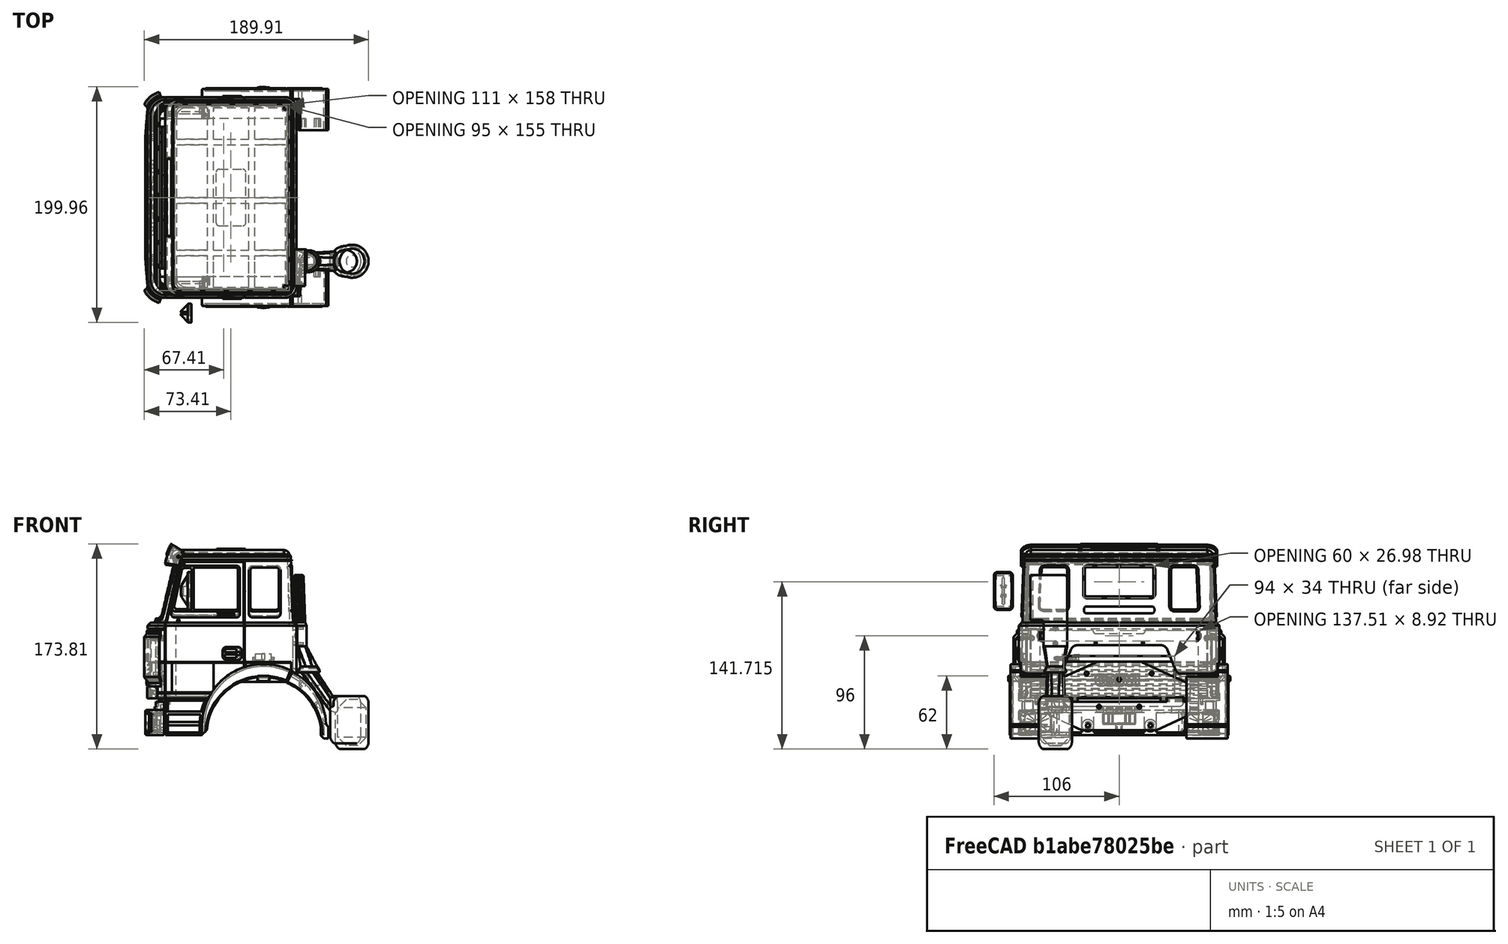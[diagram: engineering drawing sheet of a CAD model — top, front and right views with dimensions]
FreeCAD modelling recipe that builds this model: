
FCSTD DOCUMENT  (FreeCAD 0.18.4R)
Label: Cab-Iveco-Turbo-19
License: CC-BY 3.0
LicenseURL: http://creativecommons.org/licenses/by/3.0/
objects: Part::Box×507, Part::Cut×417, Part::Fillet×310, Part::Cylinder×272, Part::MultiFuse×251, Part::Mirroring×68, Part::Chamfer×61, Part::Feature×40, Part::Loft×19, Part::Part2DObjectPython×10, Part::Extrusion×10, Part::Cone×2, App::DocumentObjectGroup×1
note: 1967 computed .brp shape members not serialized (recipe doc carries the construction recipe); baked Part::Feature solids carry a one-line shape summary decoded from their .brp

FEATURE [Part::Box] Box  label="Cube250"
  AttacherType = Attacher::AttachEngine3D
  Height = 64
  Length = 126
  Width = 170
FEATURE [Part::Fillet] Fillet001
  Base = -> Box
  Edges = 2 edges r=15: [Edge1,Edge3]
FEATURE [Part::Fillet] Fillet
  Base = -> Fillet001
  Edges = 2 edges r=10: [Edge17,Edge18]
FEATURE [Part::Box] Box001  label="Cube251"
  AttacherType = Attacher::AttachEngine3D
  Height = 64
  Length = 120
  Placement = pos=(4,4,0) rot=(0,0,1;0rad)
  Width = 164
FEATURE [Part::Fillet] Fillet003
  Base = -> Box001
  Edges = 2 edges r=12: [Edge1,Edge3]
FEATURE [Part::Fillet] Fillet002
  Base = -> Fillet003
  Edges = 2 edges r=6: [Edge17,Edge18]
  Placement = pos=(-1,-1,0) rot=(0,0,1;0rad)
FEATURE [Part::Cut] Cut001
  Base = -> Fillet
  Refine = true
  Tool = -> Fillet002
FEATURE [Part::Cylinder] Cylinder004
  Angle = 360
  AttacherType = Attacher::AttachEngine3D
  Height = 174
  Placement = pos=(98,174,-23) rot=(1,0,0;1.5708rad)
  Radius = 52
FEATURE [Part::Cut] Cut
  Base = -> Cut001
  Refine = true
  Tool = -> Cylinder004
FEATURE [Part::Box] Box002  label="Cube252"
  AttacherType = Attacher::AttachEngine3D
  Height = 25
  Length = 131
  Placement = pos=(11,0,6) rot=(0,0,1;0rad)
  Width = 170
FEATURE [Part::Box] Box003  label="Cube253"
  AttacherType = Attacher::AttachEngine3D
  Height = 25
  Length = 148
  Placement = pos=(2,2,6) rot=(0,0,1;0rad)
  Width = 166
FEATURE [Part::Box] Box009  label="Cube192"
  AttacherType = Attacher::AttachEngine3D
  Height = 5.8
  Length = 13.6
  Placement = pos=(91.2,163,27) rot=(0,0,1;0rad)
  Width = 4
FEATURE [Part::Box] Box010  label="Cube254"
  AttacherType = Attacher::AttachEngine3D
  Height = 23
  Length = 37
  Placement = pos=(15,152,-23) rot=(0,0,1;0rad)
  Width = 18
FEATURE [Part::Cylinder] Cylinder012
  Angle = 360
  AttacherType = Attacher::AttachEngine3D
  Height = 22
  Placement = pos=(98,174,-23) rot=(1,0,0;1.5708rad)
  Radius = 52
FEATURE [Part::Box] Box011  label="Cube255"
  AttacherType = Attacher::AttachEngine3D
  Height = 9
  Length = 31
  Placement = pos=(17,156,-29) rot=(0,0,1;0rad)
  Width = 14
FEATURE [Part::Cylinder] Cylinder013
  Angle = 360
  AttacherType = Attacher::AttachEngine3D
  Height = 22
  Placement = pos=(98,174,-23) rot=(1,0,0;1.5708rad)
  Radius = 54
FEATURE [Part::Box] Box028  label="Cube266"
  AttacherType = Attacher::AttachEngine3D
  Height = 31
  Length = 62
  Placement = pos=(83,1,2) rot=(0,0,1;0rad)
  Width = 1
FEATURE [Part::Box] Box029  label="Cube267"
  AttacherType = Attacher::AttachEngine3D
  Height = 31
  Length = 63.5
  Placement = pos=(83,-1,2) rot=(0,0,1;0.017453rad)
  Width = 2
FEATURE [Part::Cut] Cut052
  Base = -> Box028
  Refine = true
  Tool = -> Box029
FEATURE [Part::Cylinder] Cylinder037
  Angle = 360
  AttacherType = Attacher::AttachEngine3D
  Height = 10
  Placement = pos=(98,10,-23) rot=(1,0,0;1.5708rad)
  Radius = 52
FEATURE [Part::Cut] Cut051
  Base = -> Cut052
  Refine = true
  Tool = -> Cylinder037
FEATURE [Part::Cylinder] Cylinder038
  Angle = 360
  AttacherType = Attacher::AttachEngine3D
  Height = 10
  Placement = pos=(98,10,-23) rot=(1,0,0;1.5708rad)
  Radius = 52
FEATURE [Part::Box] Box030  label="Cube268"
  AttacherType = Attacher::AttachEngine3D
  Height = 25
  Length = 63.5
  Placement = pos=(20,1,8) rot=(0,0,-1;0.027925rad)
  Width = 1
FEATURE [Part::Box] Box031  label="Cube269"
  AttacherType = Attacher::AttachEngine3D
  Height = 25
  Length = 62.5
  Placement = pos=(20.5,1,8) rot=(0,0,1;0rad)
  Width = 1
FEATURE [Part::Cut] Cut054
  Base = -> Box031
  Refine = true
  Tool = -> Box030
FEATURE [Part::Cut] Cut053
  Base = -> Cut054
  Refine = true
  Tool = -> Cylinder038
FEATURE [Part::MultiFuse] Fusion007
  Refine = true
  Shapes = -> [Cut051,Cut053]
FEATURE [Part::Box] Box032  label="Cube270"
  AttacherType = Attacher::AttachEngine3D
  Height = 25
  Length = 63.5
  Placement = pos=(20,1,8) rot=(0,0,-1;0.027925rad)
  Width = 1
FEATURE [Part::Box] Box033  label="Cube271"
  AttacherType = Attacher::AttachEngine3D
  Height = 25
  Length = 62.5
  Placement = pos=(20.5,1,8) rot=(0,0,1;0rad)
  Width = 1
FEATURE [Part::Cut] Cut057
  Base = -> Box033
  Refine = true
  Tool = -> Box032
FEATURE [Part::Box] Box034  label="Cube272"
  AttacherType = Attacher::AttachEngine3D
  Height = 31
  Length = 63.5
  Placement = pos=(83,-1,2) rot=(0,0,1;0.017453rad)
  Width = 2
FEATURE [Part::Box] Box035  label="Cube273"
  AttacherType = Attacher::AttachEngine3D
  Height = 31
  Length = 62
  Placement = pos=(83,1,2) rot=(0,0,1;0rad)
  Width = 1
FEATURE [Part::Cut] Cut055
  Base = -> Box035
  Refine = true
  Tool = -> Box034
FEATURE [Part::Cylinder] Cylinder039
  Angle = 360
  AttacherType = Attacher::AttachEngine3D
  Height = 10
  Placement = pos=(98,10,-23) rot=(1,0,0;1.5708rad)
  Radius = 52
FEATURE [Part::Cut] Cut058
  Base = -> Cut055
  Refine = true
  Tool = -> Cylinder039
FEATURE [Part::Cylinder] Cylinder040
  Angle = 360
  AttacherType = Attacher::AttachEngine3D
  Height = 10
  Placement = pos=(98,10,-23) rot=(1,0,0;1.5708rad)
  Radius = 52
FEATURE [Part::Cut] Cut056
  Base = -> Cut057
  Refine = true
  Tool = -> Cylinder040
FEATURE [Part::MultiFuse] Fusion008
  Refine = true
  Shapes = -> [Cut058,Cut056]
FEATURE [Part::Mirroring] Part__Mirroring001  label="Fusion008 (Mirror #2)"
  Base = (0,0,0)
  Normal = (0,1,0)
  Placement = pos=(0,170,0) rot=(0,0,1;0rad)
  Source = -> Fusion008
FEATURE [Part::MultiFuse] Fusion009
  Refine = true
  Shapes = -> [Part__Mirroring001,Fusion007]
FEATURE [Part::Cut] Cut059
  Base = -> Box002
  Placement = pos=(0,0,2) rot=(0,0,1;0rad)
  Refine = true
  Tool = -> Box003
FEATURE [Part::Cut] Cut060
  Base = -> Cut059
  Placement = pos=(0,0,-3) rot=(0,0,1;0rad)
  Refine = true
  Tool = -> Fusion009
FEATURE [Part::Cut] Cut061
  Base = -> Cut
  Refine = true
  Tool = -> Cut060
FEATURE [Part::Box] Box036  label="Cube274"
  AttacherType = Attacher::AttachEngine3D
  Height = 64
  Length = 21
  Width = 164
FEATURE [Part::Fillet] Fillet010
  Base = -> Box036
  Edges = 2 edges r=12: [Edge1,Edge3]
  Placement = pos=(3,3,0) rot=(0,0,1;0rad)
FEATURE [Part::Box] Box038  label="Cube276"
  AttacherType = Attacher::AttachEngine3D
  Height = 59
  Length = 16
  Placement = pos=(15,0,0) rot=(0,0,1;0rad)
  Width = 170
FEATURE [Part::Box] Box039  label="Cube277"
  AttacherType = Attacher::AttachEngine3D
  Height = 59
  Length = 21
  Placement = pos=(-13,3,0) rot=(0,0,1;0rad)
  Width = 164
FEATURE [Part::Box] Box040  label="Cube278"
  AttacherType = Attacher::AttachEngine3D
  Height = 59
  Length = 21
  Placement = pos=(-13,0,0) rot=(0,0,1;0rad)
  Width = 170
FEATURE [Part::Fillet] Fillet011
  Base = -> Box040
  Edges = 2 edges r=15: [Edge1,Edge3]
FEATURE [Part::Fillet] Fillet012
  Base = -> Box039
  Edges = 2 edges r=12: [Edge1,Edge3]
  Placement = pos=(3,0,0) rot=(0,0,1;0rad)
FEATURE [Part::Cut] Cut063
  Base = -> Fillet011
  Placement = pos=(13,0,0) rot=(0,0,1;0rad)
  Refine = true
  Tool = -> Fillet012
FEATURE [Part::Cut] Cut064
  Base = -> Cut063
  Refine = true
  Tool = -> Box038
FEATURE [Part::Box] Box041  label="Cube279"
  AttacherType = Attacher::AttachEngine3D
  Height = 28
  Length = 21
  Placement = pos=(-13,3,0) rot=(0,0,1;0rad)
  Width = 164
FEATURE [Part::Fillet] Fillet014
  Base = -> Box041
  Edges = 2 edges r=12: [Edge1,Edge3]
  Placement = pos=(2.5,0,0) rot=(0,0,1;0rad)
FEATURE [Part::Box] Box042  label="Cube280"
  AttacherType = Attacher::AttachEngine3D
  Height = 28
  Length = 21
  Placement = pos=(-13,0,0) rot=(0,0,1;0rad)
  Width = 170
FEATURE [Part::Fillet] Fillet013
  Base = -> Box042
  Edges = 2 edges r=15: [Edge1,Edge3]
FEATURE [Part::Cut] Cut067
  Base = -> Fillet013
  Placement = pos=(13,0,30) rot=(0,0,1;0rad)
  Refine = true
  Tool = -> Fillet014
FEATURE [Part::Box] Box043  label="Cube281"
  AttacherType = Attacher::AttachEngine3D
  Height = 59
  Length = 16
  Placement = pos=(14.5,0,0) rot=(0,0,1;0rad)
  Width = 170
FEATURE [Part::Cut] Cut066
  Base = -> Cut067
  Refine = true
  Tool = -> Box043
FEATURE [Part::Box] Box044  label="Cube282"
  AttacherType = Attacher::AttachEngine3D
  Height = 3
  Length = 3
  Placement = pos=(0,63,55) rot=(0,0,1;0rad)
  Width = 44
FEATURE [Part::Fillet] Fillet015
  Base = -> Box044
  Edges = 2 edges r=2: [Edge9,Edge11]
FEATURE [Part::Box] Box047  label="Cube285"
  AttacherType = Attacher::AttachEngine3D
  Height = 33
  Length = 21
  Placement = pos=(-13,3,0) rot=(0,0,1;0rad)
  Width = 164
FEATURE [Part::Fillet] Fillet016
  Base = -> Box047
  Edges = 2 edges r=12: [Edge1,Edge3]
  Placement = pos=(15.5,0,0) rot=(0,0,1;0rad)
FEATURE [Part::Box] Box070  label="Cube308"
  AttacherType = Attacher::AttachEngine3D
  Height = 4
  Length = 21
  Placement = pos=(-13,0,26) rot=(0,0,1;0rad)
  Width = 170
FEATURE [Part::Fillet] Fillet026
  Base = -> Box070
  Edges = 2 edges r=15: [Edge1,Edge3]
FEATURE [Part::Chamfer] Chamfer011
  Base = -> Fillet026
  Edges = 1 edges r=3.5: [Edge1]
  Placement = pos=(13,0,2) rot=(0,0,1;0rad)
FEATURE [Part::Box] Box071  label="Cube309"
  AttacherType = Attacher::AttachEngine3D
  Height = 4
  Length = 11
  Placement = pos=(10.5,0,28) rot=(0,0,1;0rad)
  Width = 170
FEATURE [Part::Cut] Cut077
  Base = -> Chamfer011
  Placement = pos=(0,0,-28) rot=(0,0,1;0rad)
  Refine = true
  Tool = -> Box071
FEATURE [Part::Box] Box072  label="Cube310"
  AttacherType = Attacher::AttachEngine3D
  Height = 4
  Length = 21
  Placement = pos=(-13,0,26) rot=(0,0,1;0rad)
  Width = 170
FEATURE [Part::Box] Box073  label="Cube311"
  AttacherType = Attacher::AttachEngine3D
  Height = 4
  Length = 11
  Placement = pos=(10.5,0,28) rot=(0,0,1;0rad)
  Width = 170
FEATURE [Part::Fillet] Fillet027
  Base = -> Box072
  Edges = 2 edges r=15: [Edge1,Edge3]
FEATURE [Part::Chamfer] Chamfer012
  Base = -> Fillet027
  Edges = 1 edges r=3.5: [Edge1]
  Placement = pos=(13,0,2) rot=(0,0,1;0rad)
FEATURE [Part::Cut] Cut078
  Base = -> Chamfer012
  Placement = pos=(0,0,-24) rot=(0,0,1;0rad)
  Refine = true
  Tool = -> Box073
FEATURE [Part::Box] Box074  label="Cube312"
  AttacherType = Attacher::AttachEngine3D
  Height = 4
  Length = 21
  Placement = pos=(-13,0,26) rot=(0,0,1;0rad)
  Width = 170
FEATURE [Part::Box] Box075  label="Cube313"
  AttacherType = Attacher::AttachEngine3D
  Height = 4
  Length = 11
  Placement = pos=(10.5,0,28) rot=(0,0,1;0rad)
  Width = 170
FEATURE [Part::Fillet] Fillet028
  Base = -> Box074
  Edges = 2 edges r=15: [Edge1,Edge3]
FEATURE [Part::Chamfer] Chamfer013
  Base = -> Fillet028
  Edges = 1 edges r=3.5: [Edge1]
  Placement = pos=(13,0,2) rot=(0,0,1;0rad)
FEATURE [Part::Cut] Cut079
  Base = -> Chamfer013
  Placement = pos=(0,0,-20) rot=(0,0,1;0rad)
  Refine = true
  Tool = -> Box075
FEATURE [Part::Box] Box076  label="Cube314"
  AttacherType = Attacher::AttachEngine3D
  Height = 4
  Length = 21
  Placement = pos=(-13,0,26) rot=(0,0,1;0rad)
  Width = 170
FEATURE [Part::Box] Box077  label="Cube315"
  AttacherType = Attacher::AttachEngine3D
  Height = 4
  Length = 11
  Placement = pos=(10.5,0,28) rot=(0,0,1;0rad)
  Width = 170
FEATURE [Part::Fillet] Fillet029
  Base = -> Box076
  Edges = 2 edges r=15: [Edge1,Edge3]
FEATURE [Part::Chamfer] Chamfer014
  Base = -> Fillet029
  Edges = 1 edges r=3.5: [Edge1]
  Placement = pos=(13,0,2) rot=(0,0,1;0rad)
FEATURE [Part::Cut] Cut080
  Base = -> Chamfer014
  Placement = pos=(0,0,-16) rot=(0,0,1;0rad)
  Refine = true
  Tool = -> Box077
FEATURE [Part::Box] Box078  label="Cube316"
  AttacherType = Attacher::AttachEngine3D
  Height = 4
  Length = 21
  Placement = pos=(-13,0,26) rot=(0,0,1;0rad)
  Width = 170
FEATURE [Part::Box] Box079  label="Cube317"
  AttacherType = Attacher::AttachEngine3D
  Height = 4
  Length = 11
  Placement = pos=(10.5,0,28) rot=(0,0,1;0rad)
  Width = 170
FEATURE [Part::Fillet] Fillet030
  Base = -> Box078
  Edges = 2 edges r=15: [Edge1,Edge3]
FEATURE [Part::Chamfer] Chamfer015
  Base = -> Fillet030
  Edges = 1 edges r=3.5: [Edge1]
  Placement = pos=(13,0,2) rot=(0,0,1;0rad)
FEATURE [Part::Cut] Cut081
  Base = -> Chamfer015
  Placement = pos=(0,0,-12) rot=(0,0,1;0rad)
  Refine = true
  Tool = -> Box079
FEATURE [Part::Box] Box080  label="Cube318"
  AttacherType = Attacher::AttachEngine3D
  Height = 4
  Length = 21
  Placement = pos=(-13,0,26) rot=(0,0,1;0rad)
  Width = 170
FEATURE [Part::Box] Box081  label="Cube319"
  AttacherType = Attacher::AttachEngine3D
  Height = 4
  Length = 11
  Placement = pos=(10.5,0,28) rot=(0,0,1;0rad)
  Width = 170
FEATURE [Part::Fillet] Fillet031
  Base = -> Box080
  Edges = 2 edges r=15: [Edge1,Edge3]
FEATURE [Part::Chamfer] Chamfer016
  Base = -> Fillet031
  Edges = 1 edges r=3.5: [Edge1]
  Placement = pos=(13,0,2) rot=(0,0,1;0rad)
FEATURE [Part::Cut] Cut082
  Base = -> Chamfer016
  Placement = pos=(0,0,-8) rot=(0,0,1;0rad)
  Refine = true
  Tool = -> Box081
FEATURE [Part::Box] Box082  label="Cube320"
  AttacherType = Attacher::AttachEngine3D
  Height = 4
  Length = 21
  Placement = pos=(-13,0,26) rot=(0,0,1;0rad)
  Width = 170
FEATURE [Part::Box] Box083  label="Cube321"
  AttacherType = Attacher::AttachEngine3D
  Height = 4
  Length = 11
  Placement = pos=(10.5,0,28) rot=(0,0,1;0rad)
  Width = 170
FEATURE [Part::Fillet] Fillet032
  Base = -> Box082
  Edges = 2 edges r=15: [Edge1,Edge3]
FEATURE [Part::Chamfer] Chamfer017
  Base = -> Fillet032
  Edges = 1 edges r=3.5: [Edge1]
  Placement = pos=(13,0,2) rot=(0,0,1;0rad)
FEATURE [Part::Cut] Cut083
  Base = -> Chamfer017
  Placement = pos=(0,0,-4) rot=(0,0,1;0rad)
  Refine = true
  Tool = -> Box083
FEATURE [Part::Box] Box084  label="Cube322"
  AttacherType = Attacher::AttachEngine3D
  Height = 4
  Length = 21
  Placement = pos=(-13,0,26) rot=(0,0,1;0rad)
  Width = 170
FEATURE [Part::Box] Box085  label="Cube323"
  AttacherType = Attacher::AttachEngine3D
  Height = 4
  Length = 11
  Placement = pos=(10.5,0,28) rot=(0,0,1;0rad)
  Width = 170
FEATURE [Part::Fillet] Fillet033
  Base = -> Box084
  Edges = 2 edges r=15: [Edge1,Edge3]
FEATURE [Part::Chamfer] Chamfer018
  Base = -> Fillet033
  Edges = 1 edges r=3.5: [Edge1]
  Placement = pos=(13,0,2) rot=(0,0,1;0rad)
FEATURE [Part::Cut] Cut084
  Base = -> Chamfer018
  Refine = true
  Tool = -> Box085
FEATURE [Part::MultiFuse] Fusion011
  Refine = true
  Shapes = -> [Cut084,Cut083,Cut080,Cut081,Cut078,Cut079,Cut082,Cut077]
FEATURE [Part::Box] Box086  label="Cube324"
  AttacherType = Attacher::AttachEngine3D
  Height = 30
  Length = 21
  Placement = pos=(-13,3,0) rot=(0,0,1;0rad)
  Width = 164
FEATURE [Part::Fillet] Fillet034
  Base = -> Box086
  Edges = 2 edges r=12: [Edge1,Edge3]
  Placement = pos=(15.5,0,0) rot=(0,0,1;0rad)
FEATURE [Part::Box] Box087  label="Cube325"
  AttacherType = Attacher::AttachEngine3D
  Height = 30
  Length = 21
  Placement = pos=(-13,2.5,0) rot=(0,0,1;0rad)
  Width = 165
FEATURE [Part::Fillet] Fillet035
  Base = -> Box087
  Edges = 2 edges r=12.5: [Edge1,Edge3]
  Placement = pos=(15,0,0) rot=(0,0,1;0rad)
FEATURE [Part::Cut] Cut086
  Base = -> Fillet035
  Refine = true
  Tool = -> Fillet034
FEATURE [Part::Box] Box088  label="Cube326"
  AttacherType = Attacher::AttachEngine3D
  Height = 30
  Length = 16
  Placement = pos=(10.5,0,0) rot=(0,0,1;0rad)
  Width = 170
FEATURE [Part::Cut] Cut087
  Base = -> Cut086
  Refine = true
  Tool = -> Box088
FEATURE [Part::Box] Box089  label="Cube327"
  AttacherType = Attacher::AttachEngine3D
  Height = 3
  Length = 21
  Placement = pos=(-5,0,30) rot=(0,0,1;0rad)
  Width = 170
FEATURE [Part::Feature] Face
  Placement = pos=(0,0,-10) rot=(0,0,1;0rad)
  shape: bbox 128.7 x 180.4 x 2e-07 mm, 1 faces, 0 solids (baked)
FEATURE [Part::Feature] Face002
  Placement = pos=(0,0,50) rot=(0,0,1;0rad)
  shape: bbox 110 x 176 x 2e-07 mm, 1 faces, 0 solids (baked)
FEATURE [Part::Loft] Loft
  Closed = false
  MaxDegree = 5
  Ruled = false
  Sections = -> [Face002,Face]
  Solid = true
FEATURE [Part::Feature] Face003
  Placement = pos=(0,0,50) rot=(0,0,1;0rad)
  shape: bbox 103.4 x 169.4 x 2e-07 mm, 1 faces, 0 solids (baked)
FEATURE [Part::Feature] Face004
  Placement = pos=(0,0,-10) rot=(0,0,1;0rad)
  shape: bbox 122.1 x 173.8 x 2e-07 mm, 1 faces, 0 solids (baked)
FEATURE [Part::Loft] Loft001
  Closed = false
  MaxDegree = 5
  Ruled = false
  Sections = -> [Face003,Face004]
  Solid = true
FEATURE [Part::Cut] Cut091
  Base = -> Loft
  Refine = true
  Tool = -> Loft001
FEATURE [Part::Box] Box094  label="Cube332"
  AttacherType = Attacher::AttachEngine3D
  Height = 30
  Length = 21
  Placement = pos=(-13,0,0) rot=(0,0,1;0rad)
  Width = 170
FEATURE [Part::Fillet] Fillet044
  Base = -> Box094
  Edges = 2 edges r=15: [Edge1,Edge3]
FEATURE [Part::Box] Box095  label="Cube333"
  AttacherType = Attacher::AttachEngine3D
  Height = 30
  Length = 21
  Placement = pos=(-13,3,0) rot=(0,0,1;0rad)
  Width = 164
FEATURE [Part::Fillet] Fillet045
  Base = -> Box095
  Edges = 2 edges r=12: [Edge1,Edge3]
  Placement = pos=(2.5,0,0) rot=(0,0,1;0rad)
FEATURE [Part::Cut] Cut092
  Base = -> Fillet044
  Placement = pos=(13,0,0) rot=(0,0,1;0rad)
  Refine = true
  Tool = -> Fillet045
FEATURE [Part::Box] Box096  label="Cube334"
  AttacherType = Attacher::AttachEngine3D
  Height = 30
  Length = 16
  Placement = pos=(14.5,0,0) rot=(0,0,1;0rad)
  Width = 170
FEATURE [Part::Cut] Cut093
  Base = -> Cut092
  Refine = true
  Tool = -> Box096
FEATURE [Part::Box] Box097  label="Cube335"
  AttacherType = Attacher::AttachEngine3D
  Height = 30
  Length = 16
  Placement = pos=(0,10,0) rot=(0,0,1;0rad)
  Width = 150
FEATURE [Part::Cut] Cut094
  Base = -> Cut093
  Refine = true
  Tool = -> Box097
FEATURE [Part::Box] Box098  label="Cube336"
  AttacherType = Attacher::AttachEngine3D
  Height = 30
  Length = 16
  Placement = pos=(10.5,0,0) rot=(0,0,1;0rad)
  Width = 170
FEATURE [Part::Box] Box099  label="Cube337"
  AttacherType = Attacher::AttachEngine3D
  Height = 30
  Length = 21
  Placement = pos=(-13,0,0) rot=(0,0,1;0rad)
  Width = 170
FEATURE [Part::Fillet] Fillet047
  Base = -> Box099
  Edges = 2 edges r=15: [Edge1,Edge3]
FEATURE [Part::Box] Box100  label="Cube338"
  AttacherType = Attacher::AttachEngine3D
  Height = 30
  Length = 21
  Placement = pos=(-13,3,0) rot=(0,0,1;0rad)
  Width = 164
FEATURE [Part::Fillet] Fillet046
  Base = -> Box100
  Edges = 2 edges r=12: [Edge1,Edge3]
  Placement = pos=(2.5,0,0) rot=(0,0,1;0rad)
FEATURE [Part::Cut] Cut096
  Base = -> Fillet047
  Placement = pos=(13,0,0) rot=(0,0,1;0rad)
  Refine = true
  Tool = -> Fillet046
FEATURE [Part::Cut] Cut097
  Base = -> Cut096
  Refine = true
  Tool = -> Box098
FEATURE [Part::Box] Box101  label="Cube339"
  AttacherType = Attacher::AttachEngine3D
  Height = 30
  Length = 16
  Placement = pos=(0,10.5,0) rot=(0,0,1;0rad)
  Width = 149
FEATURE [Part::Cut] Cut095
  Base = -> Cut097
  Refine = true
  Tool = -> Box101
FEATURE [Part::Box] Box102  label="Cube340"
  AttacherType = Attacher::AttachEngine3D
  Height = 55
  Length = 10
  Placement = pos=(0,7,68) rot=(0,1,0;0.226893rad)
  Width = 156
FEATURE [Part::Cut] Cut099
  Base = -> Cut066
  Refine = true
  Tool = -> Fillet015
FEATURE [Part::Cut] Cut100
  Base = -> Fusion011
  Refine = true
  Tool = -> Fillet016
FEATURE [Part::MultiFuse] Fusion016
  Refine = true
  Shapes = -> [Cut087,Cut100]
FEATURE [Part::Cut] Cut101
  Base = -> Fusion016
  Refine = true
  Tool = -> Box089
FEATURE [Part::Cut] Cut102  label="radiator-grid-00"
  Base = -> Cut101
  Refine = true
  Tool = -> Cut095
FEATURE [Part::Chamfer] Chamfer
  Base = -> Cut061
  Edges = 4 edges r=2.5: [Edge1,Edge4,Edge5,Edge8]
FEATURE [Part::Chamfer] Chamfer019
  Base = -> Chamfer
  Edges = 4 edges r=0.9: [Edge52,Edge80,Edge102,Edge110]
FEATURE [Part::Box] Box104  label="Cube342"
  AttacherType = Attacher::AttachEngine3D
  Height = 7.5
  Length = 4
  Placement = pos=(44,152,-31) rot=(0,0,1;0rad)
  Width = 22
FEATURE [Part::Box] Box105  label="Cube343"
  AttacherType = Attacher::AttachEngine3D
  Height = 18
  Length = 31
  Placement = pos=(17,158,-20) rot=(0,0,1;0rad)
  Width = 12
FEATURE [Part::Cylinder] Cylinder043
  Angle = 360
  AttacherType = Attacher::AttachEngine3D
  Height = 22
  Placement = pos=(98,174,-23) rot=(1,0,0;1.5708rad)
  Radius = 54
FEATURE [Part::Cut] Cut108
  Base = -> Box105
  Refine = true
  Tool = -> Cylinder043
FEATURE [Part::Box] Box106  label="Cube344"
  AttacherType = Attacher::AttachEngine3D
  Height = 21
  Length = 38
  Placement = pos=(15,167,-23) rot=(0,0,1;0rad)
  Width = 3
FEATURE [Part::Box] Box107  label="Cube345"
  AttacherType = Attacher::AttachEngine3D
  Height = 7
  Length = 10
  Placement = pos=(46,152,-30) rot=(0,0,1;0rad)
  Width = 25
FEATURE [Part::Cylinder] Cylinder044
  Angle = 360
  AttacherType = Attacher::AttachEngine3D
  Height = 25
  Placement = pos=(98,177,-23) rot=(0.799251,-0.424969,0.424969;1.79303rad)
  Radius = 52
FEATURE [Part::Cylinder] Cylinder045
  Angle = 360
  AttacherType = Attacher::AttachEngine3D
  Height = 28
  Placement = pos=(98,175,-23) rot=(0.799251,-0.424969,0.424969;1.79303rad)
  Radius = 50
FEATURE [Part::Cylinder] Cylinder046
  Angle = 360
  AttacherType = Attacher::AttachEngine3D
  Height = 30
  Placement = pos=(98,177,-30) rot=(0.799251,-0.424969,0.424969;1.79303rad)
  Radius = 48
FEATURE [Part::MultiFuse] Fusion018
  Refine = true
  Shapes = -> [Box107,Cylinder044]
FEATURE [Part::Box] Box108  label="Cube346"
  AttacherType = Attacher::AttachEngine3D
  Height = 7
  Length = 10
  Placement = pos=(48,147,-30) rot=(0,0,1;0rad)
  Width = 28
FEATURE [Part::Cut] Cut111
  Base = -> Fusion018
  Refine = true
  Tool = -> Cylinder045
FEATURE [Part::Cut] Cut112
  Base = -> Cut111
  Refine = true
  Tool = -> Cylinder046
FEATURE [Part::Cut] Cut113
  Base = -> Cut112
  Refine = true
  Tool = -> Box108
FEATURE [Part::Box] Box109  label="Cube347"
  AttacherType = Attacher::AttachEngine3D
  Height = 7
  Length = 45
  Placement = pos=(76,175,14) rot=(0,0,1;0rad)
  Width = 2
FEATURE [Part::MultiFuse] Fusion019
  Refine = true
  Shapes = -> [Cut113,Box109]
FEATURE [Part::Box] Box110  label="Cube348"
  AttacherType = Attacher::AttachEngine3D
  Height = 14
  Length = 10
  Placement = pos=(116,168,12) rot=(0,1,0;0.401426rad)
  Width = 9
FEATURE [Part::Fillet] Fillet050
  Base = -> Box102
  Edges = 4 edges r=5: [Edge9,Edge10,Edge11,Edge12]
  Placement = pos=(6,0,-1) rot=(0,0,1;0rad)
FEATURE [Part::Box] Box124  label="Cube024"
  AttacherType = Attacher::AttachEngine3D
  Height = 42
  Length = 26
  Placement = pos=(89,4.3,70) rot=(-1,0,0;0.038397rad)
  Width = 5
FEATURE [Part::Fillet] Fillet051
  Base = -> Box124
  Edges = 4 edges r=3: [Edge2,Edge4,Edge6,Edge8]
  Placement = pos=(-3,-2,0) rot=(0,0,1;0rad)
FEATURE [Part::Box] Box126  label="Cube048"
  AttacherType = Attacher::AttachEngine3D
  Height = 42
  Length = 58
  Placement = pos=(19.5,2,70) rot=(-1,0,0;0.038397rad)
  Width = 5
FEATURE [Part::Box] Box127  label="Cube049"
  AttacherType = Attacher::AttachEngine3D
  Height = 48
  Length = 11
  Placement = pos=(8.5,1,70) rot=(-0.179679,0.983544,0.018885;0.212918rad)
  Width = 7
FEATURE [Part::Cut] Cut129
  Base = -> Box126
  Refine = true
  Tool = -> Box127
FEATURE [Part::Fillet] Fillet052
  Base = -> Cut129
  Edges = 4 edges r=3: [Edge2,Edge4,Edge8,Edge12]
FEATURE [Part::MultiFuse] Fusion029  label="left-windows-holes"
  Refine = true
  Shapes = -> [Fillet051,Fillet052]
FEATURE [Part::Box] Box128  label="Cube362"
  AttacherType = Attacher::AttachEngine3D
  Height = 42
  Length = 26
  Placement = pos=(89,4.3,70) rot=(-1,0,0;0.038397rad)
  Width = 5
FEATURE [Part::Fillet] Fillet053
  Base = -> Box128
  Edges = 4 edges r=3: [Edge2,Edge4,Edge6,Edge8]
  Placement = pos=(-3,-2,0) rot=(0,0,1;0rad)
FEATURE [Part::Box] Box129  label="Cube363"
  AttacherType = Attacher::AttachEngine3D
  Height = 42
  Length = 58
  Placement = pos=(19.5,2,70) rot=(-1,0,0;0.038397rad)
  Width = 5
FEATURE [Part::Box] Box130  label="Cube364"
  AttacherType = Attacher::AttachEngine3D
  Height = 48
  Length = 11
  Placement = pos=(8.5,1,70) rot=(-0.179679,0.983544,0.018885;0.212918rad)
  Width = 7
FEATURE [Part::Cut] Cut130
  Base = -> Box129
  Refine = true
  Tool = -> Box130
FEATURE [Part::Fillet] Fillet054
  Base = -> Cut130
  Edges = 4 edges r=3: [Edge2,Edge4,Edge8,Edge12]
FEATURE [Part::MultiFuse] Fusion030
  Refine = true
  Shapes = -> [Fillet053,Fillet054]
FEATURE [Part::Mirroring] Part__Mirroring  label="right-windows-holes"
  Base = (0,0,0)
  Normal = (0,1,0)
  Placement = pos=(0,170,0) rot=(0,0,1;0rad)
  Source = -> Fusion030
FEATURE [Part::Box] Box131  label="Cube086"
  AttacherType = Attacher::AttachEngine3D
  Height = 25
  Length = 10
  Placement = pos=(150,40,0) rot=(0,0,1;0rad)
  Width = 100
FEATURE [Part::Box] Box132  label="Cube089"
  AttacherType = Attacher::AttachEngine3D
  Height = 40
  Length = 10
  Placement = pos=(150,19,0) rot=(-1,0,0;0.383972rad)
  Width = 20
FEATURE [Part::Box] Box133  label="Cube088"
  AttacherType = Attacher::AttachEngine3D
  Height = 40
  Length = 10
  Placement = pos=(150,19,0) rot=(-1,0,0;0.383972rad)
  Width = 20
FEATURE [Part::Mirroring] Part__Mirroring003  label="Cube088 (Mirror #13)"
  Base = (0,0,0)
  Normal = (0,1,0)
  Placement = pos=(0,180,0) rot=(0,0,1;0rad)
  Source = -> Box133
FEATURE [Part::MultiFuse] Fusion033
  Refine = true
  Shapes = -> [Box132,Part__Mirroring003]
FEATURE [Part::Cut] Cut132
  Base = -> Box131
  Placement = pos=(-30,-5,20) rot=(0,0,1;0rad)
  Refine = true
  Tool = -> Fusion033
FEATURE [Part::Fillet] Fillet055
  Base = -> Cut132
  Edges = 2 edges r=6: [Edge5,Edge6]
FEATURE [Part::Cut] Cut134
  Base = -> Fusion019
  Refine = true
  Tool = -> Box110
FEATURE [Part::Box] Box134  label="Cube365"
  AttacherType = Attacher::AttachEngine3D
  Height = 10
  Length = 10
  Placement = pos=(46,152,-31) rot=(0,1,0;0.785398rad)
  Width = 25
FEATURE [Part::Box] Box147  label="Cube074"
  AttacherType = Attacher::AttachEngine3D
  Height = 27
  Length = 7
  Placement = pos=(116,55,85) rot=(0,-1,0;0.034907rad)
  Width = 60
FEATURE [Part::Box] Box148  label="Cube079"
  AttacherType = Attacher::AttachEngine3D
  Height = 38
  Length = 5
  Placement = pos=(175,0,0) rot=(0,0,1;0rad)
  Width = 25
FEATURE [Part::Box] Box149  label="Cube080"
  AttacherType = Attacher::AttachEngine3D
  Height = 40
  Length = 5
  Placement = pos=(175,-24,-1) rot=(-1,0,0;0.038397rad)
  Width = 24
FEATURE [Part::Cut] Cut149
  Base = -> Box148
  Placement = pos=(0,1,1) rot=(0,0,1;0rad)
  Refine = true
  Tool = -> Box149
FEATURE [Part::Cylinder] Cylinder052
  Angle = 360
  AttacherType = Attacher::AttachEngine3D
  Height = 134
  Radius = 3.7
FEATURE [Part::Fillet] Fillet062
  Base = -> Cylinder052
  Edges = 2 edges r=2: [Edge1,Edge3]
  Placement = pos=(128,152,53) rot=(1,0,0;1.5708rad)
FEATURE [Part::Box] Box150  label="Cube378"
  AttacherType = Attacher::AttachEngine3D
  Height = 38
  Length = 5
  Placement = pos=(175,0,0) rot=(0,0,1;0rad)
  Width = 25
FEATURE [Part::Box] Box151  label="Cube379"
  AttacherType = Attacher::AttachEngine3D
  Height = 40
  Length = 5
  Placement = pos=(175,-24,-1) rot=(-1,0,0;0.038397rad)
  Width = 24
FEATURE [Part::Cut] Cut150
  Base = -> Box150
  Placement = pos=(-57,17,74) rot=(0,0,1;0rad)
  Refine = true
  Tool = -> Box151
FEATURE [Part::Mirroring] Part__Mirroring005  label="Cut212"
  Base = (0,0,0)
  Normal = (0,1,0)
  Placement = pos=(-57,154,73) rot=(0,0,1;0rad)
  Source = -> Cut149
FEATURE [Part::Fillet] Fillet063
  Base = -> Cut150
  Edges = 4 edges r=3: [Edge1,Edge3,Edge5,Edge10]
  Placement = pos=(3,0,-4) rot=(0,-1,0;0.034907rad)
FEATURE [Part::Fillet] Fillet064
  Base = -> Part__Mirroring005
  Edges = 4 edges r=3: [Edge1,Edge3,Edge5,Edge10]
  Placement = pos=(3,0,-4) rot=(0,-1,0;0.034907rad)
FEATURE [Part::Cylinder] Cylinder053
  Angle = 360
  AttacherType = Attacher::AttachEngine3D
  Height = 60
  Radius = 3.7
FEATURE [Part::Fillet] Fillet066
  Base = -> Cylinder053
  Edges = 2 edges r=2: [Edge1,Edge3]
  Placement = pos=(125,115,75) rot=(1,0,0;1.5708rad)
FEATURE [Part::Box] Box152  label="Cube070"
  AttacherType = Attacher::AttachEngine3D
  Height = 9
  Length = 14
  Width = 2
FEATURE [Part::Fillet] Fillet068
  Base = -> Box152
  Edges = 4 edges r=2: [Edge2,Edge4,Edge6,Edge8]
  Placement = pos=(68.5,0,46.5) rot=(0,0,1;0rad)
FEATURE [Part::Box] Box153  label="Cube071"
  AttacherType = Attacher::AttachEngine3D
  Height = 9
  Length = 14
  Width = 2
FEATURE [Part::Fillet] Fillet069
  Base = -> Box153
  Edges = 4 edges r=2: [Edge2,Edge4,Edge6,Edge8]
  Placement = pos=(68.5,168,46.5) rot=(0,0,1;0rad)
FEATURE [Part::MultiFuse] Fusion042
  Placement = pos=(-4,0,-13) rot=(0,0,1;0rad)
  Refine = true
  Shapes = -> [Fillet069,Fillet068]
FEATURE [Part::Part2DObjectPython] ShapeString  # Draft 2D object (typed FeaturePython)
  FontFile = <userpath>/Data/Temp/Futura Extra Bold.ttf
  MapMode = 5
  Placement = pos=(0,103,12) rot=(0.57735,-0.57735,-0.57735;2.0944rad)
  Size = 3.5
  String = IVECO
  Tracking = 0.5
FEATURE [Part::Extrusion] Extrude  label="iveco-logo"
  Base = -> ShapeString
  Dir = (1,0,0)
  DirMode = 0
  FaceMakerClass = Part::FaceMakerExtrusion
  LengthFwd = 0
  LengthRev = 0
  Placement = pos=(-1,0,0) rot=(0,0,1;0rad)
  Solid = false
  Symmetric = false
FEATURE [Part::Part2DObjectPython] ShapeString001  # Draft 2D object (typed FeaturePython)
  FontFile = <path>
  MapMode = 5
  Placement = pos=(0,55,34) rot=(0.57735,-0.57735,-0.57735;2.0944rad)
  Size = 1.35
  String = T
  Tracking = 0
FEATURE [Part::Part2DObjectPython] ShapeString002  # Draft 2D object (typed FeaturePython)
  FontFile = <path>
  MapMode = 5
  Placement = pos=(0,51,34) rot=(0.57735,-0.57735,-0.57735;2.0944rad)
  Size = 1.3
  String = urbo
  Tracking = 0
FEATURE [Part::Extrusion] Extrude001
  Base = -> ShapeString001
  Dir = (1,0,0)
  DirMode = 0
  FaceMakerClass = Part::FaceMakerExtrusion
  LengthFwd = 0
  LengthRev = 0
  Solid = false
  Symmetric = false
FEATURE [Part::Extrusion] Extrude002
  Base = -> ShapeString002
  Dir = (1,0,0)
  DirMode = 0
  FaceMakerClass = Part::FaceMakerExtrusion
  LengthFwd = 0
  LengthRev = 0
  Solid = false
  Symmetric = false
FEATURE [Part::MultiFuse] Fusion047  label="turbo-logo"
  Placement = pos=(-1,-3,-2) rot=(0,0,1;0rad)
  Refine = true
  Shapes = -> [Extrude001,Extrude002]
FEATURE [Part::Box] Box167  label="Cube393"
  AttacherType = Attacher::AttachEngine3D
  Height = 21
  Length = 16
  Placement = pos=(-2,0,-30) rot=(0,0,1;0rad)
  Width = 170
FEATURE [Part::Cylinder] Cylinder056
  Angle = 360
  AttacherType = Attacher::AttachEngine3D
  Height = 21
  Placement = pos=(796.4,85,-30) rot=(0,0,1;2.96706rad)
  Radius = 800
FEATURE [Part::Box] Box168  label="Cube394"
  AttacherType = Attacher::AttachEngine3D
  Height = 21
  Length = 16
  Placement = pos=(-2,0,-30) rot=(0,0,1;0rad)
  Width = 170
FEATURE [Part::Cut] Cut163  label="Cut613"
  Base = -> Box168
  Refine = true
  Tool = -> Cylinder056
FEATURE [Part::Cut] Cut164  label="Cut177"
  Base = -> Box167
  Refine = true
  Tool = -> Cut163
FEATURE [Part::Fillet] Fillet083
  Base = -> Cut164
  Edges = 2 edges r=4: [Edge6,Edge12]
FEATURE [Part::Box] Box169  label="Cube395"
  AttacherType = Attacher::AttachEngine3D
  Height = 17
  Length = 20
  Placement = pos=(-2,0,-28) rot=(0,0,1;0rad)
  Width = 30
FEATURE [Part::Fillet] Fillet084
  Base = -> Box169
  Edges = 4 edges r=2: [Edge9,Edge10,Edge11,Edge12]
  Placement = pos=(-1,2,0) rot=(0,0,1;0rad)
FEATURE [Part::Box] Box170  label="Cube396"
  AttacherType = Attacher::AttachEngine3D
  Height = 17
  Length = 20
  Placement = pos=(-2,0,-28) rot=(0,0,1;0rad)
  Width = 30
FEATURE [Part::Fillet] Fillet085
  Base = -> Box170
  Edges = 4 edges r=2: [Edge9,Edge10,Edge11,Edge12]
  Placement = pos=(-1,138,0) rot=(0,0,1;0rad)
FEATURE [Part::MultiFuse] Fusion048
  Refine = true
  Shapes = -> [Fillet085,Fillet084]
FEATURE [Part::Box] Box171  label="Cube397"
  AttacherType = Attacher::AttachEngine3D
  Height = 17
  Length = 16
  Placement = pos=(-2,4,-30) rot=(0,0,1;0rad)
  Width = 162
FEATURE [Part::Fillet] Fillet086
  Base = -> Box171
  Edges = 2 edges r=3: [Edge1,Edge3]
  Placement = pos=(5,0,2) rot=(0,0,1;0rad)
FEATURE [Part::Cut] Cut165  label="Cut178"
  Base = -> Fillet083
  Refine = true
  Tool = -> Fillet086
FEATURE [Part::Box] Box172  label="Cube398"
  AttacherType = Attacher::AttachEngine3D
  Height = 17
  Length = 15
  Placement = pos=(2,30,-28) rot=(0,0,1;0rad)
  Width = 5
FEATURE [Part::Box] Box173  label="Cube399"
  AttacherType = Attacher::AttachEngine3D
  Height = 17
  Length = 15
  Placement = pos=(2,135,-28) rot=(0,0,1;0rad)
  Width = 5
FEATURE [Part::MultiFuse] Fusion049
  Refine = true
  Shapes = -> [Box173,Box172]
FEATURE [Part::Cut] Cut166  label="Cut561"
  Base = -> Fusion048
  Refine = true
  Tool = -> Fusion049
FEATURE [Part::Cut] Cut167  label="Cut625"
  Base = -> Cut165
  Refine = true
  Tool = -> Cut166
FEATURE [Part::Fillet] Fillet087
  Base = -> Cut167
  Edges = 4 edges r=2: [Edge60,Edge62,Edge92,Edge93]
FEATURE [Part::Box] Box174  label="Cube400"
  AttacherType = Attacher::AttachEngine3D
  Height = 21
  Length = 16
  Placement = pos=(6,5,-30) rot=(0,0,1;0rad)
  Width = 160
FEATURE [Part::Cylinder] Cylinder057
  Angle = 360
  AttacherType = Attacher::AttachEngine3D
  Height = 21
  Placement = pos=(504,85,-30) rot=(0,0,1;2.96706rad)
  Radius = 500
FEATURE [Part::Box] Box175  label="Cube401"
  AttacherType = Attacher::AttachEngine3D
  Height = 21
  Length = 16
  Placement = pos=(6,5,-30) rot=(0,0,1;0rad)
  Width = 160
FEATURE [Part::Cut] Cut168  label="Cut626"
  Base = -> Box174
  Refine = true
  Tool = -> Cylinder057
FEATURE [Part::Cut] Cut169  label="Cut564"
  Base = -> Box175
  Placement = pos=(2,0,0) rot=(0,0,1;0rad)
  Refine = true
  Tool = -> Cut168
FEATURE [Part::Fillet] Fillet088
  Base = -> Cut169
  Edges = 2 edges r=3: [Edge6,Edge12]
FEATURE [Part::Box] Box176  label="Cube402"
  AttacherType = Attacher::AttachEngine3D
  Height = 21
  Length = 16
  Placement = pos=(6,5,-30) rot=(0,0,1;0rad)
  Width = 160
FEATURE [Part::Box] Box177  label="Cube403"
  AttacherType = Attacher::AttachEngine3D
  Height = 21
  Length = 16
  Placement = pos=(6,5,-30) rot=(0,0,1;0rad)
  Width = 160
FEATURE [Part::Cylinder] Cylinder058
  Angle = 360
  AttacherType = Attacher::AttachEngine3D
  Height = 21
  Placement = pos=(504,85,-30) rot=(0,0,1;2.96706rad)
  Radius = 500
FEATURE [Part::Cut] Cut171  label="Cut634"
  Base = -> Box176
  Refine = true
  Tool = -> Cylinder058
FEATURE [Part::Cut] Cut170  label="Cut633"
  Base = -> Box177
  Placement = pos=(2,0,0) rot=(0,0,1;0rad)
  Refine = true
  Tool = -> Cut171
FEATURE [Part::Fillet] Fillet089
  Base = -> Cut170
  Edges = 2 edges r=3: [Edge6,Edge12]
  Placement = pos=(0,0,13) rot=(0,0,1;0rad)
FEATURE [Part::Box] Box178  label="Cube404"
  AttacherType = Attacher::AttachEngine3D
  Height = 21
  Length = 16
  Placement = pos=(6,5,-30) rot=(0,0,1;0rad)
  Width = 160
FEATURE [Part::Box] Box179  label="Cube405"
  AttacherType = Attacher::AttachEngine3D
  Height = 8
  Length = 8
  Placement = pos=(6,5,-30) rot=(0,0,1;0rad)
  Width = 160
FEATURE [Part::Cylinder] Cylinder059
  Angle = 360
  AttacherType = Attacher::AttachEngine3D
  Height = 21
  Placement = pos=(504,85,-30) rot=(0,0,1;2.96706rad)
  Radius = 500
FEATURE [Part::Cut] Cut173  label="Cut346"
  Base = -> Box178
  Refine = true
  Tool = -> Cylinder059
FEATURE [Part::Cut] Cut172  label="Cut345"
  Base = -> Box179
  Placement = pos=(0,0,21) rot=(0,0,1;0rad)
  Refine = true
  Tool = -> Cut173
FEATURE [Part::Cut] Cut174  label="Cut347"
  Base = -> Fillet087
  Refine = true
  Tool = -> Fillet088
FEATURE [Part::Fillet] Fillet090
  Base = -> Cut172
  Edges = 2 edges r=2: [Edge6,Edge13]
  Placement = pos=(0,0,-1) rot=(0,0,1;0rad)
FEATURE [Part::Cut] Cut175  label="Cut348"
  Base = -> Fillet090
  Refine = true
  Tool = -> Fillet089
FEATURE [Part::Box] Box180  label="Cube406"
  AttacherType = Attacher::AttachEngine3D
  Height = 10
  Length = 13
  Placement = pos=(0,30,-7) rot=(0,0,1;0rad)
  Width = 109
FEATURE [Part::Fillet] Fillet091
  Base = -> Box180
  Edges = 2 edges r=3: [Edge9,Edge11]
  Placement = pos=(1,0,1) rot=(0,0,1;0rad)
FEATURE [Part::Cut] Cut176  label="Cut349"
  Base = -> Cut175
  Refine = true
  Tool = -> Fillet091
FEATURE [Part::Box] Box181  label="Cube407"
  AttacherType = Attacher::AttachEngine3D
  Height = 17
  Length = 8
  Placement = pos=(0,53.5,-28) rot=(0,0,1;0rad)
  Width = 10
FEATURE [Part::Feature] Cut179  label="cab_tilt_lower002"
  Placement = pos=(15.5,45,-23) rot=(0,0,1;0rad)
  shape: bbox 4 x 120 x 28 mm, 33 faces (baked)
FEATURE [Part::Feature] Cut180  label="cab_tilt_upper002"
  Placement = pos=(15.5,45,-23) rot=(0,0,1;0rad)
  shape: bbox 5.33 x 120 x 34.16 mm, 49 faces (baked)
FEATURE [Part::Box] Box182  label="Cube408"
  AttacherType = Attacher::AttachEngine3D
  Height = 17
  Length = 8
  Placement = pos=(0,106.5,-28) rot=(0,0,1;0rad)
  Width = 10
FEATURE [Part::Cylinder] Cylinder060
  Angle = 360
  AttacherType = Attacher::AttachEngine3D
  Height = 13
  Placement = pos=(-2,58.5,-22) rot=(0,1,0;1.5708rad)
  Radius = 5
FEATURE [Part::Cylinder] Cylinder061
  Angle = 360
  AttacherType = Attacher::AttachEngine3D
  Height = 13
  Placement = pos=(-2,58.5,-22) rot=(0,1,0;1.5708rad)
  Radius = 1.6
FEATURE [Part::Cylinder] Cylinder062
  Angle = 360
  AttacherType = Attacher::AttachEngine3D
  Height = 2.5
  Placement = pos=(-2,58.5,-22) rot=(0,1,0;1.5708rad)
  Radius = 3.1
FEATURE [Part::MultiFuse] Fusion050
  Refine = true
  Shapes = -> [Cylinder062,Cylinder061]
FEATURE [Part::Cylinder] Cylinder063
  Angle = 360
  AttacherType = Attacher::AttachEngine3D
  Height = 13
  Placement = pos=(-2,58.5,-22) rot=(0,1,0;1.5708rad)
  Radius = 1.6
FEATURE [Part::Cylinder] Cylinder064
  Angle = 360
  AttacherType = Attacher::AttachEngine3D
  Height = 2.5
  Placement = pos=(-2,58.5,-22) rot=(0,1,0;1.5708rad)
  Radius = 3.1
FEATURE [Part::MultiFuse] Fusion052
  Placement = pos=(0,53,0) rot=(0,0,1;0rad)
  Refine = true
  Shapes = -> [Cylinder064,Cylinder063]
FEATURE [Part::Cylinder] Cylinder065
  Angle = 360
  AttacherType = Attacher::AttachEngine3D
  Height = 13
  Placement = pos=(-2,111.5,-22) rot=(0,1,0;1.5708rad)
  Radius = 5
FEATURE [Part::MultiFuse] Fusion053
  Refine = true
  Shapes = -> [Fusion052,Fusion050]
FEATURE [Part::MultiFuse] Fusion054
  Refine = true
  Shapes = -> [Cut174,Cut176,Box181,Box182,Cylinder060,Cylinder065]
FEATURE [Part::Cut] Cut181  label="Cut350"
  Base = -> Fusion054
  Refine = true
  Tool = -> Fusion053
FEATURE [Part::Fillet] Fillet092
  Base = -> Cut181
  Edges = 2 edges r=1: [Edge70,Edge189]
FEATURE [Part::Fillet] Fillet093
  Base = -> Fillet092
  Edges = 2 edges r=0.99: [Edge119,Edge180]
FEATURE [Part::Fillet] Fillet094
  Base = -> Fillet093
  Edges = 2 edges r=1: [Edge27,Edge225]
FEATURE [Part::Cylinder] Cylinder066
  Angle = 360
  AttacherType = Attacher::AttachEngine3D
  Height = 10
  Radius = 1.25
FEATURE [Part::Cylinder] Cylinder067
  Angle = 360
  AttacherType = Attacher::AttachEngine3D
  Height = 10
  Placement = pos=(0,4,0) rot=(0,0,1;0rad)
  Radius = 1.25
FEATURE [Part::Box] Box183  label="Cube409"
  AttacherType = Attacher::AttachEngine3D
  Height = 10
  Length = 2.5
  Placement = pos=(-1.25,0,0) rot=(0,0,1;0rad)
  Width = 4
FEATURE [Part::MultiFuse] Fusion055
  Refine = true
  Shapes = -> [Box183,Cylinder067,Cylinder066]
FEATURE [Part::Box] Box184  label="Cube410"
  AttacherType = Attacher::AttachEngine3D
  Height = 10
  Length = 2.5
  Placement = pos=(-1.25,0,0) rot=(0,0,1;0rad)
  Width = 4
FEATURE [Part::Cylinder] Cylinder068
  Angle = 360
  AttacherType = Attacher::AttachEngine3D
  Height = 10
  Placement = pos=(0,4,0) rot=(0,0,1;0rad)
  Radius = 1.25
FEATURE [Part::Cylinder] Cylinder069
  Angle = 360
  AttacherType = Attacher::AttachEngine3D
  Height = 10
  Radius = 1.25
FEATURE [Part::MultiFuse] Fusion056
  Placement = pos=(0,8,0) rot=(0,0,1;0rad)
  Refine = true
  Shapes = -> [Box184,Cylinder068,Cylinder069]
FEATURE [Part::Box] Box185  label="Cube411"
  AttacherType = Attacher::AttachEngine3D
  Height = 10
  Length = 2.5
  Placement = pos=(-1.25,0,0) rot=(0,0,1;0rad)
  Width = 4
FEATURE [Part::Cylinder] Cylinder070
  Angle = 360
  AttacherType = Attacher::AttachEngine3D
  Height = 10
  Placement = pos=(0,4,0) rot=(0,0,1;0rad)
  Radius = 1.25
FEATURE [Part::Cylinder] Cylinder071
  Angle = 360
  AttacherType = Attacher::AttachEngine3D
  Height = 10
  Radius = 1.25
FEATURE [Part::MultiFuse] Fusion057
  Placement = pos=(0,16,0) rot=(0,0,1;0rad)
  Refine = true
  Shapes = -> [Box185,Cylinder070,Cylinder071]
FEATURE [Part::Box] Box186  label="Cube412"
  AttacherType = Attacher::AttachEngine3D
  Height = 10
  Length = 2.5
  Placement = pos=(-1.25,0,0) rot=(0,0,1;0rad)
  Width = 4
FEATURE [Part::Cylinder] Cylinder072
  Angle = 360
  AttacherType = Attacher::AttachEngine3D
  Height = 10
  Placement = pos=(0,4,0) rot=(0,0,1;0rad)
  Radius = 1.25
FEATURE [Part::Cylinder] Cylinder073
  Angle = 360
  AttacherType = Attacher::AttachEngine3D
  Height = 10
  Radius = 1.25
FEATURE [Part::MultiFuse] Fusion058
  Placement = pos=(0,24,0) rot=(0,0,1;0rad)
  Refine = true
  Shapes = -> [Box186,Cylinder072,Cylinder073]
FEATURE [Part::Box] Box187  label="Cube413"
  AttacherType = Attacher::AttachEngine3D
  Height = 10
  Length = 2.5
  Placement = pos=(-1.25,0,0) rot=(0,0,1;0rad)
  Width = 4
FEATURE [Part::Cylinder] Cylinder074
  Angle = 360
  AttacherType = Attacher::AttachEngine3D
  Height = 10
  Placement = pos=(0,4,0) rot=(0,0,1;0rad)
  Radius = 1.25
FEATURE [Part::Cylinder] Cylinder075
  Angle = 360
  AttacherType = Attacher::AttachEngine3D
  Height = 10
  Radius = 1.25
FEATURE [Part::MultiFuse] Fusion059
  Placement = pos=(0,32,0) rot=(0,0,1;0rad)
  Refine = true
  Shapes = -> [Box187,Cylinder074,Cylinder075]
FEATURE [Part::MultiFuse] Fusion060
  Placement = pos=(12.5,67,-12) rot=(0,-1,0;1.0472rad)
  Refine = true
  Shapes = -> [Fusion055,Fusion057,Fusion058,Fusion056,Fusion059]
FEATURE [Part::Cut] Cut182  label="bumper-00"
  Base = -> Fillet094
  Placement = pos=(0,0,-1) rot=(0,0,1;0rad)
  Refine = true
  Tool = -> Fusion060
FEATURE [Part::MultiFuse] Fusion061
  Refine = true
  Shapes = -> [Fillet064,Box147,Part__Mirroring,Fusion029,Fillet063]
FEATURE [Part::Box] Box188  label="Cube414"
  AttacherType = Attacher::AttachEngine3D
  Height = 116
  Length = 66.5
  Placement = pos=(14.5,0,-0.5) rot=(0,0,1;0rad)
  Width = 180
FEATURE [Part::Box] Box189  label="Cube416"
  AttacherType = Attacher::AttachEngine3D
  Height = 117
  Length = 67.5
  Placement = pos=(14,0,-1) rot=(0,0,1;0rad)
  Width = 180
FEATURE [Part::Box] Box190  label="Cube415"
  AttacherType = Attacher::AttachEngine3D
  Height = 116
  Length = 67
  Placement = pos=(-53.2,0,65) rot=(0,1,0;0.218166rad)
  Width = 180
FEATURE [Part::Cut] Cut185  label="Cut636"
  Base = -> Box188
  Placement = pos=(0,-2,0) rot=(0,0,1;0rad)
  Refine = true
  Tool = -> Box190
FEATURE [Part::Box] Box191  label="Cube417"
  AttacherType = Attacher::AttachEngine3D
  Height = 116
  Length = 67
  Placement = pos=(-53.7,0,65) rot=(0,1,0;0.218166rad)
  Width = 180
FEATURE [Part::Cut] Cut184  label="Cut635"
  Base = -> Box189
  Placement = pos=(0,-2,0) rot=(0,0,1;0rad)
  Refine = true
  Tool = -> Box191
FEATURE [Part::Cut] Cut186
  Base = -> Cut091
  Refine = true
  Tool = -> Fusion061
FEATURE [Part::Cut] Cut187  label="doors-cut-01"
  Base = -> Cut184
  Placement = pos=(0.5,-3,0.5) rot=(0,0,1;0rad)
  Refine = true
  Tool = -> Cut185
FEATURE [Part::Cut] Cut188  label="Cut637"
  Base = -> Cut186
  Refine = true
  Tool = -> Fillet050
FEATURE [Part::Box] Box192  label="Cube418"
  AttacherType = Attacher::AttachEngine3D
  Height = 116
  Length = 67
  Placement = pos=(-53.2,0,65) rot=(0,1,0;0.218166rad)
  Width = 180
FEATURE [Part::Box] Box193  label="Cube419"
  AttacherType = Attacher::AttachEngine3D
  Height = 116
  Length = 67
  Placement = pos=(-53.7,0,65) rot=(0,1,0;0.218166rad)
  Width = 180
FEATURE [Part::Box] Box194  label="Cube420"
  AttacherType = Attacher::AttachEngine3D
  Height = 117
  Length = 67.5
  Placement = pos=(14,0,-1) rot=(0,0,1;0rad)
  Width = 180
FEATURE [Part::Cut] Cut190  label="Cut638"
  Base = -> Box194
  Placement = pos=(0,-2,0) rot=(0,0,1;0rad)
  Refine = true
  Tool = -> Box193
FEATURE [Part::Box] Box195  label="Cube421"
  AttacherType = Attacher::AttachEngine3D
  Height = 116
  Length = 66.5
  Placement = pos=(14.5,0,-0.5) rot=(0,0,1;0rad)
  Width = 180
FEATURE [Part::Cut] Cut191  label="Cut639"
  Base = -> Box195
  Placement = pos=(0,-2,0) rot=(0,0,1;0rad)
  Refine = true
  Tool = -> Box192
FEATURE [Part::Cut] Cut189  label="doors-cut-00"
  Base = -> Cut190
  Placement = pos=(0.5,-3,0.5) rot=(0,0,1;0rad)
  Refine = true
  Tool = -> Cut191
FEATURE [Part::Fillet] Fillet095
  Base = -> Cut188
  Edges = 4 edges r=3: [Edge209,Edge210,Edge211,Edge212]
FEATURE [Part::Cut] Cut192  label="Cut640"
  Base = -> Fillet095
  Refine = true
  Tool = -> Fillet066
FEATURE [Part::Box] Box196  label="Cube422"
  AttacherType = Attacher::AttachEngine3D
  Height = 64
  Length = 21
  Width = 164
FEATURE [Part::Fillet] Fillet096
  Base = -> Box196
  Edges = 2 edges r=18: [Edge1,Edge3]
  Placement = pos=(7,3,0) rot=(0,0,1;0rad)
FEATURE [Part::Cut] Cut193  label="Cut641"
  Base = -> Fillet010
  Refine = true
  Tool = -> Fillet096
FEATURE [Part::MultiFuse] Fusion062
  Refine = true
  Shapes = -> [Chamfer019,Cut193]
FEATURE [Part::Cut] Cut194  label="Cut642"
  Base = -> Fusion062
  Refine = true
  Tool = -> Cut064
FEATURE [Part::Cut] Cut195  label="Cut643"
  Base = -> Cut194
  Refine = true
  Tool = -> Fillet062
FEATURE [Part::Cut] Cut196  label="Cut644"
  Base = -> Cut195
  Refine = true
  Tool = -> Fillet055
FEATURE [Part::Cut] Cut197  label="Cut645"
  Base = -> Cut196
  Refine = true
  Tool = -> Fusion042
FEATURE [Part::Fillet] Fillet097
  Base = -> Cut197
  Edges = 2 edges r=3: [Edge74,Edge149]
FEATURE [Part::Box] Box197  label="Cube423"
  AttacherType = Attacher::AttachEngine3D
  Height = 2
  Length = 117
  Placement = pos=(6,3,54) rot=(0,0,1;0rad)
  Width = 164
FEATURE [Part::Fillet] Fillet098
  Base = -> Box197
  Edges = 2 edges r=15: [Edge1,Edge3]
FEATURE [Part::Fillet] Fillet099
  Base = -> Fillet098
  Edges = 2 edges r=6: [Edge17,Edge18]
FEATURE [Part::Box] Box198  label="Cube424"
  AttacherType = Attacher::AttachEngine3D
  Height = 2
  Length = 111
  Placement = pos=(6,3,54) rot=(0,0,1;0rad)
  Width = 158
FEATURE [Part::Fillet] Fillet101
  Base = -> Box198
  Edges = 2 edges r=12: [Edge1,Edge3]
FEATURE [Part::Fillet] Fillet100
  Base = -> Fillet101
  Edges = 2 edges r=3: [Edge17,Edge18]
  Placement = pos=(3,3,0) rot=(0,0,1;0rad)
FEATURE [Part::Cut] Cut198  label="Cut646"
  Base = -> Fillet099
  Placement = pos=(0,0,8) rot=(0,0,1;0rad)
  Refine = true
  Tool = -> Fillet100
FEATURE [Part::MultiFuse] Fusion063
  Refine = true
  Shapes = -> [Cut198,Fillet097]
FEATURE [Part::Cut] Cut199  label="Cut647"
  Base = -> Cut192
  Refine = true
  Tool = -> Cut187
FEATURE [Part::Cut] Cut200  label="cab-lower-part-00"
  Base = -> Fusion063
  Refine = true
  Tool = -> Cut189
FEATURE [Part::Box] Box203  label="Cube429"
  AttacherType = Attacher::AttachEngine3D
  Height = 58
  Length = 2.5
  Placement = pos=(0,10,0) rot=(0,0,1;0rad)
  Width = 0.5
FEATURE [Part::Box] Box204  label="Cube430"
  AttacherType = Attacher::AttachEngine3D
  Height = 58
  Length = 2.5
  Placement = pos=(0,159.5,0) rot=(0,0,1;0rad)
  Width = 0.5
FEATURE [Part::MultiFuse] Fusion065
  Refine = true
  Shapes = -> [Box204,Box203]
FEATURE [Part::Cylinder] Cylinder076
  Angle = 53
  AttacherType = Attacher::AttachEngine3D
  Height = 10
  Placement = pos=(13,13,0) rot=(0,0,1;3.38594rad)
  Radius = 12.6
FEATURE [Part::Cylinder] Cylinder077
  Angle = 360
  AttacherType = Attacher::AttachEngine3D
  Height = 10
  Placement = pos=(13,13,0) rot=(0,0,1;3.38594rad)
  Radius = 10
FEATURE [Part::Box] Box208  label="Cube434"
  AttacherType = Attacher::AttachEngine3D
  Height = 4
  Length = 10
  Placement = pos=(100,-19,13) rot=(0,0,1;0.139626rad)
  Width = 4
FEATURE [Part::Box] Box209  label="Cube435"
  AttacherType = Attacher::AttachEngine3D
  Height = 4
  Length = 10
  Placement = pos=(100,-19,13) rot=(0,0,1;0.139626rad)
  Width = 4
FEATURE [Part::Mirroring] Part__Mirroring010  label="Cube432 (Mirror #9)001"
  Base = (0,0,0)
  Normal = (1,0,0)
  Placement = pos=(200,0,0) rot=(0,0,1;0rad)
  Source = -> Box209
FEATURE [Part::Box] Box210  label="Cube436"
  AttacherType = Attacher::AttachEngine3D
  Height = 4
  Length = 10
  Placement = pos=(95,-15,13) rot=(0,0,1;0rad)
  Width = 4
FEATURE [Part::MultiFuse] Fusion068
  Refine = true
  Shapes = -> [Part__Mirroring010,Box208]
FEATURE [Part::Cut] Cut208  label="Cut648"
  Base = -> Box210
  Refine = true
  Tool = -> Fusion068
FEATURE [Part::Fillet] Fillet114
  Base = -> Cut208
  Edges = 3 edges r=0.5: [Edge4,Edge14,Edge15]
FEATURE [Part::Fillet] Fillet113
  Base = -> Fillet114
  Edges = 4 edges r=0.5: [Edge7,Edge11,Edge16,Edge20]
  Placement = pos=(-2,6,2) rot=(0,0,1;0rad)
FEATURE [Part::Mirroring] Part__Mirroring011  label="Fillet113 (Mirror #11)"
  Base = (0,0,0)
  Normal = (0,1,0)
  Placement = pos=(0,170,0) rot=(0,0,1;0rad)
  Source = -> Fillet113
FEATURE [Part::Box] Box211  label="Cube437"
  AttacherType = Attacher::AttachEngine3D
  Height = 1
  Length = 96
  Placement = pos=(26,4,116.5) rot=(0,0,1;0rad)
  Width = 162
FEATURE [Part::Box] Box212  label="Cube438"
  AttacherType = Attacher::AttachEngine3D
  Height = 1
  Length = 94
  Placement = pos=(26,6,116.5) rot=(0,0,1;0rad)
  Width = 158
FEATURE [Part::Fillet] Fillet115
  Base = -> Box212
  Edges = 2 edges r=4: [Edge5,Edge7]
FEATURE [Part::Fillet] Fillet116
  Base = -> Box211
  Edges = 2 edges r=6: [Edge5,Edge7]
FEATURE [Part::Fillet] Fillet117
  Base = -> Fillet116
  Edges = 2 edges r=2: [Edge17,Edge18]
FEATURE [Part::Cut] Cut209  label="Cut649"
  Base = -> Fillet117
  Refine = true
  Tool = -> Fillet115
FEATURE [Part::MultiFuse] Fusion071
  Refine = true
  Shapes = -> [Cut199,Cut209]
FEATURE [Part::Box] Box213  label="Cube439"
  AttacherType = Attacher::AttachEngine3D
  Height = 6.5
  Length = 110
  Placement = pos=(19,4,121.5) rot=(0,0,1;0rad)
  Width = 162
FEATURE [Part::Box] Box215  label="Cube441"
  AttacherType = Attacher::AttachEngine3D
  Height = 5.1
  Length = 100
  Placement = pos=(19.5,5.5,122.5) rot=(0,0,1;0rad)
  Width = 159
FEATURE [Part::Fillet] Fillet120
  Base = -> Box215
  Edges = 2 edges r=10: [Edge1,Edge3]
FEATURE [Part::Fillet] Fillet121
  Base = -> Fillet120
  Edges = 2 edges r=4.5: [Edge17,Edge18]
FEATURE [Part::Fillet] Fillet122
  Base = -> Fillet121
  Edges = 4 edges r=5: [Edge1,Edge4,Edge5,Edge8]
  Placement = pos=(0.7,0,-2) rot=(0,0,1;0rad)
FEATURE [Part::Cylinder] Cylinder080
  Angle = 360
  AttacherType = Attacher::AttachEngine3D
  Height = 10
  Placement = pos=(15,15,48) rot=(0,0,1;0rad)
  Radius = 15
FEATURE [Part::Cylinder] Cylinder081
  Angle = 360
  AttacherType = Attacher::AttachEngine3D
  Height = 10
  Placement = pos=(15,15,10) rot=(0,0,1;0rad)
  Radius = 13
FEATURE [Part::Cylinder] Cylinder082
  Angle = 360
  AttacherType = Attacher::AttachEngine3D
  Height = 42
  Placement = pos=(15,15,13) rot=(0,0,1;3.49066rad)
  Radius = 20
FEATURE [Part::Cylinder] Cylinder083
  Angle = 360
  AttacherType = Attacher::AttachEngine3D
  Height = 31
  Placement = pos=(15,15,19) rot=(0,0,1;3.49066rad)
  Radius = 18.5
FEATURE [Part::Cylinder] Cylinder084
  Angle = 360
  AttacherType = Attacher::AttachEngine3D
  Height = 3
  Placement = pos=(15,15,10) rot=(0,0,1;3.49066rad)
  Radius = 15
FEATURE [Part::Cylinder] Cylinder085
  Angle = 360
  AttacherType = Attacher::AttachEngine3D
  Height = 3
  Placement = pos=(15,15,55) rot=(0,0,1;3.49066rad)
  Radius = 17
FEATURE [Part::MultiFuse] Fusion074
  Refine = true
  Shapes = -> [Cylinder080,Cylinder081]
FEATURE [Part::Box] Box216  label="Cube442"
  AttacherType = Attacher::AttachEngine3D
  Height = 48
  Length = 10
  Placement = pos=(-4,5,10) rot=(0,0,1;0.785398rad)
  Width = 30
FEATURE [Part::Box] Box217  label="Cube443"
  AttacherType = Attacher::AttachEngine3D
  Height = 6
  Length = 10
  Placement = pos=(-4,10,10) rot=(0,0,1;0rad)
  Width = 2
FEATURE [Part::Cut] Cut245  label="Cut650"
  Base = -> Fusion071
  Refine = true
  Tool = -> Box213
FEATURE [Part::Fillet] Fillet123
  Base = -> Cut245
  Edges = 3 edges r=1.49: [Edge7,Edge21,Edge25]
FEATURE [Part::Box] Box220  label="Cube446"
  AttacherType = Attacher::AttachEngine3D
  Height = 5.1
  Length = 95
  Placement = pos=(23,7.5,122.5) rot=(0,0,1;0rad)
  Width = 155
FEATURE [Part::Fillet] Fillet124
  Base = -> Box220
  Edges = 2 edges r=3: [Edge5,Edge7]
FEATURE [Part::Fillet] Fillet125
  Base = -> Fillet124
  Edges = 2 edges r=8: [Edge17,Edge18]
FEATURE [Part::Fillet] Fillet126
  Base = -> Fillet125
  Edges = 1 edges r=4: [Edge4]
  Placement = pos=(0,0,-4) rot=(0,0,1;0rad)
FEATURE [Part::Cut] Cut246  label="Cut651"
  Base = -> Fillet122
  Refine = true
  Tool = -> Fillet126
FEATURE [Part::Box] Box221  label="Cube447"
  AttacherType = Attacher::AttachEngine3D
  Height = 1.5
  Length = 2
  Placement = pos=(0,65,14.5) rot=(0,0,1;0rad)
  Width = 36
FEATURE [Part::Box] Box222  label="Cube448"
  AttacherType = Attacher::AttachEngine3D
  Height = 1.5
  Length = 2
  Placement = pos=(0,68,18.5) rot=(0,0,1;0rad)
  Width = 33
FEATURE [Part::MultiFuse] Fusion094  label="iveco-logo_00"
  Refine = true
  Shapes = -> [Extrude,Box221,Box222]
FEATURE [Part::Cylinder] Cylinder133
  Angle = 360
  AttacherType = Attacher::AttachEngine3D
  Height = 4
  Placement = pos=(2,34,15) rot=(0,1,0;1.5708rad)
  Radius = 2.5
FEATURE [Part::Cylinder] Cylinder134
  Angle = 360
  AttacherType = Attacher::AttachEngine3D
  Height = 4
  Placement = pos=(2,34,15) rot=(0,1,0;1.5708rad)
  Radius = 0.9
FEATURE [Part::Cylinder] Cylinder135
  Angle = 360
  AttacherType = Attacher::AttachEngine3D
  Height = 7
  Placement = pos=(2,34,15) rot=(0,1,0;1.5708rad)
  Radius = 1.2
FEATURE [Part::Cylinder] Cylinder136
  Angle = 360
  AttacherType = Attacher::AttachEngine3D
  Height = 4
  Placement = pos=(2,34,15) rot=(0,1,0;1.5708rad)
  Radius = 2.7
FEATURE [Part::Cut] Cut247  label="Cut652"
  Base = -> Cylinder133
  Refine = true
  Tool = -> Cylinder134
FEATURE [Part::MultiFuse] Fusion095
  Refine = true
  Shapes = -> [Cylinder135,Cylinder136]
FEATURE [Part::Cylinder] Cylinder137
  Angle = 360
  AttacherType = Attacher::AttachEngine3D
  Height = 4
  Placement = pos=(2,34,15) rot=(0,1,0;1.5708rad)
  Radius = 2.5
FEATURE [Part::Cylinder] Cylinder138
  Angle = 360
  AttacherType = Attacher::AttachEngine3D
  Height = 4
  Placement = pos=(2,34,15) rot=(0,1,0;1.5708rad)
  Radius = 0.9
FEATURE [Part::Cut] Cut248  label="Cut653"
  Base = -> Cylinder137
  Placement = pos=(0,102,0) rot=(0,0,1;0rad)
  Refine = true
  Tool = -> Cylinder138
FEATURE [Part::Cylinder] Cylinder139
  Angle = 360
  AttacherType = Attacher::AttachEngine3D
  Height = 4
  Placement = pos=(2,34,15) rot=(0,1,0;1.5708rad)
  Radius = 2.7
FEATURE [Part::Cylinder] Cylinder140
  Angle = 360
  AttacherType = Attacher::AttachEngine3D
  Height = 7
  Placement = pos=(2,34,15) rot=(0,1,0;1.5708rad)
  Radius = 1.2
FEATURE [Part::MultiFuse] Fusion096
  Placement = pos=(0,102,0) rot=(0,0,1;0rad)
  Refine = true
  Shapes = -> [Cylinder140,Cylinder139]
FEATURE [Part::MultiFuse] Fusion097
  Refine = true
  Shapes = -> [Cut247,Cut248]
FEATURE [Part::MultiFuse] Fusion098
  Refine = true
  Shapes = -> [Fusion095,Fusion096]
FEATURE [Part::MultiFuse] Fusion099  label="radiator-grid-01"
  Refine = true
  Shapes = -> [Cut102,Fusion097]
FEATURE [Part::Cut] Cut252  label="Cut654"
  Base = -> Cylinder082
  Refine = true
  Tool = -> Cylinder083
FEATURE [Part::MultiFuse] Fusion106
  Refine = true
  Shapes = -> [Cylinder085,Cylinder084,Cut252]
FEATURE [Part::Cut] Cut253  label="Cut655"
  Base = -> Fusion106
  Refine = true
  Tool = -> Fusion074
FEATURE [Part::MultiFuse] Fusion107
  Refine = true
  Shapes = -> [Box217,Box216]
FEATURE [Part::Chamfer] Chamfer032
  Base = -> Cut253
  Edges = 1 edges r=4.99: [Edge32]
FEATURE [Part::Chamfer] Chamfer033
  Base = -> Chamfer032
  Edges = 1 edges r=5.49: [Edge33]
FEATURE [Part::Chamfer] Chamfer034
  Base = -> Chamfer033
  Edges = 1 edges r=2.99: [Edge36]
FEATURE [Part::Chamfer] Chamfer035
  Base = -> Chamfer034
  Edges = 1 edges r=3.49: [Edge36]
FEATURE [Part::Cut] Cut254
  Base = -> Chamfer035
  Refine = true
  Tool = -> Fusion107
FEATURE [Part::Chamfer] Chamfer036  label="left-deflector"
  Base = -> Cut254
  Edges = 1 edges r=0.9: [Edge25]
FEATURE [Part::Fillet] Fillet127
  Base = -> Cut200
  Edges = 2 edges r=4: [Edge286,Edge354]
FEATURE [Part::Cylinder] Cylinder149
  Angle = 360
  AttacherType = Attacher::AttachEngine3D
  Height = 13.5
  Placement = pos=(11.9886,10.7385,16) rot=(0.884029,-0.330525,-0.330525;1.69375rad)
  Radius = 2
FEATURE [Part::Cylinder] Cylinder150
  Angle = 360
  AttacherType = Attacher::AttachEngine3D
  Height = 10
  Placement = pos=(15,15,13) rot=(0,0,1;0rad)
  Radius = 13
FEATURE [Part::Cylinder] Cylinder151
  Angle = 360
  AttacherType = Attacher::AttachEngine3D
  Height = 10
  Placement = pos=(15,15,48) rot=(0,0,1;0rad)
  Radius = 15
FEATURE [Part::Cylinder] Cylinder152
  Angle = 360
  AttacherType = Attacher::AttachEngine3D
  Height = 10
  Placement = pos=(15,15,13) rot=(0,0,1;0rad)
  Radius = 19.9
FEATURE [Part::Cylinder] Cylinder153
  Angle = 360
  AttacherType = Attacher::AttachEngine3D
  Height = 13.5
  Placement = pos=(11.9886,10.7385,16) rot=(0.884029,-0.330525,-0.330525;1.69375rad)
  Radius = 2
FEATURE [Part::Chamfer] Chamfer037
  Base = -> Cylinder152
  Edges = 1 edges r=4.99: [Edge3]
FEATURE [Part::Cut] Cut256
  Base = -> Cylinder153
  Refine = true
  Tool = -> Chamfer037
FEATURE [Part::Cut] Cut257
  Base = -> Cylinder149
  Refine = true
  Tool = -> Cut256
FEATURE [Part::Cut] Cut258  label="Cut656"
  Base = -> Cut257
  Refine = true
  Tool = -> Cylinder150
FEATURE [Part::Cylinder] Cylinder154
  Angle = 360
  AttacherType = Attacher::AttachEngine3D
  Height = 11.5
  Placement = pos=(11.9886,10.7385,16) rot=(0.884029,-0.330525,-0.330525;1.69375rad)
  Radius = 0.9
FEATURE [Part::Cylinder] Cylinder155
  Angle = 360
  AttacherType = Attacher::AttachEngine3D
  Height = 11.5
  Placement = pos=(11.9886,10.7385,51) rot=(0.884029,-0.330525,-0.330525;1.69375rad)
  Radius = 0.9
FEATURE [Part::Cylinder] Cylinder156
  Angle = 360
  AttacherType = Attacher::AttachEngine3D
  Height = 13.5
  Placement = pos=(11.9886,10.7385,51) rot=(0.884029,-0.330525,-0.330525;1.69375rad)
  Radius = 2
FEATURE [Part::Cut] Cut259  label="Cut657"
  Base = -> Cylinder156
  Refine = true
  Tool = -> Cylinder151
FEATURE [Part::MultiFuse] Fusion108
  Refine = true
  Shapes = -> [Cylinder154,Cylinder155]
FEATURE [Part::MultiFuse] Fusion109
  Refine = true
  Shapes = -> [Cut259,Cut258]
FEATURE [Part::MultiFuse] Fusion110
  Refine = true
  Shapes = -> [Chamfer036,Fusion109]
FEATURE [Part::Cylinder] Cylinder157
  Angle = 360
  AttacherType = Attacher::AttachEngine3D
  Height = 11.5
  Placement = pos=(11.9886,10.7385,16) rot=(0.884029,-0.330525,-0.330525;1.69375rad)
  Radius = 1.2
FEATURE [Part::Cylinder] Cylinder158
  Angle = 360
  AttacherType = Attacher::AttachEngine3D
  Height = 11.5
  Placement = pos=(11.9886,10.7385,51) rot=(0.884029,-0.330525,-0.330525;1.69375rad)
  Radius = 1.2
FEATURE [Part::MultiFuse] Fusion111
  Refine = true
  Shapes = -> [Cylinder157,Cylinder158]
FEATURE [Part::Cut] Cut260  label="left-deflector_01"
  Base = -> Fusion110
  Refine = true
  Tool = -> Fusion108
FEATURE [Part::Cylinder] Cylinder159
  Angle = 360
  AttacherType = Attacher::AttachEngine3D
  Height = 11.5
  Placement = pos=(11.9886,10.7385,51) rot=(0.884029,-0.330525,-0.330525;1.69375rad)
  Radius = 1.2
FEATURE [Part::Cylinder] Cylinder160
  Angle = 360
  AttacherType = Attacher::AttachEngine3D
  Height = 11.5
  Placement = pos=(11.9886,10.7385,16) rot=(0.884029,-0.330525,-0.330525;1.69375rad)
  Radius = 1.2
FEATURE [Part::MultiFuse] Fusion112
  Refine = true
  Shapes = -> [Cylinder160,Cylinder159]
FEATURE [Part::Mirroring] Part__Mirroring012  label="Fusion111 (Mirror #12)"
  Base = (0,0,0)
  Normal = (0,1,0)
  Placement = pos=(0,170,0) rot=(0,0,1;0rad)
  Source = -> Fusion111
FEATURE [Part::MultiFuse] Fusion115
  Refine = true
  Shapes = -> [Fusion112,Part__Mirroring012]
FEATURE [Part::Cut] Cut261  label="Cut658"
  Base = -> Fillet127
  Refine = true
  Tool = -> Fusion098
FEATURE [Part::Cut] Cut262  label="cab-lower-part-01"
  Base = -> Cut261
  Refine = true
  Tool = -> Fusion115
FEATURE [Part::Cylinder] Cylinder165
  Angle = 360
  AttacherType = Attacher::AttachEngine3D
  Height = 3
  Placement = pos=(15,15,55) rot=(0,0,1;3.49066rad)
  Radius = 17
FEATURE [Part::Cylinder] Cylinder166
  Angle = 360
  AttacherType = Attacher::AttachEngine3D
  Height = 3
  Placement = pos=(15,15,10) rot=(0,0,1;3.49066rad)
  Radius = 15
FEATURE [Part::Cylinder] Cylinder167
  Angle = 360
  AttacherType = Attacher::AttachEngine3D
  Height = 42
  Placement = pos=(15,15,13) rot=(0,0,1;3.49066rad)
  Radius = 20
FEATURE [Part::Cylinder] Cylinder168
  Angle = 360
  AttacherType = Attacher::AttachEngine3D
  Height = 31
  Placement = pos=(15,15,19) rot=(0,0,1;3.49066rad)
  Radius = 18.5
FEATURE [Part::Cut] Cut267  label="Cut661"
  Base = -> Cylinder167
  Refine = true
  Tool = -> Cylinder168
FEATURE [Part::MultiFuse] Fusion118
  Refine = true
  Shapes = -> [Cylinder165,Cylinder166,Cut267]
FEATURE [Part::Cylinder] Cylinder169
  Angle = 360
  AttacherType = Attacher::AttachEngine3D
  Height = 10
  Placement = pos=(15,15,48) rot=(0,0,1;0rad)
  Radius = 15
FEATURE [Part::Cylinder] Cylinder170
  Angle = 360
  AttacherType = Attacher::AttachEngine3D
  Height = 10
  Placement = pos=(15,15,10) rot=(0,0,1;0rad)
  Radius = 13
FEATURE [Part::MultiFuse] Fusion119
  Refine = true
  Shapes = -> [Cylinder169,Cylinder170]
FEATURE [Part::Cut] Cut266  label="Cut660"
  Base = -> Fusion118
  Refine = true
  Tool = -> Fusion119
FEATURE [Part::Chamfer] Chamfer042
  Base = -> Cut266
  Edges = 1 edges r=4.99: [Edge32]
FEATURE [Part::Chamfer] Chamfer041
  Base = -> Chamfer042
  Edges = 1 edges r=5.49: [Edge33]
FEATURE [Part::Chamfer] Chamfer040
  Base = -> Chamfer041
  Edges = 1 edges r=2.99: [Edge36]
FEATURE [Part::Chamfer] Chamfer039
  Base = -> Chamfer040
  Edges = 1 edges r=3.49: [Edge36]
FEATURE [Part::Box] Box223  label="Cube449"
  AttacherType = Attacher::AttachEngine3D
  Height = 6
  Length = 10
  Placement = pos=(-4,10,10) rot=(0,0,1;0rad)
  Width = 2
FEATURE [Part::Box] Box224  label="Cube450"
  AttacherType = Attacher::AttachEngine3D
  Height = 48
  Length = 10
  Placement = pos=(-4,5,10) rot=(0,0,1;0.785398rad)
  Width = 30
FEATURE [Part::MultiFuse] Fusion120
  Refine = true
  Shapes = -> [Box223,Box224]
FEATURE [Part::Cut] Cut265  label="Cut659"
  Base = -> Chamfer039
  Refine = true
  Tool = -> Fusion120
FEATURE [Part::Chamfer] Chamfer038  label="left-deflector001"
  Base = -> Cut265
  Edges = 1 edges r=0.9: [Edge25]
FEATURE [Part::Cylinder] Cylinder171
  Angle = 360
  AttacherType = Attacher::AttachEngine3D
  Height = 13.5
  Placement = pos=(11.9886,10.7385,51) rot=(0.884029,-0.330525,-0.330525;1.69375rad)
  Radius = 2
FEATURE [Part::Cylinder] Cylinder172
  Angle = 360
  AttacherType = Attacher::AttachEngine3D
  Height = 10
  Placement = pos=(15,15,48) rot=(0,0,1;0rad)
  Radius = 15
FEATURE [Part::Cut] Cut268  label="Cut662"
  Base = -> Cylinder171
  Refine = true
  Tool = -> Cylinder172
FEATURE [Part::Cylinder] Cylinder173
  Angle = 360
  AttacherType = Attacher::AttachEngine3D
  Height = 13.5
  Placement = pos=(11.9886,10.7385,16) rot=(0.884029,-0.330525,-0.330525;1.69375rad)
  Radius = 2
FEATURE [Part::Cylinder] Cylinder174
  Angle = 360
  AttacherType = Attacher::AttachEngine3D
  Height = 13.5
  Placement = pos=(11.9886,10.7385,16) rot=(0.884029,-0.330525,-0.330525;1.69375rad)
  Radius = 2
FEATURE [Part::Cylinder] Cylinder175
  Angle = 360
  AttacherType = Attacher::AttachEngine3D
  Height = 10
  Placement = pos=(15,15,13) rot=(0,0,1;0rad)
  Radius = 19.9
FEATURE [Part::Chamfer] Chamfer043
  Base = -> Cylinder175
  Edges = 1 edges r=4.99: [Edge3]
FEATURE [Part::Cut] Cut271  label="Cut665"
  Base = -> Cylinder174
  Refine = true
  Tool = -> Chamfer043
FEATURE [Part::Cut] Cut270  label="Cut664"
  Base = -> Cylinder173
  Refine = true
  Tool = -> Cut271
FEATURE [Part::Cylinder] Cylinder176
  Angle = 360
  AttacherType = Attacher::AttachEngine3D
  Height = 10
  Placement = pos=(15,15,13) rot=(0,0,1;0rad)
  Radius = 13
FEATURE [Part::Cut] Cut269  label="Cut663"
  Base = -> Cut270
  Refine = true
  Tool = -> Cylinder176
FEATURE [Part::MultiFuse] Fusion121
  Refine = true
  Shapes = -> [Cut268,Cut269]
FEATURE [Part::MultiFuse] Fusion117
  Refine = true
  Shapes = -> [Chamfer038,Fusion121]
FEATURE [Part::Cylinder] Cylinder177
  Angle = 360
  AttacherType = Attacher::AttachEngine3D
  Height = 11.5
  Placement = pos=(11.9886,10.7385,16) rot=(0.884029,-0.330525,-0.330525;1.69375rad)
  Radius = 0.9
FEATURE [Part::Cylinder] Cylinder178
  Angle = 360
  AttacherType = Attacher::AttachEngine3D
  Height = 11.5
  Placement = pos=(11.9886,10.7385,51) rot=(0.884029,-0.330525,-0.330525;1.69375rad)
  Radius = 0.9
FEATURE [Part::MultiFuse] Fusion122
  Refine = true
  Shapes = -> [Cylinder177,Cylinder178]
FEATURE [Part::Cut] Cut264  label="left-deflector_002"
  Base = -> Fusion117
  Refine = true
  Tool = -> Fusion122
FEATURE [Part::MultiFuse] Fusion123
  Refine = true
  Shapes = -> [Part__Mirroring011,Box009,Cut134]
FEATURE [Part::Cut] Cut272  label="Cut666"
  Base = -> Fusion123
  Refine = true
  Tool = -> Box134
FEATURE [Part::Fillet] Fillet128
  Base = -> Cut272
  Edges = 1 edges r=1: [Edge14]
FEATURE [Part::Cut] Cut273  label="Cut667"
  Base = -> Box010
  Refine = true
  Tool = -> Cylinder012
FEATURE [Part::Cut] Cut274  label="Cut668"
  Base = -> Cut273
  Refine = true
  Tool = -> Cut108
FEATURE [Part::Cut] Cut275  label="Cut669"
  Base = -> Cut274
  Refine = true
  Tool = -> Box106
FEATURE [Part::Box] Box225  label="Cube451"
  AttacherType = Attacher::AttachEngine3D
  Height = 20
  Length = 33
  Placement = pos=(15,156,-31) rot=(0,0,1;0rad)
  Width = 14
FEATURE [Part::Cylinder] Cylinder179
  Angle = 360
  AttacherType = Attacher::AttachEngine3D
  Height = 22
  Placement = pos=(98,174,-23) rot=(1,0,0;1.5708rad)
  Radius = 52
FEATURE [Part::Box] Box226  label="Cube452"
  AttacherType = Attacher::AttachEngine3D
  Height = 9
  Length = 5
  Placement = pos=(46,152,-32) rot=(0,0,1;0rad)
  Width = 22
FEATURE [Part::MultiFuse] Fusion
  Refine = true
  Shapes = -> [Cylinder179,Box226]
FEATURE [Part::Cut] Cut276  label="Cut670"
  Base = -> Box225
  Refine = true
  Tool = -> Fusion
FEATURE [Part::MultiFuse] Fusion124
  Refine = true
  Shapes = -> [Cylinder013,Box104]
FEATURE [Part::Cut] Cut277  label="Cut671"
  Base = -> Box011
  Refine = true
  Tool = -> Fusion124
FEATURE [Part::Cut] Cut278  label="Cut672"
  Base = -> Cut276
  Refine = true
  Tool = -> Cut277
FEATURE [Part::Box] Box227  label="Cube453"
  AttacherType = Attacher::AttachEngine3D
  Height = 2
  Length = 33
  Placement = pos=(15,156,-31) rot=(0,0,1;0rad)
  Width = 14
FEATURE [Part::Box] Box228  label="Cube454"
  AttacherType = Attacher::AttachEngine3D
  Height = 20
  Length = 33
  Placement = pos=(15,169,-29) rot=(0,0,1;0rad)
  Width = 3
FEATURE [Part::Cut] Cut279  label="Cut673"
  Base = -> Box228
  Refine = true
  Tool = -> Box227
FEATURE [Part::Cut] Cut280  label="Cut674"
  Base = -> Cut278
  Refine = true
  Tool = -> Cut279
FEATURE [Part::Box] Box229  label="Cube455"
  AttacherType = Attacher::AttachEngine3D
  Height = 12
  Length = 28
  Placement = pos=(17,165,-24) rot=(-1,0,0;0.279253rad)
  Width = 3
FEATURE [Part::Cylinder] Cylinder180
  Angle = 360
  AttacherType = Attacher::AttachEngine3D
  Height = 22
  Placement = pos=(98,174,-23) rot=(1,0,0;1.5708rad)
  Radius = 54
FEATURE [Part::Box] Box230  label="Cube456"
  AttacherType = Attacher::AttachEngine3D
  Height = 9
  Length = 5
  Placement = pos=(44,152,-32) rot=(0,0,1;0rad)
  Width = 22
FEATURE [Part::MultiFuse] Fusion125
  Refine = true
  Shapes = -> [Cylinder180,Box230]
FEATURE [Part::Cut] Cut281  label="Cut675"
  Base = -> Box229
  Placement = pos=(0,1,0) rot=(0,0,1;0rad)
  Refine = true
  Tool = -> Fusion125
FEATURE [Part::Cut] Cut282  label="Cut676"
  Base = -> Cut280
  Refine = true
  Tool = -> Cut281
FEATURE [Part::Box] Box231  label="Cube457"
  AttacherType = Attacher::AttachEngine3D
  Height = 23
  Length = 37
  Placement = pos=(15,152,-23) rot=(0,0,1;0rad)
  Width = 18
FEATURE [Part::Cylinder] Cylinder
  Angle = 360
  AttacherType = Attacher::AttachEngine3D
  Height = 22
  Placement = pos=(98,174,-23) rot=(1,0,0;1.5708rad)
  Radius = 52
FEATURE [Part::Cut] Cut285  label="Cut679"
  Base = -> Box231
  Refine = true
  Tool = -> Cylinder
FEATURE [Part::Box] Box232  label="Cube458"
  AttacherType = Attacher::AttachEngine3D
  Height = 18
  Length = 31
  Placement = pos=(17,158,-20) rot=(0,0,1;0rad)
  Width = 12
FEATURE [Part::Cylinder] Cylinder181
  Angle = 360
  AttacherType = Attacher::AttachEngine3D
  Height = 22
  Placement = pos=(98,174,-23) rot=(1,0,0;1.5708rad)
  Radius = 54
FEATURE [Part::Cut] Cut286  label="Cut680"
  Base = -> Box232
  Refine = true
  Tool = -> Cylinder181
FEATURE [Part::Cut] Cut284  label="Cut678"
  Base = -> Cut285
  Refine = true
  Tool = -> Cut286
FEATURE [Part::Box] Box233  label="Cube459"
  AttacherType = Attacher::AttachEngine3D
  Height = 21
  Length = 38
  Placement = pos=(15,167,-23) rot=(0,0,1;0rad)
  Width = 3
FEATURE [Part::Cut] Cut283  label="Cut677"
  Base = -> Cut284
  Refine = true
  Tool = -> Box233
FEATURE [Part::Box] Box234  label="Cube460"
  AttacherType = Attacher::AttachEngine3D
  Height = 20
  Length = 33
  Placement = pos=(15,156,-31) rot=(0,0,1;0rad)
  Width = 14
FEATURE [Part::Cylinder] Cylinder182
  Angle = 360
  AttacherType = Attacher::AttachEngine3D
  Height = 22
  Placement = pos=(98,174,-23) rot=(1,0,0;1.5708rad)
  Radius = 52
FEATURE [Part::Box] Box235  label="Cube461"
  AttacherType = Attacher::AttachEngine3D
  Height = 9
  Length = 5
  Placement = pos=(46,152,-32) rot=(0,0,1;0rad)
  Width = 22
FEATURE [Part::MultiFuse] Fusion128
  Refine = true
  Shapes = -> [Cylinder182,Box235]
FEATURE [Part::Cut] Cut290  label="Cut684"
  Base = -> Box234
  Refine = true
  Tool = -> Fusion128
FEATURE [Part::Box] Box236  label="Cube462"
  AttacherType = Attacher::AttachEngine3D
  Height = 9
  Length = 31
  Placement = pos=(17,156,-29) rot=(0,0,1;0rad)
  Width = 14
FEATURE [Part::Cylinder] Cylinder183
  Angle = 360
  AttacherType = Attacher::AttachEngine3D
  Height = 22
  Placement = pos=(98,174,-23) rot=(1,0,0;1.5708rad)
  Radius = 54
FEATURE [Part::Box] Box237  label="Cube463"
  AttacherType = Attacher::AttachEngine3D
  Height = 7.5
  Length = 4
  Placement = pos=(44,152,-31) rot=(0,0,1;0rad)
  Width = 22
FEATURE [Part::MultiFuse] Fusion129
  Refine = true
  Shapes = -> [Cylinder183,Box237]
FEATURE [Part::Cut] Cut291  label="Cut685"
  Base = -> Box236
  Refine = true
  Tool = -> Fusion129
FEATURE [Part::Cut] Cut289  label="Cut683"
  Base = -> Cut290
  Refine = true
  Tool = -> Cut291
FEATURE [Part::Box] Box238  label="Cube464"
  AttacherType = Attacher::AttachEngine3D
  Height = 20
  Length = 33
  Placement = pos=(15,169,-29) rot=(0,0,1;0rad)
  Width = 3
FEATURE [Part::Box] Box239  label="Cube465"
  AttacherType = Attacher::AttachEngine3D
  Height = 2
  Length = 33
  Placement = pos=(15,156,-31) rot=(0,0,1;0rad)
  Width = 14
FEATURE [Part::Cut] Cut292  label="Cut686"
  Base = -> Box238
  Refine = true
  Tool = -> Box239
FEATURE [Part::Cut] Cut288  label="Cut682"
  Base = -> Cut289
  Refine = true
  Tool = -> Cut292
FEATURE [Part::Box] Box240  label="Cube466"
  AttacherType = Attacher::AttachEngine3D
  Height = 12
  Length = 28
  Placement = pos=(17,165,-24) rot=(-1,0,0;0.279253rad)
  Width = 3
FEATURE [Part::Cylinder] Cylinder184
  Angle = 360
  AttacherType = Attacher::AttachEngine3D
  Height = 22
  Placement = pos=(98,174,-23) rot=(1,0,0;1.5708rad)
  Radius = 54
FEATURE [Part::Box] Box241  label="Cube467"
  AttacherType = Attacher::AttachEngine3D
  Height = 9
  Length = 5
  Placement = pos=(44,152,-32) rot=(0,0,1;0rad)
  Width = 22
FEATURE [Part::MultiFuse] Fusion130
  Refine = true
  Shapes = -> [Cylinder184,Box241]
FEATURE [Part::Cut] Cut293  label="Cut687"
  Base = -> Box240
  Placement = pos=(0,1,0) rot=(0,0,1;0rad)
  Refine = true
  Tool = -> Fusion130
FEATURE [Part::Cut] Cut287  label="Cut681"
  Base = -> Cut288
  Refine = true
  Tool = -> Cut293
FEATURE [Part::Box] Box242  label="Cube468"
  AttacherType = Attacher::AttachEngine3D
  Height = 4
  Length = 10
  Placement = pos=(95,-15,13) rot=(0,0,1;0rad)
  Width = 4
FEATURE [Part::Box] Box243  label="Cube469"
  AttacherType = Attacher::AttachEngine3D
  Height = 4
  Length = 10
  Placement = pos=(100,-19,13) rot=(0,0,1;0.139626rad)
  Width = 4
FEATURE [Part::Mirroring] Part__Mirroring016  label="Cube432 (Mirror #9)002"
  Base = (0,0,0)
  Normal = (1,0,0)
  Placement = pos=(200,0,0) rot=(0,0,1;0rad)
  Source = -> Box243
FEATURE [Part::Box] Box244  label="Cube470"
  AttacherType = Attacher::AttachEngine3D
  Height = 4
  Length = 10
  Placement = pos=(100,-19,13) rot=(0,0,1;0.139626rad)
  Width = 4
FEATURE [Part::MultiFuse] Fusion132
  Refine = true
  Shapes = -> [Part__Mirroring016,Box244]
FEATURE [Part::Cut] Cut295  label="Cut689"
  Base = -> Box242
  Refine = true
  Tool = -> Fusion132
FEATURE [Part::Fillet] Fillet131
  Base = -> Cut295
  Edges = 3 edges r=0.5: [Edge4,Edge14,Edge15]
FEATURE [Part::Fillet] Fillet130
  Base = -> Fillet131
  Edges = 4 edges r=0.5: [Edge7,Edge11,Edge16,Edge20]
  Placement = pos=(-2,6,2) rot=(0,0,1;0rad)
FEATURE [Part::Mirroring] Part__Mirroring015  label="Fillet113 (Mirror #11)001"
  Base = (0,0,0)
  Normal = (0,1,0)
  Placement = pos=(0,170,0) rot=(0,0,1;0rad)
  Source = -> Fillet130
FEATURE [Part::Box] Box245  label="Cube471"
  AttacherType = Attacher::AttachEngine3D
  Height = 5.8
  Length = 13.6
  Placement = pos=(91.2,163,27) rot=(0,0,1;0rad)
  Width = 4
FEATURE [Part::Box] Box246  label="Cube472"
  AttacherType = Attacher::AttachEngine3D
  Height = 7
  Length = 10
  Placement = pos=(46,152,-30) rot=(0,0,1;0rad)
  Width = 25
FEATURE [Part::Cylinder] Cylinder185
  Angle = 360
  AttacherType = Attacher::AttachEngine3D
  Height = 25
  Placement = pos=(98,177,-23) rot=(0.799251,-0.424969,0.424969;1.79303rad)
  Radius = 52
FEATURE [Part::MultiFuse] Fusion134
  Refine = true
  Shapes = -> [Box246,Cylinder185]
FEATURE [Part::Cylinder] Cylinder186
  Angle = 360
  AttacherType = Attacher::AttachEngine3D
  Height = 28
  Placement = pos=(98,175,-23) rot=(0.799251,-0.424969,0.424969;1.79303rad)
  Radius = 50
FEATURE [Part::Cut] Cut299
  Base = -> Fusion134
  Refine = true
  Tool = -> Cylinder186
FEATURE [Part::Cylinder] Cylinder187
  Angle = 360
  AttacherType = Attacher::AttachEngine3D
  Height = 30
  Placement = pos=(98,177,-30) rot=(0.799251,-0.424969,0.424969;1.79303rad)
  Radius = 48
FEATURE [Part::Cut] Cut298  label="Cut691"
  Base = -> Cut299
  Refine = true
  Tool = -> Cylinder187
FEATURE [Part::Box] Box247  label="Cube473"
  AttacherType = Attacher::AttachEngine3D
  Height = 7
  Length = 10
  Placement = pos=(48,147,-30) rot=(0,0,1;0rad)
  Width = 28
FEATURE [Part::Cut] Cut297  label="Cut690"
  Base = -> Cut298
  Refine = true
  Tool = -> Box247
FEATURE [Part::Box] Box248  label="Cube474"
  AttacherType = Attacher::AttachEngine3D
  Height = 7
  Length = 45
  Placement = pos=(76,175,14) rot=(0,0,1;0rad)
  Width = 2
FEATURE [Part::MultiFuse] Fusion133
  Refine = true
  Shapes = -> [Cut297,Box248]
FEATURE [Part::Box] Box249  label="Cube475"
  AttacherType = Attacher::AttachEngine3D
  Height = 14
  Length = 10
  Placement = pos=(116,168,12) rot=(0,1,0;0.401426rad)
  Width = 9
FEATURE [Part::Cut] Cut296
  Base = -> Fusion133
  Refine = true
  Tool = -> Box249
FEATURE [Part::MultiFuse] Fusion131
  Refine = true
  Shapes = -> [Part__Mirroring015,Box245,Cut296]
FEATURE [Part::Box] Box250  label="Cube476"
  AttacherType = Attacher::AttachEngine3D
  Height = 10
  Length = 10
  Placement = pos=(46,152,-31) rot=(0,1,0;0.785398rad)
  Width = 25
FEATURE [Part::Cut] Cut294  label="Cut688"
  Base = -> Fusion131
  Refine = true
  Tool = -> Box250
FEATURE [Part::Fillet] Fillet129
  Base = -> Cut294
  Edges = 1 edges r=1: [Edge14]
FEATURE [Part::Cylinder] Cylinder188
  Angle = 360
  AttacherType = Attacher::AttachEngine3D
  Height = 33
  Placement = pos=(98,175,-23) rot=(1,0,0;1.5708rad)
  Radius = 50
FEATURE [Part::Cylinder] Cylinder189
  Angle = 360
  AttacherType = Attacher::AttachEngine3D
  Height = 35
  Placement = pos=(98,177,-23) rot=(1,0,0;1.5708rad)
  Radius = 52
FEATURE [Part::Cylinder] Cylinder190
  Angle = 360
  AttacherType = Attacher::AttachEngine3D
  Height = 33
  Placement = pos=(98,177,-30) rot=(1,0,0;1.5708rad)
  Radius = 48
FEATURE [Part::MultiFuse] Fusion135
  Refine = true
  Shapes = -> [Cylinder188,Cylinder190]
FEATURE [Part::Cut] Cut300
  Base = -> Cylinder189
  Refine = true
  Tool = -> Fusion135
FEATURE [Part::Box] Box251  label="Cube477"
  AttacherType = Attacher::AttachEngine3D
  Height = 10
  Length = 6.5
  Placement = pos=(145.5,142,-33) rot=(0,0,1;0rad)
  Width = 35
FEATURE [Part::Box] Box252  label="Cube478"
  AttacherType = Attacher::AttachEngine3D
  Height = 10
  Length = 4.5
  Placement = pos=(143.5,140,-33) rot=(0,0,1;0rad)
  Width = 35
FEATURE [Part::Cut] Cut301
  Base = -> Box251
  Refine = true
  Tool = -> Box252
FEATURE [Part::MultiFuse] Fusion136
  Refine = true
  Shapes = -> [Cut300,Cut301]
FEATURE [Part::Chamfer] Chamfer044
  Base = -> Fusion136
  Edges = 1 edges r=1.99: [Edge8]
FEATURE [Part::Chamfer] Chamfer045
  Base = -> Chamfer044
  Edges = 1 edges r=2.49: [Edge30]
FEATURE [Part::Box] Box253  label="Cube479"
  AttacherType = Attacher::AttachEngine3D
  Height = 11
  Length = 7.5
  Placement = pos=(117.3,133.5,15) rot=(0,1,0;0.471239rad)
  Width = 35
FEATURE [Part::Cylinder] Cylinder192
  Angle = 360
  AttacherType = Attacher::AttachEngine3D
  Height = 23
  Placement = pos=(98,175,-23) rot=(0.829023,-0.395424,0.395424;1.75721rad)
  Radius = 50
FEATURE [Part::Cut] Cut302
  Base = -> Chamfer045
  Refine = true
  Tool = -> Box253
FEATURE [Part::Cylinder] Cylinder193
  Angle = 360
  AttacherType = Attacher::AttachEngine3D
  Height = 33
  Placement = pos=(98,175,-23) rot=(1,0,0;1.5708rad)
  Radius = 48
FEATURE [Part::Cut] Cut303
  Base = -> Cylinder192
  Refine = true
  Tool = -> Cylinder193
FEATURE [Part::MultiFuse] Fusion137
  Refine = true
  Shapes = -> [Cut302,Cut303]
FEATURE [Part::Chamfer] Chamfer046
  Base = -> Fusion137
  Edges = 1 edges r=1.99: [Edge50]
  Placement = pos=(1,0,-1) rot=(0,0,1;0rad)
FEATURE [Part::Fillet] Fillet132
  Base = -> Chamfer046
  Edges = 1 edges r=1: [Edge53]
FEATURE [Part::Cylinder] Cylinder194
  Angle = 360
  AttacherType = Attacher::AttachEngine3D
  Height = 10
  Placement = pos=(144,152,0) rot=(1,0,0;1.5708rad)
  Radius = 3
FEATURE [Part::Cylinder] Cylinder195
  Angle = 360
  AttacherType = Attacher::AttachEngine3D
  Height = 10
  Placement = pos=(144,152,0) rot=(1,0,0;1.5708rad)
  Radius = 1.5
FEATURE [Part::Cut] Cut304
  Base = -> Cylinder194
  Placement = pos=(-13,0,12) rot=(0,0,1;0rad)
  Refine = true
  Tool = -> Cylinder195
FEATURE [Part::Cylinder] Cylinder196
  Angle = 360
  AttacherType = Attacher::AttachEngine3D
  Height = 10
  Placement = pos=(144,152,0) rot=(1,0,0;1.5708rad)
  Radius = 3
FEATURE [Part::Cylinder] Cylinder197
  Angle = 360
  AttacherType = Attacher::AttachEngine3D
  Height = 10
  Placement = pos=(144,152,0) rot=(1,0,0;1.5708rad)
  Radius = 1.5
FEATURE [Part::Cut] Cut305
  Base = -> Cylinder196
  Placement = pos=(0,0,-6) rot=(0,0,1;0rad)
  Refine = true
  Tool = -> Cylinder197
FEATURE [Part::MultiFuse] Fusion138  label="wing-right-rear_"
  Refine = true
  Shapes = -> [Fillet132,Cut305,Cut304]
FEATURE [Part::Cylinder] Cylinder198
  Angle = 360
  AttacherType = Attacher::AttachEngine3D
  Height = 35
  Placement = pos=(98,177,-23) rot=(1,0,0;1.5708rad)
  Radius = 52
FEATURE [Part::Cylinder] Cylinder199
  Angle = 360
  AttacherType = Attacher::AttachEngine3D
  Height = 33
  Placement = pos=(98,175,-23) rot=(1,0,0;1.5708rad)
  Radius = 50
FEATURE [Part::Cylinder] Cylinder200
  Angle = 360
  AttacherType = Attacher::AttachEngine3D
  Height = 33
  Placement = pos=(98,177,-30) rot=(1,0,0;1.5708rad)
  Radius = 48
FEATURE [Part::MultiFuse] Fusion142
  Refine = true
  Shapes = -> [Cylinder199,Cylinder200]
FEATURE [Part::Cut] Cut307
  Base = -> Cylinder198
  Refine = true
  Tool = -> Fusion142
FEATURE [Part::Box] Box254  label="Cube480"
  AttacherType = Attacher::AttachEngine3D
  Height = 10
  Length = 6.5
  Placement = pos=(145.5,142,-33) rot=(0,0,1;0rad)
  Width = 35
FEATURE [Part::Box] Box255  label="Cube481"
  AttacherType = Attacher::AttachEngine3D
  Height = 10
  Length = 4.5
  Placement = pos=(143.5,140,-33) rot=(0,0,1;0rad)
  Width = 35
FEATURE [Part::Cut] Cut308
  Base = -> Box254
  Refine = true
  Tool = -> Box255
FEATURE [Part::MultiFuse] Fusion141
  Refine = true
  Shapes = -> [Cut307,Cut308]
FEATURE [Part::Chamfer] Chamfer049
  Base = -> Fusion141
  Edges = 1 edges r=1.99: [Edge8]
FEATURE [Part::Chamfer] Chamfer048
  Base = -> Chamfer049
  Edges = 1 edges r=2.49: [Edge30]
FEATURE [Part::Box] Box256  label="Cube482"
  AttacherType = Attacher::AttachEngine3D
  Height = 11
  Length = 7.5
  Placement = pos=(117.3,133.5,15) rot=(0,1,0;0.471239rad)
  Width = 35
FEATURE [Part::Cut] Cut306
  Base = -> Chamfer048
  Refine = true
  Tool = -> Box256
FEATURE [Part::Cylinder] Cylinder201
  Angle = 360
  AttacherType = Attacher::AttachEngine3D
  Height = 23
  Placement = pos=(98,175,-23) rot=(0.829023,-0.395424,0.395424;1.75721rad)
  Radius = 50
FEATURE [Part::Cylinder] Cylinder202
  Angle = 360
  AttacherType = Attacher::AttachEngine3D
  Height = 33
  Placement = pos=(98,175,-23) rot=(1,0,0;1.5708rad)
  Radius = 48
FEATURE [Part::Cut] Cut309
  Base = -> Cylinder201
  Refine = true
  Tool = -> Cylinder202
FEATURE [Part::MultiFuse] Fusion140
  Refine = true
  Shapes = -> [Cut306,Cut309]
FEATURE [Part::Chamfer] Chamfer047
  Base = -> Fusion140
  Edges = 1 edges r=1.99: [Edge50]
  Placement = pos=(1,0,-1) rot=(0,0,1;0rad)
FEATURE [Part::Fillet] Fillet133
  Base = -> Chamfer047
  Edges = 1 edges r=1: [Edge53]
FEATURE [Part::Cylinder] Cylinder203
  Angle = 360
  AttacherType = Attacher::AttachEngine3D
  Height = 10
  Placement = pos=(144,152,0) rot=(1,0,0;1.5708rad)
  Radius = 3
FEATURE [Part::Cylinder] Cylinder204
  Angle = 360
  AttacherType = Attacher::AttachEngine3D
  Height = 10
  Placement = pos=(144,152,0) rot=(1,0,0;1.5708rad)
  Radius = 1.5
FEATURE [Part::Cut] Cut310
  Base = -> Cylinder203
  Placement = pos=(0,0,-6) rot=(0,0,1;0rad)
  Refine = true
  Tool = -> Cylinder204
FEATURE [Part::Cylinder] Cylinder205
  Angle = 360
  AttacherType = Attacher::AttachEngine3D
  Height = 10
  Placement = pos=(144,152,0) rot=(1,0,0;1.5708rad)
  Radius = 3
FEATURE [Part::Cylinder] Cylinder206
  Angle = 360
  AttacherType = Attacher::AttachEngine3D
  Height = 10
  Placement = pos=(144,152,0) rot=(1,0,0;1.5708rad)
  Radius = 1.5
FEATURE [Part::Cut] Cut311
  Base = -> Cylinder205
  Placement = pos=(-13,0,12) rot=(0,0,1;0rad)
  Refine = true
  Tool = -> Cylinder206
FEATURE [Part::MultiFuse] Fusion139  label="right-rear-wing001"
  Refine = true
  Shapes = -> [Fillet133,Cut310,Cut311]
FEATURE [Part::Mirroring] Part__Mirroring018  label="wing-left-rear_"
  Base = (0,0,0)
  Normal = (0,1,0)
  Placement = pos=(0,170,0) rot=(0,0,1;0rad)
  Source = -> Fusion139
FEATURE [Part::Box] Box257  label="Cube483"
  AttacherType = Attacher::AttachEngine3D
  Height = 34
  Length = 5
  Placement = pos=(7,38,2) rot=(0,0,1;0rad)
  Width = 94
FEATURE [Part::Chamfer] Chamfer050
  Base = -> Box257
  Edges = 1 edges r=4.99: [Edge6]
FEATURE [Part::Cylinder] Cylinder207
  Angle = 360
  AttacherType = Attacher::AttachEngine3D
  Height = 10
  Placement = pos=(12,57.5,21) rot=(0,1,0;1.5708rad)
  Radius = 1.25
FEATURE [Part::Cylinder] Cylinder208
  Angle = 360
  AttacherType = Attacher::AttachEngine3D
  Height = 10
  Placement = pos=(12,112.5,21) rot=(0,1,0;1.5708rad)
  Radius = 1.25
FEATURE [Part::Cylinder] Cylinder209
  Angle = 360
  AttacherType = Attacher::AttachEngine3D
  Height = 10
  Placement = pos=(12,85,16) rot=(0,1,0;1.5708rad)
  Radius = 1.25
FEATURE [Part::MultiFuse] Fusion144
  Placement = pos=(-7,0,0) rot=(0,0,1;0rad)
  Refine = true
  Shapes = -> [Cylinder207,Cylinder209,Cylinder208]
FEATURE [Part::MultiFuse] Fusion145
  Refine = true
  Shapes = -> [Cut262,Chamfer050]
FEATURE [Part::Cut] Cut312  label="cab-lower-part-02"
  Base = -> Fusion145
  Refine = true
  Tool = -> Fusion144
FEATURE [Part::Fillet] Fillet134
  Base = -> Cut287
  Edges = 2 edges r=1: [Edge4,Edge32]
FEATURE [Part::MultiFuse] Fusion146
  Refine = true
  Shapes = -> [Cut283,Fillet129,Fillet134]
FEATURE [Part::Mirroring] Part__Mirroring019  label="left-wing"
  Base = (0,0,0)
  Normal = (0,1,0)
  Placement = pos=(0,170,0) rot=(0,0,1;0rad)
  Source = -> Fusion146
FEATURE [Part::Fillet] Fillet135
  Base = -> Cut282
  Edges = 2 edges r=1: [Edge4,Edge32]
FEATURE [Part::MultiFuse] Fusion147  label="right-wing"
  Refine = true
  Shapes = -> [Cut275,Fillet128,Fillet135]
FEATURE [Part::Part2DObjectPython] ShapeString003  # Draft 2D object (typed FeaturePython)
  FontFile = <path>
  MapMode = 5
  Placement = pos=(57,0,71) rot=(1,0,0;1.5708rad)
  Size = 3.5
  String = 250-30
  Tracking = 0
FEATURE [Part::Extrusion] Extrude003  label="front-left-window-frame-logo"
  Base = -> ShapeString003
  Dir = (0,0.5,0)
  DirMode = 0
  FaceMakerClass = Part::FaceMakerExtrusion
  LengthFwd = 0
  LengthRev = 0
  Placement = pos=(2,-0.3,-1.5) rot=(-1,0,0;0.036652rad)
  Solid = false
  Symmetric = false
FEATURE [Part::Box] Box278  label="Cube504"
  AttacherType = Attacher::AttachEngine3D
  Height = 39
  Length = 27
  Placement = pos=(89.5,0,74.5) rot=(0,0,1;0rad)
  Width = 0.5
FEATURE [Part::Fillet] Fillet161
  Base = -> Box278
  Edges = 4 edges r=3.5: [Edge2,Edge4,Edge6,Edge8]
  Placement = pos=(-3,-2,0) rot=(0,0,1;0rad)
FEATURE [Part::Box] Box279  label="Cube505"
  AttacherType = Attacher::AttachEngine3D
  Height = 36
  Length = 24
  Placement = pos=(89,0,74) rot=(0,0,1;0rad)
  Width = 6
FEATURE [Part::Fillet] Fillet162
  Base = -> Box279
  Edges = 4 edges r=2.5: [Edge2,Edge4,Edge6,Edge8]
  Placement = pos=(-1,-2,2) rot=(0,0,1;0rad)
FEATURE [Part::Box] Box280  label="Cube506"
  AttacherType = Attacher::AttachEngine3D
  Height = 42
  Length = 26
  Placement = pos=(90,0,71) rot=(0,0,1;0rad)
  Width = 1
FEATURE [Part::Fillet] Fillet163
  Base = -> Box280
  Edges = 4 edges r=3: [Edge2,Edge4,Edge6,Edge8]
  Placement = pos=(-3,-1.5,0) rot=(0,0,1;0rad)
FEATURE [Part::Box] Box281  label="Cube507"
  AttacherType = Attacher::AttachEngine3D
  Height = 44
  Length = 27
  Placement = pos=(89.5,0.25,69.5) rot=(0,0,1;0rad)
  Width = 0.25
FEATURE [Part::Fillet] Fillet164
  Base = -> Box281
  Edges = 4 edges r=3.5: [Edge2,Edge4,Edge6,Edge8]
  Placement = pos=(-3,-2,0) rot=(0,0,1;0rad)
FEATURE [Part::Fillet] Fillet165
  Base = -> Fillet161
  Edges = 2 edges r=0.49: [Edge1,Edge8]
FEATURE [Part::Fillet] Fillet166
  Base = -> Fillet164
  Edges = 2 edges r=0.24: [Edge1,Edge8]
FEATURE [Part::MultiFuse] Fusion156
  Refine = true
  Shapes = -> [Fillet166,Fillet165,Fillet163]
FEATURE [Part::Cut] Cut323  label="Cut692"
  Base = -> Fusion156
  Refine = true
  Tool = -> Fillet162
FEATURE [Part::Fillet] Fillet167  label="window-frame-rear-left"
  Base = -> Cut323
  Edges = 2 edges r=1: [Edge81,Edge85]
  Placement = pos=(-1,2,-1) rot=(-1,0,0;0.036652rad)
FEATURE [Part::Box] Box282  label="Cube508"
  AttacherType = Attacher::AttachEngine3D
  Height = 39
  Length = 27
  Placement = pos=(89.5,0,74.5) rot=(0,0,1;0rad)
  Width = 0.5
FEATURE [Part::Box] Box283  label="Cube509"
  AttacherType = Attacher::AttachEngine3D
  Height = 44
  Length = 27
  Placement = pos=(89.5,0.25,69.5) rot=(0,0,1;0rad)
  Width = 0.25
FEATURE [Part::Box] Box284  label="Cube510"
  AttacherType = Attacher::AttachEngine3D
  Height = 42
  Length = 26
  Placement = pos=(90,0,71) rot=(0,0,1;0rad)
  Width = 1
FEATURE [Part::Fillet] Fillet169
  Base = -> Box284
  Edges = 4 edges r=3: [Edge2,Edge4,Edge6,Edge8]
  Placement = pos=(-3,-1.5,0) rot=(0,0,1;0rad)
FEATURE [Part::Box] Box285  label="Cube511"
  AttacherType = Attacher::AttachEngine3D
  Height = 36
  Length = 24
  Placement = pos=(89,0,74) rot=(0,0,1;0rad)
  Width = 6
FEATURE [Part::Fillet] Fillet171
  Base = -> Box282
  Edges = 4 edges r=3.5: [Edge2,Edge4,Edge6,Edge8]
  Placement = pos=(-3,-2,0) rot=(0,0,1;0rad)
FEATURE [Part::Fillet] Fillet172
  Base = -> Box285
  Edges = 4 edges r=2.5: [Edge2,Edge4,Edge6,Edge8]
  Placement = pos=(-1,-2,2) rot=(0,0,1;0rad)
FEATURE [Part::Fillet] Fillet173
  Base = -> Box283
  Edges = 4 edges r=3.5: [Edge2,Edge4,Edge6,Edge8]
  Placement = pos=(-3,-2,0) rot=(0,0,1;0rad)
FEATURE [Part::Fillet] Fillet170
  Base = -> Fillet173
  Edges = 2 edges r=0.24: [Edge1,Edge8]
FEATURE [Part::Fillet] Fillet174
  Base = -> Fillet171
  Edges = 2 edges r=0.49: [Edge1,Edge8]
FEATURE [Part::MultiFuse] Fusion157
  Refine = true
  Shapes = -> [Fillet170,Fillet174,Fillet169]
FEATURE [Part::Cut] Cut324  label="Cut693"
  Base = -> Fusion157
  Refine = true
  Tool = -> Fillet172
FEATURE [Part::Fillet] Fillet168  label="rear-left-window-frame001"
  Base = -> Cut324
  Edges = 2 edges r=1: [Edge81,Edge85]
  Placement = pos=(-1,2,-1) rot=(-1,0,0;0.036652rad)
FEATURE [Part::Mirroring] Part__Mirroring022  label="window-frame-rear-right"
  Base = (0,0,0)
  Normal = (0,1,0)
  Placement = pos=(0,170,0) rot=(0,0,1;0rad)
  Source = -> Fillet168
FEATURE [Part::Part2DObjectPython] ShapeString005  # Draft 2D object (typed FeaturePython)
  FontFile = <path>
  MapMode = 5
  Placement = pos=(57,0,71) rot=(1,0,0;1.5708rad)
  Size = 3.5
  String = 250-30
  Tracking = 0
FEATURE [Part::Extrusion] Extrude005  label="front-right-window-frame-logo"
  Base = -> ShapeString005
  Dir = (0,0.5,0)
  DirMode = 0
  FaceMakerClass = Part::FaceMakerExtrusion
  LengthFwd = 0
  LengthRev = 0
  Placement = pos=(130,170.324,-1.6) rot=(0,-0.018325,0.999832;3.14159rad)
  Solid = false
  Symmetric = false
FEATURE [Part::Box] Box297  label="Cube523"
  AttacherType = Attacher::AttachEngine3D
  Height = 57
  Length = 8
  Placement = pos=(-0.5,6,67) rot=(0,1,0;0.244346rad)
  Width = 158
FEATURE [Part::Fillet] Fillet200
  Base = -> Box297
  Edges = 4 edges r=5: [Edge9,Edge10,Edge11,Edge12]
  Placement = pos=(6,0,-1) rot=(0,0,1;0rad)
FEATURE [Part::Feature] Face005
  Placement = pos=(0,0,-10) rot=(0,0,1;0rad)
  shape: bbox 128.7 x 180.4 x 2e-07 mm, 1 faces, 0 solids (baked)
FEATURE [Part::Feature] Face006
  Placement = pos=(0,0,50) rot=(0,0,1;0rad)
  shape: bbox 110 x 176 x 2e-07 mm, 1 faces, 0 solids (baked)
FEATURE [Part::Loft] Loft002
  Closed = false
  MaxDegree = 5
  Ruled = false
  Sections = -> [Face006,Face005]
  Solid = true
FEATURE [Part::Cut] Cut334  label="Cut694"
  Base = -> Fillet200
  Refine = true
  Tool = -> Loft002
FEATURE [Part::Box] Box298  label="Cube524"
  AttacherType = Attacher::AttachEngine3D
  Height = 57
  Length = 6.5
  Placement = pos=(-0.5,6,67) rot=(0,1,0;0.244346rad)
  Width = 158
FEATURE [Part::Fillet] Fillet201
  Base = -> Box298
  Edges = 4 edges r=5: [Edge9,Edge10,Edge11,Edge12]
  Placement = pos=(6,0,-1) rot=(0,0,1;0rad)
FEATURE [Part::Cut] Cut335  label="Cut695"
  Base = -> Fillet201
  Placement = pos=(-1,0,0) rot=(0,0,1;0rad)
  Refine = true
  Tool = -> Cut334
FEATURE [Part::Feature] Face007
  Placement = pos=(0,0,-10) rot=(0,0,1;0rad)
  shape: bbox 128.7 x 180.4 x 2e-07 mm, 1 faces, 0 solids (baked)
FEATURE [Part::Feature] Face008
  Placement = pos=(0,0,50) rot=(0,0,1;0rad)
  shape: bbox 110 x 176 x 2e-07 mm, 1 faces, 0 solids (baked)
FEATURE [Part::Loft] Loft003
  Closed = false
  MaxDegree = 5
  Ruled = false
  Sections = -> [Face008,Face007]
  Solid = true
FEATURE [Part::Cut] Cut336  label="Cut696"
  Base = -> Cut335
  Refine = true
  Tool = -> Loft003
FEATURE [Part::Box] Box299  label="Cube525"
  AttacherType = Attacher::AttachEngine3D
  Height = 55
  Length = 10
  Placement = pos=(0,7,68) rot=(0,1,0;0.244346rad)
  Width = 156
FEATURE [Part::Fillet] Fillet202
  Base = -> Box299
  Edges = 4 edges r=5: [Edge9,Edge10,Edge11,Edge12]
  Placement = pos=(5,0,-1) rot=(0,0,1;0rad)
FEATURE [Part::Cut] Cut337  label="Cut697"
  Base = -> Cut336
  Refine = true
  Tool = -> Fillet202
FEATURE [Part::Box] Box300  label="Cube526"
  AttacherType = Attacher::AttachEngine3D
  Height = 55
  Length = 6
  Placement = pos=(0,7,68) rot=(0,1,0;0.244346rad)
  Width = 156
FEATURE [Part::Fillet] Fillet203
  Base = -> Box300
  Edges = 4 edges r=5: [Edge9,Edge10,Edge11,Edge12]
  Placement = pos=(6,0,-1) rot=(0,0,1;0rad)
FEATURE [Part::Box] Box301  label="Cube527"
  AttacherType = Attacher::AttachEngine3D
  Height = 57
  Length = 8
  Placement = pos=(-0.5,6,67) rot=(0,1,0;0.244346rad)
  Width = 158
FEATURE [Part::Fillet] Fillet204
  Base = -> Box301
  Edges = 4 edges r=5: [Edge9,Edge10,Edge11,Edge12]
  Placement = pos=(6,0,-1) rot=(0,0,1;0rad)
FEATURE [Part::Feature] Face009
  Placement = pos=(0,0,50) rot=(0,0,1;0rad)
  shape: bbox 110 x 176 x 2e-07 mm, 1 faces, 0 solids (baked)
FEATURE [Part::Feature] Face010
  Placement = pos=(0,0,-10) rot=(0,0,1;0rad)
  shape: bbox 128.7 x 180.4 x 2e-07 mm, 1 faces, 0 solids (baked)
FEATURE [Part::Loft] Loft004
  Closed = false
  MaxDegree = 5
  Ruled = false
  Sections = -> [Face009,Face010]
  Solid = true
FEATURE [Part::Cut] Cut339  label="Cut699"
  Base = -> Fillet204
  Refine = true
  Tool = -> Loft004
FEATURE [Part::Cut] Cut338  label="Cut698"
  Base = -> Fillet203
  Placement = pos=(-1,0,0) rot=(0,0,1;0rad)
  Refine = true
  Tool = -> Cut339
FEATURE [Part::Feature] Face011
  Placement = pos=(0,0,50) rot=(0,0,1;0rad)
  shape: bbox 110 x 176 x 2e-07 mm, 1 faces, 0 solids (baked)
FEATURE [Part::Feature] Face012
  Placement = pos=(0,0,-10) rot=(0,0,1;0rad)
  shape: bbox 128.7 x 180.4 x 2e-07 mm, 1 faces, 0 solids (baked)
FEATURE [Part::Loft] Loft005
  Closed = false
  MaxDegree = 5
  Placement = pos=(1,0,0) rot=(0,0,1;0rad)
  Ruled = false
  Sections = -> [Face011,Face012]
  Solid = true
FEATURE [Part::Cut] Cut340  label="Cut700"
  Base = -> Cut338
  Refine = true
  Tool = -> Loft005
FEATURE [Part::MultiFuse] Fusion167
  Refine = true
  Shapes = -> [Cut337,Cut340]
FEATURE [Part::Box] Box302  label="Cube528"
  AttacherType = Attacher::AttachEngine3D
  Height = 53
  Length = 10
  Placement = pos=(-1,8,69) rot=(0,1,0;0.244346rad)
  Width = 154
FEATURE [Part::Fillet] Fillet205
  Base = -> Box302
  Edges = 4 edges r=5: [Edge9,Edge10,Edge11,Edge12]
  Placement = pos=(6,0,-1) rot=(0,0,1;0rad)
FEATURE [Part::Cut] Cut341  label="Cut701"
  Base = -> Fusion167
  Refine = true
  Tool = -> Fillet205
FEATURE [Part::Box] Box303  label="Cube529"
  AttacherType = Attacher::AttachEngine3D
  Height = 39
  Length = 0.5
  Placement = pos=(175,0.5,0.5) rot=(0,0,1;0rad)
  Width = 26
FEATURE [Part::Box] Box304  label="Cube530"
  AttacherType = Attacher::AttachEngine3D
  Height = 42
  Length = 5
  Placement = pos=(175,-23.5,-1) rot=(-1,0,0;0.038397rad)
  Width = 24
FEATURE [Part::Cut] Cut342  label="Cut702"
  Base = -> Box303
  Placement = pos=(-57,16,73) rot=(0,0,1;0rad)
  Refine = true
  Tool = -> Box304
FEATURE [Part::Box] Box305  label="Cube531"
  AttacherType = Attacher::AttachEngine3D
  Height = 38
  Length = 1.5
  Placement = pos=(175,0,0) rot=(0,0,1;0rad)
  Width = 25
FEATURE [Part::Box] Box306  label="Cube532"
  AttacherType = Attacher::AttachEngine3D
  Height = 40
  Length = 5
  Placement = pos=(175,-24,-1) rot=(-1,0,0;0.038397rad)
  Width = 24
FEATURE [Part::Cut] Cut343  label="Cut703"
  Base = -> Box305
  Placement = pos=(-57,17,74) rot=(0,0,1;0rad)
  Refine = true
  Tool = -> Box306
FEATURE [Part::Fillet] Fillet208
  Base = -> Cut343
  Edges = 4 edges r=3: [Edge5,Edge7,Edge8,Edge11]
  Placement = pos=(3,0,0) rot=(0,0,1;0rad)
FEATURE [Part::Box] Box307  label="Cube533"
  AttacherType = Attacher::AttachEngine3D
  Height = 36
  Length = 5
  Placement = pos=(175,0,0) rot=(0,0,1;0rad)
  Width = 23
FEATURE [Part::Box] Box308  label="Cube534"
  AttacherType = Attacher::AttachEngine3D
  Height = 40
  Length = 5
  Placement = pos=(175,-24,-1) rot=(-1,0,0;0.038397rad)
  Width = 24
FEATURE [Part::Cut] Cut344  label="Cut704"
  Base = -> Box307
  Placement = pos=(-57,17,74) rot=(0,0,1;0rad)
  Refine = true
  Tool = -> Box308
FEATURE [Part::Fillet] Fillet209
  Base = -> Cut344
  Edges = 4 edges r=2.5: [Edge5,Edge7,Edge8,Edge11]
  Placement = pos=(0,1,1) rot=(0,0,1;0rad)
FEATURE [Part::Box] Box315  label="Cube541"
  AttacherType = Attacher::AttachEngine3D
  Height = 25
  Length = 5
  Placement = pos=(118,56,86) rot=(0,0,1;0rad)
  Width = 58
FEATURE [Part::Fillet] Fillet217
  Base = -> Box315
  Edges = 4 edges r=2: [Edge9,Edge10,Edge11,Edge12]
FEATURE [Part::Box] Box316  label="Cube542"
  AttacherType = Attacher::AttachEngine3D
  Height = 27
  Length = 1.5
  Placement = pos=(118,55,85) rot=(0,0,1;0rad)
  Width = 60
FEATURE [Part::Fillet] Fillet218
  Base = -> Box316
  Edges = 4 edges r=3: [Edge9,Edge10,Edge11,Edge12]
  Placement = pos=(3,0,0) rot=(0,0,1;0rad)
FEATURE [Part::Box] Box317  label="Cube543"
  AttacherType = Attacher::AttachEngine3D
  Height = 28
  Length = 0.5
  Placement = pos=(118,54.5,84.5) rot=(0,0,1;0rad)
  Width = 61
FEATURE [Part::Fillet] Fillet219
  Base = -> Box317
  Edges = 4 edges r=3.5: [Edge9,Edge10,Edge11,Edge12]
  Placement = pos=(4,0,0) rot=(0,0,1;0rad)
FEATURE [Part::Fillet] Fillet222
  Base = -> Cut342
  Edges = 4 edges r=4: [Edge5,Edge7,Edge8,Edge11]
  Placement = pos=(4,0,0) rot=(0,0,1;0rad)
FEATURE [Part::MultiFuse] Fusion171
  Refine = true
  Shapes = -> [Fillet222,Fillet208]
FEATURE [Part::Cut] Cut351  label="Cut705"
  Base = -> Fusion171
  Placement = pos=(3.5,0,-4) rot=(0,-1,0;0.034907rad)
  Refine = true
  Tool = -> Fillet209
FEATURE [Part::Fillet] Fillet223
  Base = -> Cut351
  Edges = 1 edges r=1: [Edge34]
FEATURE [Part::Fillet] Fillet224  label="window-frame-back-left"
  Base = -> Fillet223
  Edges = 1 edges r=0.49: [Edge9]
FEATURE [Part::Box] Box318  label="Cube544"
  AttacherType = Attacher::AttachEngine3D
  Height = 40
  Length = 5
  Placement = pos=(175,-24,-1) rot=(-1,0,0;0.038397rad)
  Width = 24
FEATURE [Part::Box] Box319  label="Cube545"
  AttacherType = Attacher::AttachEngine3D
  Height = 40
  Length = 5
  Placement = pos=(175,-24,-1) rot=(-1,0,0;0.038397rad)
  Width = 24
FEATURE [Part::Box] Box320  label="Cube546"
  AttacherType = Attacher::AttachEngine3D
  Height = 38
  Length = 1.5
  Placement = pos=(175,0,0) rot=(0,0,1;0rad)
  Width = 25
FEATURE [Part::Box] Box321  label="Cube547"
  AttacherType = Attacher::AttachEngine3D
  Height = 42
  Length = 5
  Placement = pos=(175,-23.5,-1) rot=(-1,0,0;0.038397rad)
  Width = 24
FEATURE [Part::Cut] Cut354  label="Cut708"
  Base = -> Box320
  Placement = pos=(-57,17,74) rot=(0,0,1;0rad)
  Refine = true
  Tool = -> Box319
FEATURE [Part::Box] Box322  label="Cube548"
  AttacherType = Attacher::AttachEngine3D
  Height = 39
  Length = 0.5
  Placement = pos=(175,0.5,0.5) rot=(0,0,1;0rad)
  Width = 26
FEATURE [Part::Box] Box323  label="Cube549"
  AttacherType = Attacher::AttachEngine3D
  Height = 36
  Length = 5
  Placement = pos=(175,0,0) rot=(0,0,1;0rad)
  Width = 23
FEATURE [Part::Cut] Cut353  label="Cut707"
  Base = -> Box323
  Placement = pos=(-57,17,74) rot=(0,0,1;0rad)
  Refine = true
  Tool = -> Box318
FEATURE [Part::Fillet] Fillet228
  Base = -> Cut353
  Edges = 4 edges r=2.5: [Edge5,Edge7,Edge8,Edge11]
  Placement = pos=(0,1,1) rot=(0,0,1;0rad)
FEATURE [Part::Cut] Cut355  label="Cut709"
  Base = -> Box322
  Placement = pos=(-57,16,73) rot=(0,0,1;0rad)
  Refine = true
  Tool = -> Box321
FEATURE [Part::Fillet] Fillet227
  Base = -> Cut355
  Edges = 4 edges r=4: [Edge5,Edge7,Edge8,Edge11]
  Placement = pos=(4,0,0) rot=(0,0,1;0rad)
FEATURE [Part::Fillet] Fillet229
  Base = -> Cut354
  Edges = 4 edges r=3: [Edge5,Edge7,Edge8,Edge11]
  Placement = pos=(3,0,0) rot=(0,0,1;0rad)
FEATURE [Part::MultiFuse] Fusion172
  Refine = true
  Shapes = -> [Fillet227,Fillet229]
FEATURE [Part::Cut] Cut352  label="Cut706"
  Base = -> Fusion172
  Placement = pos=(3.5,0,-4) rot=(0,-1,0;0.034907rad)
  Refine = true
  Tool = -> Fillet228
FEATURE [Part::Fillet] Fillet226
  Base = -> Cut352
  Edges = 1 edges r=1: [Edge34]
FEATURE [Part::Fillet] Fillet225  label="back-left-window-frame001"
  Base = -> Fillet226
  Edges = 1 edges r=0.49: [Edge9]
FEATURE [Part::Mirroring] Part__Mirroring024  label="window-frame-back-right"
  Base = (0,0,0)
  Normal = (0,1,0)
  Placement = pos=(0,170,0) rot=(0,0,1;0rad)
  Source = -> Fillet225
FEATURE [Part::MultiFuse] Fusion173
  Refine = true
  Shapes = -> [Fillet218,Fillet219]
FEATURE [Part::Cut] Cut356  label="Cut710"
  Base = -> Fusion173
  Refine = true
  Tool = -> Fillet217
FEATURE [Part::Fillet] Fillet230
  Base = -> Cut356
  Edges = 1 edges r=1: [Edge48]
FEATURE [Part::Fillet] Fillet231  label="window-frame-back"
  Base = -> Fillet230
  Edges = 1 edges r=0.49: [Edge40]
  Placement = pos=(3.5,0,-4) rot=(0,-1,0;0.034907rad)
FEATURE [Part::Box] Box324  label="Cube550"
  AttacherType = Attacher::AttachEngine3D
  Height = 38
  Length = 8
  Placement = pos=(125,10,65) rot=(0,0,1;0rad)
  Width = 31
FEATURE [Part::Box] Box325  label="Cube551"
  AttacherType = Attacher::AttachEngine3D
  Height = 17.5
  Length = 8
  Placement = pos=(126,21,44) rot=(0,0,1;0rad)
  Width = 20
FEATURE [Part::Cone] Cone
  Angle = 360
  AttacherType = Attacher::AttachEngine3D
  Height = 5
  Placement = pos=(136,31,22) rot=(0,0,1;0rad)
  Radius1 = 10
  Radius2 = 7
FEATURE [Part::Feature] Face013
  Placement = pos=(-1,0,0) rot=(0,0,1;0rad)
  shape: bbox 8.8 x 22 x 2e-07 mm, 1 faces, 0 solids (baked)
FEATURE [Part::Feature] Face014
  Placement = pos=(0,0,-3) rot=(0,0,1;0rad)
  shape: bbox 21.12 x 16.6 x 2e-07 mm, 1 faces, 0 solids (baked)
FEATURE [Part::Cone] Cone001
  Angle = 360
  AttacherType = Attacher::AttachEngine3D
  Height = 8
  Placement = pos=(136,31,17) rot=(0,0,1;0rad)
  Radius1 = 10
  Radius2 = 7
FEATURE [Part::Cut] Cut357  label="Cut711"
  Base = -> Cone
  Refine = true
  Tool = -> Cone001
FEATURE [Part::Loft] Loft006
  Closed = false
  MaxDegree = 5
  Ruled = false
  Sections = -> [Face013,Face014]
  Solid = true
FEATURE [Part::Fillet] Fillet232
  Base = -> Cut357
  Edges = 1 edges r=1: [Edge3]
FEATURE [Part::MultiFuse] Fusion174
  Refine = true
  Shapes = -> [Box325,Loft006,Fillet232]
FEATURE [Part::Fillet] Fillet233
  Base = -> Fusion174
  Edges = 8 edges r=1: [Edge5,Edge7,Edge9,Edge10,Edge14,Edge15,Edge17,Edge19]
FEATURE [Part::Box] Box326  label="Cube552"
  AttacherType = Attacher::AttachEngine3D
  Height = 36
  Length = 1.25
  Placement = pos=(125.5,10,66) rot=(0,0,1;0rad)
  Width = 2
FEATURE [Part::Box] Box327  label="Cube553"
  AttacherType = Attacher::AttachEngine3D
  Height = 36
  Length = 1.25
  Placement = pos=(127.25,10,66) rot=(0,0,1;0rad)
  Width = 2
FEATURE [Part::Box] Box328  label="Cube554"
  AttacherType = Attacher::AttachEngine3D
  Height = 36
  Length = 1.25
  Placement = pos=(129,10,66) rot=(0,0,1;0rad)
  Width = 2
FEATURE [Part::Box] Box329  label="Cube555"
  AttacherType = Attacher::AttachEngine3D
  Height = 36
  Length = 1.25
  Placement = pos=(130.75,10,66) rot=(0,0,1;0rad)
  Width = 2
FEATURE [Part::MultiFuse] Fusion175
  Placement = pos=(0.25,0,0) rot=(0,0,1;0rad)
  Refine = true
  Shapes = -> [Box326,Box327,Box329,Box328]
FEATURE [Part::Cut] Cut358
  Base = -> Box324
  Refine = true
  Tool = -> Fusion175
FEATURE [Part::Box] Box330  label="Cube556"
  AttacherType = Attacher::AttachEngine3D
  Height = 0.5
  Length = 8
  Placement = pos=(125,10,78) rot=(0,0,1;0rad)
  Width = 2
FEATURE [Part::Box] Box331  label="Cube557"
  AttacherType = Attacher::AttachEngine3D
  Height = 0.5
  Length = 8
  Placement = pos=(125,10,90) rot=(0,0,1;0rad)
  Width = 2
FEATURE [Part::MultiFuse] Fusion176
  Refine = true
  Shapes = -> [Cut358,Box330,Box331]
FEATURE [Part::Box] Box332  label="Cube558"
  AttacherType = Attacher::AttachEngine3D
  Height = 2
  Length = 8
  Placement = pos=(125,21,63) rot=(0,0,1;0rad)
  Width = 20
FEATURE [Part::MultiFuse] Fusion177
  Refine = true
  Shapes = -> [Fusion176,Box332]
FEATURE [Part::Fillet] Fillet234
  Base = -> Fusion177
  Edges = 1 edges r=1.99: [Edge7]
FEATURE [Part::Fillet] Fillet235
  Base = -> Fillet234
  Edges = 1 edges r=3: [Edge30]
FEATURE [Part::Fillet] Fillet236
  Base = -> Fillet235
  Edges = 2 edges r=1: [Edge4,Edge20]
FEATURE [Part::Fillet] Fillet237
  Base = -> Fillet236
  Edges = 2 edges r=1: [Edge7,Edge29]
  Placement = pos=(2,0,-3) rot=(0,-1,0;0.034907rad)
FEATURE [Part::Feature] Face015
  shape: bbox 8.795 x 22 x 0.3071 mm, 1 faces, 0 solids (baked)
FEATURE [Part::Feature] Face016
  Placement = pos=(0,0,1.5) rot=(0,0,1;0rad)
  shape: bbox 8.801 x 22 x 2.006e-07 mm, 1 faces, 0 solids (baked)
FEATURE [Part::Loft] Loft007
  Closed = false
  MaxDegree = 5
  Ruled = false
  Sections = -> [Face015,Face016]
  Solid = true
FEATURE [Part::Cylinder] Cylinder210
  Angle = 360
  AttacherType = Attacher::AttachEngine3D
  Height = 42
  Placement = pos=(166,0,-39) rot=(0,0,1;0rad)
  Radius = 13
FEATURE [Part::MultiFuse] Fusion178  label="air-intake-upper-00"
  Placement = pos=(0.5,0,0) rot=(0,0,1;0rad)
  Refine = true
  Shapes = -> [Fillet233,Loft007,Fillet237]
FEATURE [Part::Fillet] Fillet238
  Base = -> Cylinder210
  Edges = 2 edges r=7: [Edge1,Edge3]
FEATURE [Part::Box] Box333  label="Cube559"
  AttacherType = Attacher::AttachEngine3D
  Height = 10
  Length = 32
  Placement = pos=(151,-16,2) rot=(0,0,1;0rad)
  Width = 32
FEATURE [Part::Box] Box334  label="Cube560"
  AttacherType = Attacher::AttachEngine3D
  Height = 10
  Length = 32
  Placement = pos=(151,-16,-48) rot=(0,0,1;0rad)
  Width = 32
FEATURE [Part::MultiFuse] Fusion179
  Refine = true
  Shapes = -> [Box334,Box333]
FEATURE [Part::Cut] Cut359  label="Cut712"
  Base = -> Fillet238
  Placement = pos=(1,31,0) rot=(0,0,1;0rad)
  Refine = true
  Tool = -> Fusion179
FEATURE [Part::Feature] Face017
  Placement = pos=(0,0,-2) rot=(0,0,1;0rad)
  shape: bbox 22.75 x 20.11 x 2e-07 mm, 1 faces, 0 solids (baked)
FEATURE [Part::Box] Box335  label="Cube561"
  AttacherType = Attacher::AttachEngine3D
  Height = 8
  Length = 10
  Placement = pos=(154,23,-7) rot=(0,0,1;0rad)
  Width = 16
FEATURE [Part::Fillet] Fillet239
  Base = -> Box335
  Edges = 4 edges r=1: [Edge9,Edge10,Edge11,Edge12]
FEATURE [Part::Feature] Face018
  shape: bbox 2.006e-07 x 17.6 x 8.801 mm, 1 faces, 0 solids (baked)
FEATURE [Part::Loft] Loft008
  Closed = false
  MaxDegree = 5
  Ruled = false
  Sections = -> [Face017,Face018]
  Solid = true
FEATURE [Part::MultiFuse] Fusion180  label="air-intake-lower-00"
  Placement = pos=(0.5,0,0) rot=(0,0,1;0rad)
  Refine = true
  Shapes = -> [Fillet239,Loft008,Cut359]
FEATURE [Part::Box] Box336  label="Cube562"
  AttacherType = Attacher::AttachEngine3D
  Height = 10
  Length = 10
  Placement = pos=(-2,71,-23) rot=(0,0,1;0rad)
  Width = 28
FEATURE [Part::Fillet] Fillet240
  Base = -> Box336
  Edges = 4 edges r=1: [Edge9,Edge10,Edge11,Edge12]
  Placement = pos=(0,0,1) rot=(0,0,1;0rad)
FEATURE [Part::Cut] Cut360  label="Cut713"
  Base = -> Cut182
  Refine = true
  Tool = -> Fillet240
FEATURE [Part::Box] Box337  label="Cube563"
  AttacherType = Attacher::AttachEngine3D
  Height = 10
  Length = 9.5
  Placement = pos=(-2,72,-22) rot=(0,0,1;0rad)
  Width = 26
FEATURE [Part::Box] Box338  label="Cube564"
  AttacherType = Attacher::AttachEngine3D
  Height = 8
  Length = 8
  Placement = pos=(-2,71,-21) rot=(0,0,1;0rad)
  Width = 28
FEATURE [Part::Cut] Cut361  label="Cut714"
  Base = -> Box337
  Refine = true
  Tool = -> Box338
FEATURE [Part::Fillet] Fillet241
  Base = -> Cut361
  Edges = 4 edges r=3: [Edge1,Edge3,Edge7,Edge16]
FEATURE [Part::Cylinder] Cylinder211
  Angle = 360
  AttacherType = Attacher::AttachEngine3D
  Height = 10
  Placement = pos=(2,85,-22) rot=(0,0,1;0rad)
  Radius = 1.6
FEATURE [Part::Cylinder] Cylinder212
  Angle = 360
  AttacherType = Attacher::AttachEngine3D
  Height = 10
  Placement = pos=(-2,85,-22) rot=(0,0,-1;1.5708rad)
  Radius = 10
FEATURE [Part::Box] Box339  label="Cube565"
  AttacherType = Attacher::AttachEngine3D
  Height = 8
  Length = 10
  Placement = pos=(-9,75,-21) rot=(0,0,1;0rad)
  Width = 20
FEATURE [Part::Cut] Cut362  label="Cut715"
  Base = -> Cylinder212
  Refine = true
  Tool = -> Box339
FEATURE [Part::Cylinder] Cylinder213
  Angle = 360
  AttacherType = Attacher::AttachEngine3D
  Height = 8
  Placement = pos=(-1,85,-21) rot=(0,0,-1;1.5708rad)
  Radius = 8.5
FEATURE [Part::Cut] Cut363  label="Cut716"
  Base = -> Cut362
  Refine = true
  Tool = -> Cylinder213
FEATURE [Part::MultiFuse] Fusion181
  Refine = true
  Shapes = -> [Fillet241,Cut363]
FEATURE [Part::Cylinder] Cylinder214
  Angle = 360
  AttacherType = Attacher::AttachEngine3D
  Height = 9
  Placement = pos=(2,85,-31) rot=(0,0,1;0rad)
  Radius = 3
FEATURE [Part::MultiFuse] Fusion182
  Refine = true
  Shapes = -> [Cut360,Cylinder214]
FEATURE [Part::Cylinder] Cylinder215
  Angle = 360
  AttacherType = Attacher::AttachEngine3D
  Height = 21
  Placement = pos=(2,85,-31) rot=(0,0,1;0rad)
  Radius = 1.6
FEATURE [Part::Cut] Cut364  label="bumper-01"
  Base = -> Fusion182
  Refine = true
  Tool = -> Cylinder215
FEATURE [Part::Cut] Cut365  label="Cut717"
  Base = -> Fusion181
  Placement = pos=(0.5,0,0) rot=(0,0,1;0rad)
  Refine = true
  Tool = -> Cylinder211
FEATURE [Part::Box] Box340  label="Cube566"
  AttacherType = Attacher::AttachEngine3D
  Height = 10
  Length = 10
  Placement = pos=(8,75,-22) rot=(0,0,1;0rad)
  Width = 20
FEATURE [Part::Cut] Cut366  label="bumper-insert-00"
  Base = -> Cut365
  Refine = true
  Tool = -> Box340
FEATURE [Part::Box] Box342  label="Cube568"
  AttacherType = Attacher::AttachEngine3D
  Height = 1.3
  Length = 25
  Placement = pos=(58,61,125.5) rot=(0,0,1;0rad)
  Width = 48
FEATURE [Part::Cylinder] Cylinder216
  Angle = 360
  AttacherType = Attacher::AttachEngine3D
  Height = 10
  Placement = pos=(118,31,59.5) rot=(0,1,0;1.5708rad)
  Radius = 1.3
FEATURE [Part::Cylinder] Cylinder217
  Angle = 360
  AttacherType = Attacher::AttachEngine3D
  Height = 10
  Placement = pos=(118,31,46.5) rot=(0,1,0;1.5708rad)
  Radius = 1.3
FEATURE [Part::MultiFuse] Fusion184
  Refine = true
  Shapes = -> [Cylinder216,Cylinder217]
FEATURE [Part::Cylinder] Cylinder218
  Angle = 360
  AttacherType = Attacher::AttachEngine3D
  Height = 10
  Placement = pos=(118,31,46.5) rot=(0,1,0;1.5708rad)
  Radius = 0.9
FEATURE [Part::Cylinder] Cylinder219
  Angle = 360
  AttacherType = Attacher::AttachEngine3D
  Height = 10
  Placement = pos=(118,31,59.5) rot=(0,1,0;1.5708rad)
  Radius = 0.9
FEATURE [Part::MultiFuse] Fusion185
  Placement = pos=(4,0,0) rot=(0,0,1;0rad)
  Refine = true
  Shapes = -> [Cylinder219,Cylinder218]
FEATURE [Part::Cylinder] Cylinder220
  Angle = 360
  AttacherType = Attacher::AttachEngine3D
  Height = 2
  Placement = pos=(118,31,59.5) rot=(0,1,0;1.5708rad)
  Radius = 2
FEATURE [Part::Cylinder] Cylinder221
  Angle = 360
  AttacherType = Attacher::AttachEngine3D
  Height = 2
  Placement = pos=(118,31,46.5) rot=(0,1,0;1.5708rad)
  Radius = 2
FEATURE [Part::MultiFuse] Fusion186
  Placement = pos=(8,0,0) rot=(0,0,1;0rad)
  Refine = true
  Shapes = -> [Cylinder220,Cylinder221]
FEATURE [Part::MultiFuse] Fusion187
  Refine = true
  Shapes = -> [Fusion178,Fusion186]
FEATURE [Part::Cut] Cut387  label="air-intake-upper-01"
  Base = -> Fusion187
  Refine = true
  Tool = -> Fusion185
FEATURE [Part::Box] Box370  label="Cube596"
  AttacherType = Attacher::AttachEngine3D
  Height = 6
  Length = 2
  Placement = pos=(89,3,29) rot=(0,0,1;0rad)
  Width = 2
FEATURE [Part::Box] Box371  label="Cube597"
  AttacherType = Attacher::AttachEngine3D
  Height = 6
  Length = 2
  Placement = pos=(105,3,29) rot=(0,0,1;0rad)
  Width = 2
FEATURE [Part::MultiFuse] Fusion188
  Refine = true
  Shapes = -> [Box370,Box371]
FEATURE [Part::Chamfer] Chamfer051
  Base = -> Fusion188
  Edges = 2 edges r=1.99: [Edge8,Edge20]
FEATURE [Part::Box] Box372  label="Cube598"
  AttacherType = Attacher::AttachEngine3D
  Height = 6
  Length = 2
  Placement = pos=(89,3,29) rot=(0,0,1;0rad)
  Width = 2
FEATURE [Part::Box] Box373  label="Cube599"
  AttacherType = Attacher::AttachEngine3D
  Height = 6
  Length = 2
  Placement = pos=(105,3,29) rot=(0,0,1;0rad)
  Width = 2
FEATURE [Part::MultiFuse] Fusion189
  Refine = true
  Shapes = -> [Box372,Box373]
FEATURE [Part::Chamfer] Chamfer052
  Base = -> Fusion189
  Edges = 2 edges r=1.99: [Edge8,Edge20]
FEATURE [Part::Mirroring] Part__Mirroring028  label="Chamfer052 (Mirror #23)"
  Base = (0,0,0)
  Normal = (0,1,0)
  Placement = pos=(0,170,0) rot=(0,0,1;0rad)
  Source = -> Chamfer052
FEATURE [Part::Cut] Cut388  label="Cut718"
  Base = -> Cut312
  Refine = true
  Tool = -> Fusion184
FEATURE [Part::MultiFuse] Fusion190  label="cab-lower-part-03"
  Refine = true
  Shapes = -> [Cut388,Chamfer051,Part__Mirroring028]
FEATURE [Part::Box] Box374  label="Cube600"
  AttacherType = Attacher::AttachEngine3D
  Height = 1
  Length = 2
  Placement = pos=(14,4,0) rot=(0,0,1;0rad)
  Width = 1
FEATURE [Part::Box] Box376  label="Cube602"
  AttacherType = Attacher::AttachEngine3D
  Height = 1
  Length = 2
  Placement = pos=(14,4,32) rot=(0,0,1;0rad)
  Width = 1
FEATURE [Part::Box] Box377  label="Cube603"
  AttacherType = Attacher::AttachEngine3D
  Height = 1
  Length = 2
  Placement = pos=(14,1,60) rot=(0,0,1;0rad)
  Width = 1
FEATURE [Part::Box] Box378  label="Cube604"
  AttacherType = Attacher::AttachEngine3D
  Height = 1
  Length = 2
  Placement = pos=(81,1,32) rot=(0,0,1;0rad)
  Width = 1
FEATURE [Part::Box] Box379  label="Cube605"
  AttacherType = Attacher::AttachEngine3D
  Height = 1
  Length = 2
  Placement = pos=(81,1,60) rot=(0,0,1;0rad)
  Width = 1
FEATURE [Part::Box] Box380  label="Cube606"
  AttacherType = Attacher::AttachEngine3D
  Height = 1
  Length = 2
  Placement = pos=(81,4,64) rot=(0,0,1;0rad)
  Width = 1
FEATURE [Part::Box] Box381  label="Cube607"
  AttacherType = Attacher::AttachEngine3D
  Height = 1
  Length = 2
  Placement = pos=(81,5,90) rot=(0,0,1;0rad)
  Width = 1
FEATURE [Part::MultiFuse] Fusion191
  Refine = true
  Shapes = -> [Box374,Box379,Box377,Box376,Box378]
FEATURE [Part::Box] Box382  label="Cube608"
  AttacherType = Attacher::AttachEngine3D
  Height = 1
  Length = 2
  Placement = pos=(81,1,60) rot=(0,0,1;0rad)
  Width = 1
FEATURE [Part::Box] Box383  label="Cube609"
  AttacherType = Attacher::AttachEngine3D
  Height = 1
  Length = 2
  Placement = pos=(14,1,60) rot=(0,0,1;0rad)
  Width = 1
FEATURE [Part::Box] Box384  label="Cube610"
  AttacherType = Attacher::AttachEngine3D
  Height = 1
  Length = 2
  Placement = pos=(14,4,32) rot=(0,0,1;0rad)
  Width = 1
FEATURE [Part::Box] Box385  label="Cube611"
  AttacherType = Attacher::AttachEngine3D
  Height = 1
  Length = 2
  Placement = pos=(81,1,32) rot=(0,0,1;0rad)
  Width = 1
FEATURE [Part::Box] Box386  label="Cube612"
  AttacherType = Attacher::AttachEngine3D
  Height = 1
  Length = 2
  Placement = pos=(14,4,0) rot=(0,0,1;0rad)
  Width = 1
FEATURE [Part::MultiFuse] Fusion192
  Refine = true
  Shapes = -> [Box386,Box382,Box383,Box384,Box385]
FEATURE [Part::Mirroring] Part__Mirroring029  label="Fusion192 (Mirror #24)"
  Base = (0,0,0)
  Normal = (0,1,0)
  Placement = pos=(0,170,0) rot=(0,0,1;0rad)
  Source = -> Fusion192
FEATURE [Part::Box] Box387  label="Cube613"
  AttacherType = Attacher::AttachEngine3D
  Height = 1
  Length = 2
  Placement = pos=(80,5,115.5) rot=(0,0,1;0rad)
  Width = 2
FEATURE [Part::Box] Box388  label="Cube614"
  AttacherType = Attacher::AttachEngine3D
  Height = 1
  Length = 2
  Placement = pos=(15,5,64) rot=(0,0,1;0rad)
  Width = 1
FEATURE [Part::Box] Box389  label="Cube615"
  AttacherType = Attacher::AttachEngine3D
  Height = 1
  Length = 2
  Placement = pos=(21,5,90) rot=(0,0,1;0rad)
  Width = 1
FEATURE [Part::Box] Box390  label="Cube616"
  AttacherType = Attacher::AttachEngine3D
  Height = 1
  Length = 2
  Placement = pos=(26.5,5.4,115.5) rot=(0,0,1;0rad)
  Width = 2
FEATURE [Part::Box] Box391  label="Cube617"
  AttacherType = Attacher::AttachEngine3D
  Height = 1
  Length = 2
  Placement = pos=(37,6,115.5) rot=(0,0,1;0rad)
  Width = 1
FEATURE [Part::Box] Box392  label="Cube618"
  AttacherType = Attacher::AttachEngine3D
  Height = 1
  Length = 2
  Placement = pos=(53,6,115.5) rot=(0,0,1;0rad)
  Width = 1
FEATURE [Part::Box] Box393  label="Cube619"
  AttacherType = Attacher::AttachEngine3D
  Height = 1
  Length = 2
  Placement = pos=(70,6,115.5) rot=(0,0,1;0rad)
  Width = 1
FEATURE [Part::MultiFuse] Fusion194
  Refine = true
  Shapes = -> [Box380,Box381,Box387,Box388,Box389,Box390,Box391,Box392,Box393]
FEATURE [Part::Box] Box394  label="Cube620"
  AttacherType = Attacher::AttachEngine3D
  Height = 1
  Length = 2
  Placement = pos=(80,5,115.5) rot=(0,0,1;0rad)
  Width = 2
FEATURE [Part::Box] Box395  label="Cube621"
  AttacherType = Attacher::AttachEngine3D
  Height = 1
  Length = 2
  Placement = pos=(53,6,115.5) rot=(0,0,1;0rad)
  Width = 1
FEATURE [Part::Box] Box396  label="Cube622"
  AttacherType = Attacher::AttachEngine3D
  Height = 1
  Length = 2
  Placement = pos=(70,6,115.5) rot=(0,0,1;0rad)
  Width = 1
FEATURE [Part::Box] Box397  label="Cube623"
  AttacherType = Attacher::AttachEngine3D
  Height = 1
  Length = 2
  Placement = pos=(15,5,64) rot=(0,0,1;0rad)
  Width = 1
FEATURE [Part::Box] Box398  label="Cube624"
  AttacherType = Attacher::AttachEngine3D
  Height = 1
  Length = 2
  Placement = pos=(21,5,90) rot=(0,0,1;0rad)
  Width = 1
FEATURE [Part::Box] Box399  label="Cube625"
  AttacherType = Attacher::AttachEngine3D
  Height = 1
  Length = 2
  Placement = pos=(37,6,115.5) rot=(0,0,1;0rad)
  Width = 1
FEATURE [Part::Box] Box400  label="Cube626"
  AttacherType = Attacher::AttachEngine3D
  Height = 1
  Length = 2
  Placement = pos=(26.5,5.4,115.5) rot=(0,0,1;0rad)
  Width = 2
FEATURE [Part::Box] Box401  label="Cube627"
  AttacherType = Attacher::AttachEngine3D
  Height = 1
  Length = 2
  Placement = pos=(81,5,90) rot=(0,0,1;0rad)
  Width = 1
FEATURE [Part::Box] Box402  label="Cube628"
  AttacherType = Attacher::AttachEngine3D
  Height = 1
  Length = 2
  Placement = pos=(81,4,64) rot=(0,0,1;0rad)
  Width = 1
FEATURE [Part::MultiFuse] Fusion195
  Refine = true
  Shapes = -> [Box402,Box401,Box394,Box397,Box398,Box400,Box399,Box395,Box396]
FEATURE [Part::Mirroring] Part__Mirroring030  label="Fusion195 (Mirror #25)"
  Base = (0,0,0)
  Normal = (0,1,0)
  Placement = pos=(0,170,0) rot=(0,0,1;0rad)
  Source = -> Fusion195
FEATURE [Part::MultiFuse] Fusion196  label="doors-retainers-upper-part"
  Refine = true
  Shapes = -> [Fusion194,Part__Mirroring030]
FEATURE [Part::Feature] Face023
  shape: bbox 15.41 x 11.89 x 2e-07 mm, 1 faces, 0 solids (baked)
FEATURE [Part::Feature] Face024
  shape: bbox 6.072 x 6.626 x 3.506 mm, 1 faces, 0 solids (baked)
FEATURE [Part::Loft] Loft011
  Closed = false
  MaxDegree = 5
  Ruled = false
  Sections = -> [Face023,Face024]
  Solid = true
FEATURE [Part::Cut] Cut389  label="air-intake-lower-01"
  Base = -> Fusion180
  Refine = true
  Tool = -> Loft011
FEATURE [Part::MultiFuse] Fusion197  label="doors-retainers-lower-part"
  Refine = true
  Shapes = -> [Part__Mirroring029,Fusion191]
FEATURE [Part::Chamfer] Chamfer053  label="cab-lower-part-04"
  Base = -> Fusion190
  Edges = 1 edges r=0.9: [Edge492]
FEATURE [Part::Cylinder] Cylinder222
  Angle = 360
  AttacherType = Attacher::AttachEngine3D
  Height = 10
  Placement = pos=(15,15,10) rot=(0,0,1;0rad)
  Radius = 13.5
FEATURE [Part::Cylinder] Cylinder223
  Angle = 360
  AttacherType = Attacher::AttachEngine3D
  Height = 10
  Placement = pos=(15,15,10) rot=(0,0,1;0rad)
  Radius = 13.5
FEATURE [Part::Cut] Cut390  label="deflector-left-02"
  Base = -> Cut260
  Refine = true
  Tool = -> Cylinder222
FEATURE [Part::Cut] Cut391  label="Cut719"
  Base = -> Cut264
  Refine = true
  Tool = -> Cylinder223
FEATURE [Part::Mirroring] Part__Mirroring031  label="deflector-right-02"
  Base = (0,0,0)
  Normal = (0,1,0)
  Placement = pos=(0,170,0) rot=(0,0,1;0rad)
  Source = -> Cut391
FEATURE [Part::Cylinder] Cylinder224
  Angle = 360
  AttacherType = Attacher::AttachEngine3D
  Height = 25
  Placement = pos=(15,15,5) rot=(0,0,1;0rad)
  Radius = 13.5
FEATURE [Part::Cylinder] Cylinder225
  Angle = 360
  AttacherType = Attacher::AttachEngine3D
  Height = 25
  Placement = pos=(15,15,5) rot=(0,0,1;0rad)
  Radius = 15.5
FEATURE [Part::Cut] Cut392  label="Cut720"
  Base = -> Cylinder225
  Refine = true
  Tool = -> Cylinder224
FEATURE [Part::Cylinder] Cylinder226
  Angle = 360
  AttacherType = Attacher::AttachEngine3D
  Height = 25
  Placement = pos=(15,15,5) rot=(0,0,1;0rad)
  Radius = 13.5
FEATURE [Part::Cylinder] Cylinder227
  Angle = 360
  AttacherType = Attacher::AttachEngine3D
  Height = 25
  Placement = pos=(15,15,5) rot=(0,0,1;0rad)
  Radius = 15.5
FEATURE [Part::Cut] Cut393  label="Cut721"
  Base = -> Cylinder227
  Refine = true
  Tool = -> Cylinder226
FEATURE [Part::Mirroring] Part__Mirroring032  label="Cut522 (Mirror #25)"
  Base = (0,0,0)
  Normal = (0,1,0)
  Placement = pos=(0,170,0) rot=(0,0,1;0rad)
  Source = -> Cut393
FEATURE [Part::MultiFuse] Fusion198
  Placement = pos=(-0.5,0,0) rot=(0,0,1;0rad)
  Refine = true
  Shapes = -> [Part__Mirroring032,Cut392]
FEATURE [Part::Cut] Cut394  label="Cut722"
  Base = -> Cut094
  Refine = true
  Tool = -> Fusion198
FEATURE [Part::MultiFuse] Fusion199
  Refine = true
  Shapes = -> [Cut099,Cut394]
FEATURE [Part::Cut] Cut395  label="Cut723"
  Base = -> Fusion199
  Refine = true
  Tool = -> Fusion065
FEATURE [Part::Chamfer] Chamfer054
  Base = -> Cut395
  Edges = 5 edges r=1: [Edge9,Edge64,Edge71,Edge89,Edge97]
FEATURE [Part::Cylinder] Cylinder228
  Angle = 360
  AttacherType = Attacher::AttachEngine3D
  Height = 10
  Placement = pos=(30,11,114) rot=(1,0,0;1.5708rad)
  Radius = 1
FEATURE [Part::Cylinder] Cylinder229
  Angle = 360
  AttacherType = Attacher::AttachEngine3D
  Height = 10
  Placement = pos=(26,11,66) rot=(1,0,0;1.5708rad)
  Radius = 1
FEATURE [Part::MultiFuse] Fusion202
  Refine = true
  Shapes = -> [Cylinder228,Cylinder229]
FEATURE [Part::Cylinder] Cylinder230
  Angle = 360
  AttacherType = Attacher::AttachEngine3D
  Height = 10
  Placement = pos=(26,11,66) rot=(1,0,0;1.5708rad)
  Radius = 1
FEATURE [Part::Cylinder] Cylinder231
  Angle = 360
  AttacherType = Attacher::AttachEngine3D
  Height = 10
  Placement = pos=(30,11,114) rot=(1,0,0;1.5708rad)
  Radius = 1
FEATURE [Part::MultiFuse] Fusion203
  Refine = true
  Shapes = -> [Cylinder231,Cylinder230]
FEATURE [Part::Mirroring] Part__Mirroring033  label="Fusion203 (Mirror #26)"
  Base = (0,0,0)
  Normal = (0,1,0)
  Placement = pos=(0,170,0) rot=(0,0,1;0rad)
  Source = -> Fusion203
FEATURE [Part::MultiFuse] Fusion204
  Refine = true
  Shapes = -> [Fusion202,Part__Mirroring033]
FEATURE [Part::Cylinder] Cylinder232
  Angle = 360
  AttacherType = Attacher::AttachEngine3D
  Height = 10
  Placement = pos=(119,65,45) rot=(0,1,0;1.5708rad)
  Radius = 1
FEATURE [Part::Cylinder] Cylinder233
  Angle = 360
  AttacherType = Attacher::AttachEngine3D
  Height = 10
  Placement = pos=(119,105,45) rot=(0,1,0;1.5708rad)
  Radius = 1
FEATURE [Part::MultiFuse] Fusion205
  Placement = pos=(0,0,2) rot=(0,0,1;0rad)
  Refine = true
  Shapes = -> [Cylinder232,Cylinder233]
FEATURE [Part::Cut] Cut398  label="cab-lower-part-05"
  Base = -> Chamfer053
  Refine = true
  Tool = -> Fusion205
FEATURE [Part::Cylinder] Cylinder236
  Angle = 79
  AttacherType = Attacher::AttachEngine3D
  Height = 62
  Placement = pos=(25,21,0) rot=(0,0,1;3.28122rad)
  Radius = 29
FEATURE [Part::Cylinder] Cylinder237
  Angle = 360
  AttacherType = Attacher::AttachEngine3D
  Height = 62
  Placement = pos=(25,21,0) rot=(0,0,1;0rad)
  Radius = 18
FEATURE [Part::Cut] Cut401  label="Cut724"
  Base = -> Cylinder236
  Refine = true
  Tool = -> Cylinder237
FEATURE [Part::Box] Box406  label="Cube632"
  AttacherType = Attacher::AttachEngine3D
  Height = 2
  Length = 48
  Placement = pos=(5,3,0) rot=(0,0,1;0rad)
  Width = 15
FEATURE [Part::Cylinder] Cylinder238
  Angle = 360
  AttacherType = Attacher::AttachEngine3D
  Height = 62
  Placement = pos=(25,21,0) rot=(0,0,1;0rad)
  Radius = 16.5
FEATURE [Part::Cylinder] Cylinder239
  Angle = 46
  AttacherType = Attacher::AttachEngine3D
  Height = 62
  Placement = pos=(25,21,0) rot=(0,0,1;3.3074rad)
  Radius = 18
FEATURE [Part::Cut] Cut402  label="Cut725"
  Base = -> Cylinder239
  Refine = true
  Tool = -> Cylinder238
FEATURE [Part::Cut] Cut403  label="Cut726"
  Base = -> Box406
  Refine = true
  Tool = -> Cut401
FEATURE [Part::Box] Box407  label="Cube633"
  AttacherType = Attacher::AttachEngine3D
  Height = 62
  Length = 3
  Placement = pos=(6,18,0) rot=(0,0,1;0rad)
  Width = 1
FEATURE [Part::Cut] Cut404  label="Cut727"
  Base = -> Cut402
  Refine = true
  Tool = -> Box407
FEATURE [Part::Cylinder] Cylinder240
  Angle = 360
  AttacherType = Attacher::AttachEngine3D
  Height = 22
  Placement = pos=(98,18,-23) rot=(1,0,0;1.5708rad)
  Radius = 52
FEATURE [Part::Cut] Cut405  label="Cut728"
  Base = -> Cut403
  Refine = true
  Tool = -> Cylinder240
FEATURE [Part::Cylinder] Cylinder241
  Angle = 360
  AttacherType = Attacher::AttachEngine3D
  Height = 13
  Placement = pos=(11.9886,10.7385,16) rot=(0.884029,-0.330525,-0.330525;1.69375rad)
  Radius = 1.2
FEATURE [Part::Cylinder] Cylinder242
  Angle = 360
  AttacherType = Attacher::AttachEngine3D
  Height = 13
  Placement = pos=(11.9886,10.7385,51) rot=(0.884029,-0.330525,-0.330525;1.69375rad)
  Radius = 1.2
FEATURE [Part::MultiFuse] Fusion206
  Placement = pos=(0.87,1,0) rot=(0,0,1;0rad)
  Refine = true
  Shapes = -> [Cylinder241,Cylinder242]
FEATURE [Part::Cylinder] Cylinder243
  Angle = 360
  AttacherType = Attacher::AttachEngine3D
  Height = 1.6
  Placement = pos=(11.9886,10.7385,16) rot=(0.884029,-0.330525,-0.330525;1.69375rad)
  Radius = 2
FEATURE [Part::Cylinder] Cylinder244
  Angle = 360
  AttacherType = Attacher::AttachEngine3D
  Height = 1.6
  Placement = pos=(11.9886,10.7385,51) rot=(0.884029,-0.330525,-0.330525;1.69375rad)
  Radius = 2
FEATURE [Part::MultiFuse] Fusion207
  Placement = pos=(0.87,1,0) rot=(0,0,1;0rad)
  Refine = true
  Shapes = -> [Cylinder243,Cylinder244]
FEATURE [Part::MultiFuse] Fusion208
  Refine = true
  Shapes = -> [Cut404,Cut405,Fusion207]
FEATURE [Part::Cut] Cut406  label="Cut729"
  Base = -> Fusion208
  Refine = true
  Tool = -> Fusion206
FEATURE [Part::Cylinder] Cylinder245
  Angle = 360
  AttacherType = Attacher::AttachEngine3D
  Height = 10
  Placement = pos=(18,15,-5) rot=(0,0,1;0rad)
  Radius = 0.9
FEATURE [Part::Cylinder] Cylinder246
  Angle = 360
  AttacherType = Attacher::AttachEngine3D
  Height = 10
  Placement = pos=(49,15,-5) rot=(0,0,1;0rad)
  Radius = 0.9
FEATURE [Part::MultiFuse] Fusion209
  Refine = true
  Shapes = -> [Cylinder245,Cylinder246]
FEATURE [Part::Cylinder] Cylinder247
  Angle = 360
  AttacherType = Attacher::AttachEngine3D
  Height = 10
  Placement = pos=(18,15,-5) rot=(0,0,1;0rad)
  Radius = 1.2
FEATURE [Part::Cylinder] Cylinder248
  Angle = 360
  AttacherType = Attacher::AttachEngine3D
  Height = 10
  Placement = pos=(49,15,-5) rot=(0,0,1;0rad)
  Radius = 1.2
FEATURE [Part::MultiFuse] Fusion210
  Refine = true
  Shapes = -> [Cylinder247,Cylinder248]
FEATURE [Part::Cut] Cut407  label="inner-door-swing-arm-left"
  Base = -> Cut406
  Refine = true
  Tool = -> Fusion210
FEATURE [Part::Cylinder] Cylinder249
  Angle = 360
  AttacherType = Attacher::AttachEngine3D
  Height = 10
  Placement = pos=(18,15,-5) rot=(0,0,1;0rad)
  Radius = 0.9
FEATURE [Part::Cylinder] Cylinder250
  Angle = 360
  AttacherType = Attacher::AttachEngine3D
  Height = 10
  Placement = pos=(49,15,-5) rot=(0,0,1;0rad)
  Radius = 0.9
FEATURE [Part::MultiFuse] Fusion211
  Refine = true
  Shapes = -> [Cylinder249,Cylinder250]
FEATURE [Part::Mirroring] Part__Mirroring034  label="Fusion211 (Mirror #27)"
  Base = (0,0,0)
  Normal = (0,1,0)
  Placement = pos=(0,170,0) rot=(0,0,1;0rad)
  Source = -> Fusion211
FEATURE [Part::Cut] Cut408  label="wing-left-01"
  Base = -> Part__Mirroring019
  Refine = true
  Tool = -> Fusion209
FEATURE [Part::Cut] Cut409  label="wing-right-01"
  Base = -> Fusion147
  Refine = true
  Tool = -> Part__Mirroring034
FEATURE [Part::Cut] Cut421  label="Cut730"
  Base = -> Fillet123
  Refine = true
  Tool = -> Fusion204
FEATURE [Part::Box] Box414  label="Cube639"
  AttacherType = Attacher::AttachEngine3D
  Height = 5
  Length = 105
  Placement = pos=(19.5,5.5,117) rot=(0,0,1;0rad)
  Width = 159
FEATURE [Part::Box] Box415  label="Cube640"
  AttacherType = Attacher::AttachEngine3D
  Height = 5.1
  Length = 100
  Placement = pos=(19.5,5.5,122.5) rot=(0,0,1;0rad)
  Width = 159
FEATURE [Part::Fillet] Fillet261
  Base = -> Box415
  Edges = 2 edges r=10: [Edge1,Edge3]
FEATURE [Part::Fillet] Fillet262
  Base = -> Fillet261
  Edges = 2 edges r=4.5: [Edge17,Edge18]
FEATURE [Part::Fillet] Fillet260
  Base = -> Fillet262
  Edges = 4 edges r=5: [Edge1,Edge4,Edge5,Edge8]
  Placement = pos=(0.7,0,-2) rot=(0,0,1;0rad)
FEATURE [Part::Box] Box416  label="Cube641"
  AttacherType = Attacher::AttachEngine3D
  Height = 5.1
  Length = 95
  Placement = pos=(23,7.5,122.5) rot=(0,0,1;0rad)
  Width = 155
FEATURE [Part::Fillet] Fillet263
  Base = -> Box416
  Edges = 2 edges r=3: [Edge5,Edge7]
FEATURE [Part::Fillet] Fillet264
  Base = -> Fillet263
  Edges = 2 edges r=8: [Edge17,Edge18]
FEATURE [Part::Fillet] Fillet265
  Base = -> Fillet264
  Edges = 1 edges r=4: [Edge4]
  Placement = pos=(0,0,-4) rot=(0,0,1;0rad)
FEATURE [Part::Cut] Cut422  label="Cut731"
  Base = -> Fillet260
  Refine = true
  Tool = -> Fillet265
FEATURE [Part::MultiFuse] Fusion228
  Refine = true
  Shapes = -> [Cut246,Cut421]
FEATURE [Part::Box] Box417  label="Cube642"
  AttacherType = Attacher::AttachEngine3D
  Height = 5.1
  Length = 105
  Placement = pos=(19.5,5.5,122) rot=(0,0,1;0rad)
  Width = 159
FEATURE [Part::Cut] Cut423  label="cab-uper-part-00"
  Base = -> Fusion228
  Refine = true
  Tool = -> Box417
FEATURE [Part::Cut] Cut424  label="cab-top-part-00"
  Base = -> Cut422
  Refine = true
  Tool = -> Box414
FEATURE [Part::Box] Box419  label="Cube644"
  AttacherType = Attacher::AttachEngine3D
  Height = 5.1
  Length = 95
  Placement = pos=(23,7.5,122.5) rot=(0,0,1;0rad)
  Width = 155
FEATURE [Part::Fillet] Fillet267
  Base = -> Box419
  Edges = 2 edges r=3: [Edge5,Edge7]
FEATURE [Part::Fillet] Fillet266
  Base = -> Fillet267
  Edges = 2 edges r=8: [Edge17,Edge18]
  Placement = pos=(0,0,-5) rot=(0,0,1;0rad)
FEATURE [Part::Cut] Cut425  label="cab-upper-part-01"
  Base = -> Cut423
  Refine = true
  Tool = -> Fillet266
FEATURE [Part::Fillet] Fillet268  label="windshield-frame"
  Base = -> Cut341
  Edges = 1 edges r=0.4: [Edge49]
  Placement = pos=(1,0,0) rot=(0,0,1;0rad)
FEATURE [Part::Box] Box421  label="Cube646"
  AttacherType = Attacher::AttachEngine3D
  Height = 3.5
  Length = 94.8
  Placement = pos=(23.1,7.6,122) rot=(0,0,1;0rad)
  Width = 154.9
FEATURE [Part::Fillet] Fillet272
  Base = -> Box421
  Edges = 2 edges r=3.5: [Edge5,Edge7]
FEATURE [Part::Fillet] Fillet273
  Base = -> Fillet272
  Edges = 2 edges r=9: [Edge17,Edge18]
  Placement = pos=(0,0,-2) rot=(0,0,1;0rad)
FEATURE [Part::Box] Box422  label="Cube647"
  AttacherType = Attacher::AttachEngine3D
  Height = 3.5
  Length = 92
  Placement = pos=(24.6,9.1,122) rot=(0,0,1;0rad)
  Width = 152
FEATURE [Part::Fillet] Fillet275
  Base = -> Box422
  Edges = 2 edges r=3: [Edge5,Edge7]
FEATURE [Part::Fillet] Fillet274
  Base = -> Fillet275
  Edges = 2 edges r=8: [Edge17,Edge18]
  Placement = pos=(0,0,-2) rot=(0,0,1;0rad)
FEATURE [Part::Cut] Cut426  label="Cut732"
  Base = -> Fillet273
  Refine = true
  Tool = -> Fillet274
FEATURE [Part::MultiFuse] Fusion229  label="cab-top-part-01"
  Refine = true
  Shapes = -> [Cut424,Cut426]
FEATURE [Part::Fillet] Fillet277
  Base = -> Box342
  Edges = 4 edges r=2.5: [Edge1,Edge3,Edge5,Edge7]
FEATURE [Part::Fillet] Fillet278  label="top-closer"
  Base = -> Fillet277
  Edges = 4 edges r=1.29: [Edge1,Edge7,Edge8,Edge11]
FEATURE [Part::Box] Box423  label="Cube648"
  AttacherType = Attacher::AttachEngine3D
  Height = 41
  Length = 57.5
  Placement = pos=(19.5,1,70.5) rot=(0,0,1;0rad)
  Width = 1
FEATURE [Part::Box] Box424  label="Cube649"
  AttacherType = Attacher::AttachEngine3D
  Height = 48
  Length = 11
  Placement = pos=(9,0,70) rot=(0,1,0;0.20944rad)
  Width = 5
FEATURE [Part::Cut] Cut427  label="Cut733"
  Base = -> Box423
  Placement = pos=(0,-0.5,0) rot=(0,0,1;0rad)
  Refine = true
  Tool = -> Box424
FEATURE [Part::Box] Box425  label="Cube650"
  AttacherType = Attacher::AttachEngine3D
  Height = 39
  Length = 59
  Placement = pos=(19,0,73.5) rot=(0,0,1;0rad)
  Width = 0.5
FEATURE [Part::Box] Box426  label="Cube651"
  AttacherType = Attacher::AttachEngine3D
  Height = 48
  Length = 11
  Placement = pos=(8,0,70) rot=(0,1,0;0.20944rad)
  Width = 5
FEATURE [Part::Cut] Cut428  label="Cut734"
  Base = -> Box425
  Refine = true
  Tool = -> Box426
FEATURE [Part::Box] Box427  label="Cube652"
  AttacherType = Attacher::AttachEngine3D
  Height = 35
  Length = 17
  Placement = pos=(20.5,0,75.5) rot=(0,0,1;0rad)
  Width = 5
FEATURE [Part::Box] Box428  label="Cube653"
  AttacherType = Attacher::AttachEngine3D
  Height = 48
  Length = 11
  Placement = pos=(9.5,0,70) rot=(0,1,0;0.20944rad)
  Width = 5
FEATURE [Part::Cut] Cut429  label="Cut735"
  Base = -> Box427
  Refine = true
  Tool = -> Box428
FEATURE [Part::Box] Box429  label="Cube654"
  AttacherType = Attacher::AttachEngine3D
  Height = 36
  Length = 37.5
  Placement = pos=(39,0,75) rot=(0,0,1;0rad)
  Width = 5
FEATURE [Part::Fillet] Fillet280
  Base = -> Box429
  Edges = 2 edges r=2.5: [Edge6,Edge8]
FEATURE [Part::Fillet] Fillet281
  Base = -> Fillet280
  Edges = 2 edges r=1: [Edge17,Edge18]
FEATURE [Part::Fillet] Fillet282
  Base = -> Cut428
  Edges = 4 edges r=3: [Edge6,Edge7,Edge8,Edge11]
FEATURE [Part::Fillet] Fillet283
  Base = -> Cut427
  Edges = 4 edges r=3: [Edge6,Edge7,Edge8,Edge11]
  Placement = pos=(0,0.2,0) rot=(0,0,1;0rad)
FEATURE [Part::Fillet] Fillet284
  Base = -> Fillet282
  Edges = 2 edges r=0.49: [Edge4,Edge5]
FEATURE [Part::Fillet] Fillet285
  Base = -> Cut429
  Edges = 4 edges r=2.5: [Edge6,Edge7,Edge8,Edge11]
FEATURE [Part::MultiFuse] Fusion230
  Refine = true
  Shapes = -> [Fillet281,Fillet285]
FEATURE [Part::Box] Box430  label="Cube655"
  AttacherType = Attacher::AttachEngine3D
  Height = 44
  Length = 59
  Placement = pos=(19,0.25,68.5) rot=(0,0,1;0rad)
  Width = 0.5
FEATURE [Part::Box] Box431  label="Cube656"
  AttacherType = Attacher::AttachEngine3D
  Height = 48
  Length = 11
  Placement = pos=(8,0,69) rot=(0,1,0;0.20944rad)
  Width = 5
FEATURE [Part::Cut] Cut431  label="Cut737"
  Base = -> Box430
  Refine = true
  Tool = -> Box431
FEATURE [Part::Fillet] Fillet288
  Base = -> Cut431
  Edges = 4 edges r=3: [Edge6,Edge7,Edge8,Edge11]
FEATURE [Part::Fillet] Fillet286
  Base = -> Fillet288
  Edges = 2 edges r=0.24: [Edge4,Edge5]
FEATURE [Part::MultiFuse] Fusion231
  Refine = true
  Shapes = -> [Fillet283,Fillet284,Fillet286]
FEATURE [Part::Cut] Cut430  label="Cut736"
  Base = -> Fusion231
  Refine = true
  Tool = -> Fusion230
FEATURE [Part::Fillet] Fillet302
  Base = -> Cut430
  Edges = 4 edges r=0.7: [Edge9,Edge13,Edge18,Edge22]
  Placement = pos=(0,0,0) rot=(-1,0,0;0.034907rad)
FEATURE [Part::MultiFuse] Fusion234  label="window-frame-front-left-01"
  Refine = true
  Shapes = -> [Fillet302,Extrude003]
FEATURE [Part::Box] Box432  label="Cube657"
  AttacherType = Attacher::AttachEngine3D
  Height = 41
  Length = 57.5
  Placement = pos=(19.5,1,70.5) rot=(0,0,1;0rad)
  Width = 1
FEATURE [Part::Box] Box433  label="Cube658"
  AttacherType = Attacher::AttachEngine3D
  Height = 48
  Length = 11
  Placement = pos=(9,0,70) rot=(0,1,0;0.20944rad)
  Width = 5
FEATURE [Part::Cut] Cut432  label="Cut738"
  Base = -> Box432
  Placement = pos=(0,-0.5,0) rot=(0,0,1;0rad)
  Refine = true
  Tool = -> Box433
FEATURE [Part::Box] Box434  label="Cube659"
  AttacherType = Attacher::AttachEngine3D
  Height = 39
  Length = 59
  Placement = pos=(19,0,73.5) rot=(0,0,1;0rad)
  Width = 0.5
FEATURE [Part::Box] Box435  label="Cube660"
  AttacherType = Attacher::AttachEngine3D
  Height = 48
  Length = 11
  Placement = pos=(8,0,70) rot=(0,1,0;0.20944rad)
  Width = 5
FEATURE [Part::Cut] Cut433  label="Cut739"
  Base = -> Box434
  Refine = true
  Tool = -> Box435
FEATURE [Part::Box] Box436  label="Cube661"
  AttacherType = Attacher::AttachEngine3D
  Height = 35
  Length = 17
  Placement = pos=(20.5,0,75.5) rot=(0,0,1;0rad)
  Width = 5
FEATURE [Part::Box] Box437  label="Cube662"
  AttacherType = Attacher::AttachEngine3D
  Height = 48
  Length = 11
  Placement = pos=(9.5,0,70) rot=(0,1,0;0.20944rad)
  Width = 5
FEATURE [Part::Cut] Cut434  label="Cut740"
  Base = -> Box436
  Refine = true
  Tool = -> Box437
FEATURE [Part::Box] Box438  label="Cube663"
  AttacherType = Attacher::AttachEngine3D
  Height = 36
  Length = 37.5
  Placement = pos=(39,0,75) rot=(0,0,1;0rad)
  Width = 5
FEATURE [Part::Fillet] Fillet304
  Base = -> Box438
  Edges = 2 edges r=2.5: [Edge6,Edge8]
FEATURE [Part::Fillet] Fillet305
  Base = -> Fillet304
  Edges = 2 edges r=1: [Edge17,Edge18]
FEATURE [Part::Fillet] Fillet306
  Base = -> Cut433
  Edges = 4 edges r=3: [Edge6,Edge7,Edge8,Edge11]
FEATURE [Part::Fillet] Fillet307
  Base = -> Cut432
  Edges = 4 edges r=3: [Edge6,Edge7,Edge8,Edge11]
  Placement = pos=(0,0.2,0) rot=(0,0,1;0rad)
FEATURE [Part::Fillet] Fillet308
  Base = -> Fillet306
  Edges = 2 edges r=0.49: [Edge4,Edge5]
FEATURE [Part::Fillet] Fillet309
  Base = -> Cut434
  Edges = 4 edges r=2.5: [Edge6,Edge7,Edge8,Edge11]
FEATURE [Part::MultiFuse] Fusion235
  Refine = true
  Shapes = -> [Fillet305,Fillet309]
FEATURE [Part::Box] Box439  label="Cube664"
  AttacherType = Attacher::AttachEngine3D
  Height = 44
  Length = 59
  Placement = pos=(19,0.25,68.5) rot=(0,0,1;0rad)
  Width = 0.5
FEATURE [Part::Box] Box440  label="Cube665"
  AttacherType = Attacher::AttachEngine3D
  Height = 48
  Length = 11
  Placement = pos=(8,0,69) rot=(0,1,0;0.20944rad)
  Width = 5
FEATURE [Part::Cut] Cut436  label="Cut742"
  Base = -> Box439
  Refine = true
  Tool = -> Box440
FEATURE [Part::Fillet] Fillet311
  Base = -> Cut436
  Edges = 4 edges r=3: [Edge6,Edge7,Edge8,Edge11]
FEATURE [Part::Fillet] Fillet310
  Base = -> Fillet311
  Edges = 2 edges r=0.24: [Edge4,Edge5]
FEATURE [Part::MultiFuse] Fusion236
  Refine = true
  Shapes = -> [Fillet307,Fillet308,Fillet310]
FEATURE [Part::Cut] Cut435  label="Cut741"
  Base = -> Fusion236
  Refine = true
  Tool = -> Fusion235
FEATURE [Part::Fillet] Fillet303
  Base = -> Cut435
  Edges = 4 edges r=0.7: [Edge9,Edge13,Edge18,Edge22]
  Placement = pos=(0,0,0) rot=(-1,0,0;0.034907rad)
FEATURE [Part::Mirroring] Part__Mirroring036  label="Fillet303 (Mirror #29)"
  Base = (0,0,0)
  Normal = (0,1,0)
  Placement = pos=(0,170,0) rot=(0,0,1;0rad)
  Source = -> Fillet303
FEATURE [Part::MultiFuse] Fusion237  label="window-frame-front-right-01"
  Refine = true
  Shapes = -> [Extrude005,Part__Mirroring036]
FEATURE [Part::Box] Box441  label="Cube666"
  AttacherType = Attacher::AttachEngine3D
  Height = 8.5
  Length = 13.5
  Width = 2
FEATURE [Part::Fillet] Fillet313
  Base = -> Box441
  Edges = 4 edges r=2: [Edge2,Edge4,Edge6,Edge8]
  Placement = pos=(64.75,-1,36.75) rot=(0,0,1;0rad)
FEATURE [Part::Box] Box442  label="Cube667"
  AttacherType = Attacher::AttachEngine3D
  Height = 11
  Length = 16
  Width = 1
FEATURE [Part::Fillet] Fillet314
  Base = -> Box442
  Edges = 4 edges r=3: [Edge2,Edge4,Edge6,Edge8]
  Placement = pos=(63.5,-1,35.5) rot=(0,0,1;0rad)
FEATURE [Part::Box] Box443  label="Cube668"
  AttacherType = Attacher::AttachEngine3D
  Height = 8.5
  Length = 13.5
  Width = 2
FEATURE [Part::Fillet] Fillet315
  Base = -> Box443
  Edges = 4 edges r=2: [Edge2,Edge4,Edge6,Edge8]
  Placement = pos=(64.5,-1,36.5) rot=(0,0,1;0rad)
FEATURE [Part::Cut] Cut437  label="Cut743"
  Base = -> Fillet314
  Refine = true
  Tool = -> Fillet313
FEATURE [Part::Box] Box444  label="Cube669"
  AttacherType = Attacher::AttachEngine3D
  Height = 7.5
  Length = 12.5
  Placement = pos=(0.5,0,0.5) rot=(0,0,1;0rad)
  Width = 2
FEATURE [Part::Fillet] Fillet316
  Base = -> Box444
  Edges = 4 edges r=1.5: [Edge2,Edge4,Edge6,Edge8]
  Placement = pos=(64.5,-1,36.5) rot=(0,0,1;0rad)
FEATURE [Part::Cut] Cut438  label="Cut744"
  Base = -> Fillet315
  Placement = pos=(0.25,0,0.25) rot=(0,0,1;0rad)
  Refine = true
  Tool = -> Fillet316
FEATURE [Part::Box] Box445  label="Cube670"
  AttacherType = Attacher::AttachEngine3D
  Height = 2
  Length = 13
  Placement = pos=(65,-1,40) rot=(0,0,1;0rad)
  Width = 1
FEATURE [Part::Box] Box446  label="Cube671"
  AttacherType = Attacher::AttachEngine3D
  Height = 8
  Length = 3
  Placement = pos=(75,-1,37) rot=(0,0,1;0rad)
  Width = 2
FEATURE [Part::Fillet] Fillet317
  Base = -> Box446
  Edges = 2 edges r=1.5: [Edge6,Edge8]
FEATURE [Part::Cylinder] Cylinder276
  Angle = 360
  AttacherType = Attacher::AttachEngine3D
  Height = 1
  Placement = pos=(76.75,0,41) rot=(1,0,0;1.5708rad)
  Radius = 1.5
FEATURE [Part::MultiFuse] Fusion238
  Refine = true
  Shapes = -> [Cut438,Cut437,Fillet317,Box445]
FEATURE [Part::Cut] Cut439  label="Cut745"
  Base = -> Fusion238
  Refine = true
  Tool = -> Cylinder276
FEATURE [Part::Fillet] Fillet318  label="door-knob-left-01"
  Base = -> Cut439
  Edges = 4 edges r=0.75: [Edge4,Edge25,Edge26,Edge29]
  Placement = pos=(0,0,-3) rot=(0,0,1;0rad)
FEATURE [Part::Cylinder] Cylinder277
  Angle = 360
  AttacherType = Attacher::AttachEngine3D
  Height = 1
  Placement = pos=(76.75,0,41) rot=(1,0,0;1.5708rad)
  Radius = 1.5
FEATURE [Part::Box] Box447  label="Cube672"
  AttacherType = Attacher::AttachEngine3D
  Height = 7.5
  Length = 12.5
  Placement = pos=(0.5,0,0.5) rot=(0,0,1;0rad)
  Width = 2
FEATURE [Part::Fillet] Fillet320
  Base = -> Box447
  Edges = 4 edges r=1.5: [Edge2,Edge4,Edge6,Edge8]
  Placement = pos=(64.5,-1,36.5) rot=(0,0,1;0rad)
FEATURE [Part::Box] Box448  label="Cube673"
  AttacherType = Attacher::AttachEngine3D
  Height = 8
  Length = 3
  Placement = pos=(75,-1,37) rot=(0,0,1;0rad)
  Width = 2
FEATURE [Part::Fillet] Fillet321
  Base = -> Box448
  Edges = 2 edges r=1.5: [Edge6,Edge8]
FEATURE [Part::Box] Box449  label="Cube674"
  AttacherType = Attacher::AttachEngine3D
  Height = 2
  Length = 13
  Placement = pos=(65,-1,40) rot=(0,0,1;0rad)
  Width = 1
FEATURE [Part::Box] Box450  label="Cube675"
  AttacherType = Attacher::AttachEngine3D
  Height = 8.5
  Length = 13.5
  Width = 2
FEATURE [Part::Box] Box451  label="Cube676"
  AttacherType = Attacher::AttachEngine3D
  Height = 11
  Length = 16
  Width = 1
FEATURE [Part::Box] Box452  label="Cube677"
  AttacherType = Attacher::AttachEngine3D
  Height = 8.5
  Length = 13.5
  Width = 2
FEATURE [Part::Fillet] Fillet322
  Base = -> Box452
  Edges = 4 edges r=2: [Edge2,Edge4,Edge6,Edge8]
  Placement = pos=(64.75,-1,36.75) rot=(0,0,1;0rad)
FEATURE [Part::Fillet] Fillet323
  Base = -> Box450
  Edges = 4 edges r=2: [Edge2,Edge4,Edge6,Edge8]
  Placement = pos=(64.5,-1,36.5) rot=(0,0,1;0rad)
FEATURE [Part::Cut] Cut441  label="Cut747"
  Base = -> Fillet323
  Placement = pos=(0.25,0,0.25) rot=(0,0,1;0rad)
  Refine = true
  Tool = -> Fillet320
FEATURE [Part::Fillet] Fillet324
  Base = -> Box451
  Edges = 4 edges r=3: [Edge2,Edge4,Edge6,Edge8]
  Placement = pos=(63.5,-1,35.5) rot=(0,0,1;0rad)
FEATURE [Part::Cut] Cut442  label="Cut748"
  Base = -> Fillet324
  Refine = true
  Tool = -> Fillet322
FEATURE [Part::MultiFuse] Fusion239
  Refine = true
  Shapes = -> [Cut441,Cut442,Fillet321,Box449]
FEATURE [Part::Cut] Cut440  label="Cut746"
  Base = -> Fusion239
  Refine = true
  Tool = -> Cylinder277
FEATURE [Part::Fillet] Fillet319  label="left-door-knob-002"
  Base = -> Cut440
  Edges = 4 edges r=0.75: [Edge4,Edge25,Edge26,Edge29]
  Placement = pos=(0,0,-3) rot=(0,0,1;0rad)
FEATURE [Part::Mirroring] Part__Mirroring037  label="door-knob-right-01"
  Base = (0,0,0)
  Normal = (0,1,0)
  Placement = pos=(0,170,0) rot=(0,0,1;0rad)
  Source = -> Fillet319
FEATURE [Part::Cylinder] Cylinder278
  Angle = 22
  AttacherType = Attacher::AttachEngine3D
  Height = 166
  Placement = pos=(0,168,113) rot=(1,0,0;1.5708rad)
  Radius = 40
FEATURE [Part::Mirroring] Part__Mirroring038  label="Cylinder278 (Mirror #26)"
  Base = (0,0,0)
  Normal = (1,0,0)
  Placement = pos=(100,0,0) rot=(0,0,1;0rad)
  Source = -> Cylinder278
FEATURE [Part::Cylinder] Cylinder279
  Angle = 22
  AttacherType = Attacher::AttachEngine3D
  Height = 166
  Placement = pos=(0,168,113) rot=(1,0,0;1.5708rad)
  Radius = 28
FEATURE [Part::Mirroring] Part__Mirroring039  label="Cylinder278 (Mirror #26)001"
  Base = (0,0,0)
  Normal = (1,0,0)
  Placement = pos=(90,0,0) rot=(0,0,1;0rad)
  Source = -> Cylinder279
FEATURE [Part::Fillet] Fillet325
  Base = -> Part__Mirroring038
  Edges = 2 edges r=10: [Edge1,Edge3]
  Placement = pos=(-10,0,0) rot=(0,0,1;0rad)
FEATURE [Part::Cylinder] Cylinder280
  Angle = 22
  AttacherType = Attacher::AttachEngine3D
  Height = 164
  Placement = pos=(0,167,113) rot=(1,0,0;1.5708rad)
  Radius = 40
FEATURE [Part::Mirroring] Part__Mirroring040  label="Cylinder278 (Mirror #26)002"
  Base = (0,0,0)
  Normal = (1,0,0)
  Placement = pos=(100,0,0) rot=(0,0,1;0rad)
  Source = -> Cylinder280
FEATURE [Part::Fillet] Fillet326
  Base = -> Part__Mirroring040
  Edges = 2 edges r=9: [Edge1,Edge3]
  Placement = pos=(-8.5,0,0) rot=(0,0,1;0rad)
FEATURE [Part::Cut] Cut443
  Base = -> Fillet325
  Refine = true
  Tool = -> Fillet326
FEATURE [Part::Cut] Cut444
  Base = -> Cut443
  Placement = pos=(-54,0,12) rot=(0,1,0;0.174533rad)
  Refine = true
  Tool = -> Part__Mirroring039
FEATURE [Part::Cylinder] Cylinder281
  Angle = 13
  AttacherType = Attacher::AttachEngine3D
  Height = 66
  Placement = pos=(0,118,113) rot=(1,0,0;1.5708rad)
  Radius = 40
FEATURE [Part::Mirroring] Part__Mirroring041  label="Cylinder278 (Mirror #26)003"
  Base = (0,0,0)
  Normal = (1,0,0)
  Placement = pos=(17,0,1) rot=(0,1,0;0.331613rad)
  Source = -> Cylinder281
FEATURE [Part::Cylinder] Cylinder282
  Angle = 13
  AttacherType = Attacher::AttachEngine3D
  Height = 66
  Placement = pos=(0,118,113) rot=(1,0,0;1.5708rad)
  Radius = 38.2
FEATURE [Part::Mirroring] Part__Mirroring042  label="Cylinder278 (Mirror #26)004"
  Base = (0,0,0)
  Normal = (1,0,0)
  Placement = pos=(17,0,1) rot=(0,1,0;0.331613rad)
  Source = -> Cylinder282
FEATURE [Part::Cylinder] Cylinder283
  Angle = 360
  AttacherType = Attacher::AttachEngine3D
  Height = 4.5
  Placement = pos=(26,167,120) rot=(1,0,0;1.5708rad)
  Radius = 2.5
FEATURE [Part::Cut] Cut446  label="cab-upper-part-002"
  Refine = true
FEATURE [Part::MultiFuse] Fusion241  label="cab-top-part-002"
  Refine = true
FEATURE [Part::MultiFuse] Fusion242
  Refine = true
  Shapes = -> [Cut446,Fusion241]
FEATURE [Part::Cut] Cut447  label="Cut749"
  Base = -> Cylinder283
  Refine = true
  Tool = -> Fusion242
FEATURE [Part::Cut] Cut449  label="cab-upper-part-003"
  Refine = true
FEATURE [Part::Cylinder] Cylinder284
  Angle = 360
  AttacherType = Attacher::AttachEngine3D
  Height = 4.5
  Placement = pos=(26,167,120) rot=(1,0,0;1.5708rad)
  Radius = 2.5
FEATURE [Part::MultiFuse] Fusion243  label="cab-top-part-003"
  Refine = true
FEATURE [Part::MultiFuse] Fusion244
  Refine = true
  Shapes = -> [Cut449,Fusion243]
FEATURE [Part::Cut] Cut448  label="Cut750"
  Base = -> Cylinder284
  Refine = true
  Tool = -> Fusion244
FEATURE [Part::Mirroring] Part__Mirroring043  label="Cut612 (Mirror #31)"
  Base = (0,0,0)
  Normal = (0,1,0)
  Placement = pos=(0,170,0) rot=(0,0,1;0rad)
  Source = -> Cut448
FEATURE [Part::Cut] Cut450
  Base = -> Part__Mirroring041
  Placement = pos=(0,0,0.1) rot=(0,0,1;0rad)
  Refine = true
  Tool = -> Part__Mirroring042
FEATURE [Part::Fillet] Fillet327
  Base = -> Cut450
  Edges = 2 edges r=2: [Edge5,Edge10]
FEATURE [Part::Fillet] Fillet328
  Base = -> Fillet327
  Edges = 5 edges r=1.25: [Edge1,Edge2,Edge4,Edge5,Edge6]
FEATURE [Part::MultiFuse] Fusion245
  Refine = true
  Shapes = -> [Cut444,Fillet328]
FEATURE [Part::Cylinder] Cylinder287
  Angle = 360
  AttacherType = Attacher::AttachEngine3D
  Height = 170
  Placement = pos=(26,170,120) rot=(1,0,0;1.5708rad)
  Radius = 1
FEATURE [Part::MultiFuse] Fusion246
  Refine = true
  Shapes = -> [Cut447,Part__Mirroring043,Fusion245]
FEATURE [Part::Cut] Cut451  label="Cut751"
  Base = -> Fusion246
  Refine = true
  Tool = -> Cylinder287
FEATURE [Part::Cylinder] Cylinder288
  Angle = 22
  AttacherType = Attacher::AttachEngine3D
  Height = 2
  Placement = pos=(0,168,113) rot=(1,0,0;1.5708rad)
  Radius = 40
FEATURE [Part::Mirroring] Part__Mirroring044  label="Cylinder278 (Mirror #26)005"
  Base = (0,0,0)
  Normal = (1,0,0)
  Placement = pos=(90,0,0) rot=(0,0,1;0rad)
  Source = -> Cylinder288
FEATURE [Part::Cylinder] Cylinder289
  Angle = 22
  AttacherType = Attacher::AttachEngine3D
  Height = 2
  Placement = pos=(0,168,113) rot=(1,0,0;1.5708rad)
  Radius = 37
FEATURE [Part::Mirroring] Part__Mirroring045  label="Cylinder278 (Mirror #26)006"
  Base = (0,0,0)
  Normal = (1,0,0)
  Placement = pos=(90,0,0) rot=(0,0,1;0rad)
  Source = -> Cylinder289
FEATURE [Part::Cut] Cut452  label="Cut752"
  Base = -> Part__Mirroring044
  Placement = pos=(-54,-49,12) rot=(0,1,0;0.174533rad)
  Refine = true
  Tool = -> Part__Mirroring045
FEATURE [Part::Fillet] Fillet329
  Base = -> Cut452
  Edges = 1 edges r=3: [Edge9]
FEATURE [Part::Fillet] Fillet330
  Base = -> Fillet329
  Edges = 1 edges r=3: [Edge7]
FEATURE [Part::Cylinder] Cylinder290
  Angle = 22
  AttacherType = Attacher::AttachEngine3D
  Height = 2
  Placement = pos=(0,168,113) rot=(1,0,0;1.5708rad)
  Radius = 37
FEATURE [Part::Cylinder] Cylinder291
  Angle = 22
  AttacherType = Attacher::AttachEngine3D
  Height = 2
  Placement = pos=(0,168,113) rot=(1,0,0;1.5708rad)
  Radius = 40
FEATURE [Part::Mirroring] Part__Mirroring046  label="Cylinder278 (Mirror #26)007"
  Base = (0,0,0)
  Normal = (1,0,0)
  Placement = pos=(90,0,0) rot=(0,0,1;0rad)
  Source = -> Cylinder291
FEATURE [Part::Mirroring] Part__Mirroring047  label="Cylinder278 (Mirror #26)008"
  Base = (0,0,0)
  Normal = (1,0,0)
  Placement = pos=(90,0,0) rot=(0,0,1;0rad)
  Source = -> Cylinder290
FEATURE [Part::Cut] Cut453  label="Cut753"
  Base = -> Part__Mirroring046
  Placement = pos=(-54,-49,12) rot=(0,1,0;0.174533rad)
  Refine = true
  Tool = -> Part__Mirroring047
FEATURE [Part::Fillet] Fillet332
  Base = -> Cut453
  Edges = 1 edges r=3: [Edge9]
FEATURE [Part::Fillet] Fillet331
  Base = -> Fillet332
  Edges = 1 edges r=3: [Edge7]
  Placement = pos=(0,-66,0) rot=(0,0,1;0rad)
FEATURE [Part::MultiFuse] Fusion247  label="cab-sunvisor"
  Refine = true
  Shapes = -> [Cut451,Fillet330,Fillet331]
FEATURE [Part::Cylinder] Cylinder292
  Angle = 360
  AttacherType = Attacher::AttachEngine3D
  Height = 47
  Placement = pos=(166,0,-44) rot=(0,0,1;0rad)
  Radius = 14
FEATURE [Part::Fillet] Fillet333
  Base = -> Cylinder292
  Edges = 2 edges r=7: [Edge1,Edge3]
FEATURE [Part::Box] Box453  label="Cube678"
  AttacherType = Attacher::AttachEngine3D
  Height = 10
  Length = 32
  Placement = pos=(151,-16,2) rot=(0,0,1;0rad)
  Width = 32
FEATURE [Part::Box] Box454  label="Cube679"
  AttacherType = Attacher::AttachEngine3D
  Height = 10
  Length = 32
  Placement = pos=(151,-16,-53) rot=(0,0,1;0rad)
  Width = 32
FEATURE [Part::MultiFuse] Fusion248
  Refine = true
  Shapes = -> [Box454,Box453]
FEATURE [Part::Cut] Cut454  label="Cut754"
  Base = -> Fillet333
  Placement = pos=(7,31,0) rot=(0,0,1;0rad)
  Refine = true
  Tool = -> Fusion248
FEATURE [Part::Feature] Face025
  Placement = pos=(0,0,-2) rot=(0,0,1;0rad)
  shape: bbox 22.75 x 20.11 x 2e-07 mm, 1 faces, 0 solids (baked)
FEATURE [Part::Box] Box455  label="Cube680"
  AttacherType = Attacher::AttachEngine3D
  Height = 11
  Length = 10
  Placement = pos=(154,24,-10) rot=(0,0,1;0rad)
  Width = 14
FEATURE [Part::Fillet] Fillet334
  Base = -> Box455
  Edges = 4 edges r=4: [Edge9,Edge10,Edge11,Edge12]
  Placement = pos=(12.7075,3.6e-15,52.068) rot=(0,1,0;0.349066rad)
FEATURE [Part::Feature] Face027
  shape: bbox 15.41 x 11.89 x 2e-07 mm, 1 faces, 0 solids (baked)
FEATURE [Part::Feature] Face028
  shape: bbox 6.072 x 6.626 x 3.506 mm, 1 faces, 0 solids (baked)
FEATURE [Part::Loft] Loft013
  Closed = false
  MaxDegree = 5
  Placement = pos=(-0.5,0,0) rot=(0,0,1;0rad)
  Ruled = false
  Sections = -> [Face027,Face028]
  Solid = true
FEATURE [Part::Feature] Face029
  shape: bbox 4.139 x 15.4 x 11.37 mm, 1 faces, 0 solids (baked)
FEATURE [Part::Loft] Loft014
  Closed = false
  MaxDegree = 5
  Ruled = false
  Sections = -> [Face025,Face029]
  Solid = true
FEATURE [Part::MultiFuse] Fusion249
  Refine = true
  Shapes = -> [Fillet334,Cut454,Loft014]
FEATURE [Part::Cut] Cut455  label="Cut755"
  Base = -> Fusion249
  Refine = true
  Tool = -> Loft013
FEATURE [Part::Cylinder] Cylinder293
  Angle = 360
  AttacherType = Attacher::AttachEngine3D
  Height = 39
  Placement = pos=(166,0,-40) rot=(0,0,1;0rad)
  Radius = 12
FEATURE [Part::Chamfer] Chamfer055
  Base = -> Cylinder293
  Edges = 2 edges r=7: [Edge1,Edge3]
  Placement = pos=(7,31,0) rot=(0,0,1;0rad)
FEATURE [Part::Cut] Cut456  label="air-intake-lower-02"
  Base = -> Cut455
  Refine = true
  Tool = -> Chamfer055
FEATURE [Part::Cylinder] Cylinder294
  Angle = 26
  AttacherType = Attacher::AttachEngine3D
  Height = 166
  Placement = pos=(0,168,113) rot=(1,0,0;1.5708rad)
  Radius = 40
FEATURE [Part::Mirroring] Part__Mirroring048  label="Cylinder278 (Mirror #26)009"
  Base = (0,0,0)
  Normal = (1,0,0)
  Placement = pos=(100,0,0) rot=(0,0,1;0rad)
  Source = -> Cylinder294
FEATURE [Part::Cylinder] Cylinder295
  Angle = 26
  AttacherType = Attacher::AttachEngine3D
  Height = 166
  Placement = pos=(0,168,113) rot=(1,0,0;1.5708rad)
  Radius = 28
FEATURE [Part::Mirroring] Part__Mirroring049  label="Cylinder278 (Mirror #26)010"
  Base = (0,0,0)
  Normal = (1,0,0)
  Placement = pos=(90,0,0) rot=(0,0,1;0rad)
  Source = -> Cylinder295
FEATURE [Part::Fillet] Fillet335
  Base = -> Part__Mirroring048
  Edges = 2 edges r=10: [Edge1,Edge3]
  Placement = pos=(-10,0,0) rot=(0,0,1;0rad)
FEATURE [Part::Cylinder] Cylinder296
  Angle = 26
  AttacherType = Attacher::AttachEngine3D
  Height = 164
  Placement = pos=(0,167,113) rot=(1,0,0;1.5708rad)
  Radius = 40
FEATURE [Part::Mirroring] Part__Mirroring050  label="Cylinder278 (Mirror #26)011"
  Base = (0,0,0)
  Normal = (1,0,0)
  Placement = pos=(100,0,0) rot=(0,0,1;0rad)
  Source = -> Cylinder296
FEATURE [Part::Fillet] Fillet336
  Base = -> Part__Mirroring050
  Edges = 2 edges r=9: [Edge1,Edge3]
  Placement = pos=(-9,0,0) rot=(0,0,1;0rad)
FEATURE [Part::Cylinder] Cylinder297
  Angle = 15
  AttacherType = Attacher::AttachEngine3D
  Height = 66
  Placement = pos=(0,118,113) rot=(1,0,0;1.5708rad)
  Radius = 40
FEATURE [Part::Mirroring] Part__Mirroring051  label="Cylinder278 (Mirror #26)012"
  Base = (0,0,0)
  Normal = (1,0,0)
  Placement = pos=(17,0,1) rot=(0,1,0;0.331613rad)
  Source = -> Cylinder297
FEATURE [Part::Cylinder] Cylinder298
  Angle = 15
  AttacherType = Attacher::AttachEngine3D
  Height = 66
  Placement = pos=(0,118,113) rot=(1,0,0;1.5708rad)
  Radius = 38.2
FEATURE [Part::Mirroring] Part__Mirroring052  label="Cylinder278 (Mirror #26)013"
  Base = (0,0,0)
  Normal = (1,0,0)
  Placement = pos=(17,0,1) rot=(0,1,0;0.331613rad)
  Source = -> Cylinder298
FEATURE [Part::Cylinder] Cylinder299
  Angle = 360
  AttacherType = Attacher::AttachEngine3D
  Height = 4.5
  Placement = pos=(26,167,120) rot=(1,0,0;1.5708rad)
  Radius = 2.5
FEATURE [Part::Cut] Cut457  label="cab-upper-part-004"
  Refine = true
FEATURE [Part::MultiFuse] Fusion250  label="cab-top-part-004"
  Refine = true
FEATURE [Part::MultiFuse] Fusion251
  Refine = true
  Shapes = -> [Cut457,Fusion250]
FEATURE [Part::Cut] Cut458  label="Cut756"
  Base = -> Cylinder299
  Refine = true
  Tool = -> Fusion251
FEATURE [Part::Cut] Cut460  label="cab-upper-part-005"
  Refine = true
FEATURE [Part::Cylinder] Cylinder300
  Angle = 360
  AttacherType = Attacher::AttachEngine3D
  Height = 4.5
  Placement = pos=(26,167,120) rot=(1,0,0;1.5708rad)
  Radius = 2.5
FEATURE [Part::MultiFuse] Fusion252  label="cab-top-part-005"
  Refine = true
FEATURE [Part::MultiFuse] Fusion253
  Refine = true
  Shapes = -> [Cut460,Fusion252]
FEATURE [Part::Cut] Cut459  label="Cut757"
  Base = -> Cylinder300
  Refine = true
  Tool = -> Fusion253
FEATURE [Part::Mirroring] Part__Mirroring053  label="Cut612 (Mirror #31)001"
  Base = (0,0,0)
  Normal = (0,1,0)
  Placement = pos=(0,170,0) rot=(0,0,1;0rad)
  Source = -> Cut459
FEATURE [Part::Cut] Cut461  label="Cut758"
  Base = -> Part__Mirroring051
  Placement = pos=(0,0,0.1) rot=(0,0,1;0rad)
  Refine = true
  Tool = -> Part__Mirroring052
FEATURE [Part::Fillet] Fillet337
  Base = -> Cut461
  Edges = 2 edges r=2: [Edge5,Edge10]
FEATURE [Part::Fillet] Fillet338
  Base = -> Fillet337
  Edges = 5 edges r=1.25: [Edge1,Edge2,Edge4,Edge5,Edge6]
  Placement = pos=(6,0,-0.4) rot=(0,-1,0;0.05236rad)
FEATURE [Part::Cylinder] Cylinder301
  Angle = 360
  AttacherType = Attacher::AttachEngine3D
  Height = 170
  Placement = pos=(26,170,120) rot=(1,0,0;1.5708rad)
  Radius = 1
FEATURE [Part::Cut] Cut462  label="Cut759"
  Base = -> Fillet335
  Refine = true
  Tool = -> Fillet336
FEATURE [Part::Cut] Cut463  label="Cut760"
  Base = -> Cut462
  Placement = pos=(-46.5,0,6) rot=(0,1,0;0.10472rad)
  Refine = true
  Tool = -> Part__Mirroring049
FEATURE [Part::MultiFuse] Fusion254
  Refine = true
  Shapes = -> [Fillet338,Cut463]
FEATURE [Part::MultiFuse] Fusion255
  Refine = true
  Shapes = -> [Cut458,Part__Mirroring053,Fusion254]
FEATURE [Part::Cut] Cut464  label="cab-sunvisor-01"
  Base = -> Fusion255
  Refine = true
  Tool = -> Cylinder301
FEATURE [Part::Box] Box458  label="Cube683"
  AttacherType = Attacher::AttachEngine3D
  Height = 9
  Length = 1
  Placement = pos=(-1,99,12) rot=(0,0,1;0rad)
  Width = 3
FEATURE [Part::Fillet] Fillet339
  Base = -> Box458
  Edges = 4 edges r=0.5: [Edge9,Edge10,Edge11,Edge12]
FEATURE [Part::Box] Box459  label="Cube684"
  AttacherType = Attacher::AttachEngine3D
  Height = 10
  Length = 0.8
  Placement = pos=(-0.9,98.5,11.5) rot=(0,0,1;0rad)
  Width = 4
FEATURE [Part::Fillet] Fillet340
  Base = -> Box459
  Edges = 4 edges r=1: [Edge9,Edge10,Edge11,Edge12]
  Placement = pos=(0.1,0,0) rot=(0,0,1;0rad)
FEATURE [Part::Box] Box460  label="Cube685"
  AttacherType = Attacher::AttachEngine3D
  Height = 2
  Length = 1
  Placement = pos=(-1,81.5,12) rot=(0,0,1;0rad)
  Width = 7
FEATURE [Part::Box] Box461  label="Cube686"
  AttacherType = Attacher::AttachEngine3D
  Height = 3.5
  Length = 0.8
  Placement = pos=(-0.9,81,11.5) rot=(0,0,1;0rad)
  Width = 8
FEATURE [Part::Box] Box462  label="Cube687"
  AttacherType = Attacher::AttachEngine3D
  Height = 2
  Length = 1
  Placement = pos=(-1,81.5,19) rot=(0,0,1;0rad)
  Width = 7
FEATURE [Part::Box] Box463  label="Cube688"
  AttacherType = Attacher::AttachEngine3D
  Height = 3.5
  Length = 0.8
  Placement = pos=(-0.9,81,18) rot=(0,0,1;0rad)
  Width = 8
FEATURE [Part::Box] Box464  label="Cube689"
  AttacherType = Attacher::AttachEngine3D
  Height = 9
  Length = 1
  Placement = pos=(-1,85.5,12) rot=(0,0,1;0rad)
  Width = 3
FEATURE [Part::Box] Box465  label="Cube690"
  AttacherType = Attacher::AttachEngine3D
  Height = 10
  Length = 0.8
  Placement = pos=(-0.9,85,11.5) rot=(0,0,1;0rad)
  Width = 4
FEATURE [Part::Box] Box466  label="Cube691"
  AttacherType = Attacher::AttachEngine3D
  Height = 2
  Length = 1
  Placement = pos=(-1,82.5,15.5) rot=(0,0,1;0rad)
  Width = 5
FEATURE [Part::Box] Box467  label="Cube692"
  AttacherType = Attacher::AttachEngine3D
  Height = 3
  Length = 0.8
  Placement = pos=(-0.9,82.5,15) rot=(0,0,1;0rad)
  Width = 6
FEATURE [Part::MultiFuse] Fusion257
  Refine = true
  Shapes = -> [Box460,Box466,Box462,Box464]
FEATURE [Part::Box] Box468  label="Cube693"
  AttacherType = Attacher::AttachEngine3D
  Height = 2
  Length = 1
  Placement = pos=(-1,74.5,12) rot=(0,0,1;0rad)
  Width = 7
FEATURE [Part::Box] Box470  label="Cube695"
  AttacherType = Attacher::AttachEngine3D
  Height = 2
  Length = 1
  Placement = pos=(-1,74.5,19) rot=(0,0,1;0rad)
  Width = 7
FEATURE [Part::Box] Box471  label="Cube696"
  AttacherType = Attacher::AttachEngine3D
  Height = 9
  Length = 1
  Placement = pos=(-1,78.5,12) rot=(0,0,1;0rad)
  Width = 3
FEATURE [Part::Box] Box472  label="Cube697"
  AttacherType = Attacher::AttachEngine3D
  Height = 3.5
  Length = 0.8
  Placement = pos=(-0.9,74,11.5) rot=(0,0,1;0rad)
  Width = 8
FEATURE [Part::Box] Box473  label="Cube698"
  AttacherType = Attacher::AttachEngine3D
  Height = 3.5
  Length = 0.8
  Placement = pos=(-0.9,74,18) rot=(0,0,1;0rad)
  Width = 8
FEATURE [Part::Box] Box474  label="Cube699"
  AttacherType = Attacher::AttachEngine3D
  Height = 10
  Length = 0.8
  Placement = pos=(-0.9,78,11.5) rot=(0,0,1;0rad)
  Width = 4
FEATURE [Part::MultiFuse] Fusion258
  Refine = true
  Shapes = -> [Box468,Box470,Box471]
FEATURE [Part::MultiFuse] Fusion259
  Placement = pos=(0.1,0,0) rot=(0,0,1;0rad)
  Refine = true
  Shapes = -> [Box472,Box473,Box474]
FEATURE [Part::MultiFuse] Fusion261  label="I"
  Placement = pos=(0,-1,0) rot=(0,0,1;0rad)
  Refine = true
  Shapes = -> [Fillet339,Fillet340]
FEATURE [Part::Box] Box475  label="Cube700"
  AttacherType = Attacher::AttachEngine3D
  Height = 2
  Length = 1
  Placement = pos=(-1,67.5,12) rot=(0,0,1;0rad)
  Width = 6
FEATURE [Part::Box] Box476  label="Cube701"
  AttacherType = Attacher::AttachEngine3D
  Height = 2
  Length = 1
  Placement = pos=(-1,67.5,19) rot=(0,0,1;0rad)
  Width = 6
FEATURE [Part::Box] Box477  label="Cube702"
  AttacherType = Attacher::AttachEngine3D
  Height = 9
  Length = 1
  Placement = pos=(-1,71.5,12) rot=(0,0,1;0rad)
  Width = 3
FEATURE [Part::Box] Box478  label="Cube703"
  AttacherType = Attacher::AttachEngine3D
  Height = 3
  Length = 0.8
  Placement = pos=(-0.9,67,11) rot=(0,0,1;0rad)
  Width = 7
FEATURE [Part::Box] Box479  label="Cube704"
  AttacherType = Attacher::AttachEngine3D
  Height = 3
  Length = 0.8
  Placement = pos=(-0.9,67,18) rot=(0,0,1;0rad)
  Width = 7
FEATURE [Part::Box] Box480  label="Cube705"
  AttacherType = Attacher::AttachEngine3D
  Height = 10
  Length = 0.8
  Placement = pos=(-0.9,71,11) rot=(0,0,1;0rad)
  Width = 4
FEATURE [Part::Box] Box481  label="Cube706"
  AttacherType = Attacher::AttachEngine3D
  Height = 9
  Length = 1
  Placement = pos=(-1,65,12) rot=(0,0,1;0rad)
  Width = 3
FEATURE [Part::Box] Box482  label="Cube707"
  AttacherType = Attacher::AttachEngine3D
  Height = 10
  Length = 0.8
  Placement = pos=(-0.9,64.5,11) rot=(0,0,1;0rad)
  Width = 4
FEATURE [Part::MultiFuse] Fusion263
  Refine = true
  Shapes = -> [Box475,Box476,Box477,Box481]
FEATURE [Part::MultiFuse] Fusion264
  Placement = pos=(0,0.5,0) rot=(0,0,1;0rad)
  Refine = true
  Shapes = -> [Box478,Box479,Box480,Box482]
FEATURE [Part::Box] Box483  label="Cube708"
  AttacherType = Attacher::AttachEngine3D
  Height = 9
  Length = 1
  Placement = pos=(-1,93,12) rot=(0,0,1;0rad)
  Width = 5
FEATURE [Part::Chamfer] Chamfer056
  Base = -> Box483
  Edges = 1 edges: [Edge10 r1=8.99 r2=2]
FEATURE [Part::Chamfer] Chamfer001
  Base = -> Chamfer056
  Edges = 1 edges: [Edge11 r1=2 r2=8.99]
FEATURE [Part::Box] Box485  label="Cube710"
  AttacherType = Attacher::AttachEngine3D
  Height = 9
  Length = 1
  Placement = pos=(-1,93,12) rot=(0,0,1;0rad)
  Width = 4
FEATURE [Part::Chamfer] Chamfer002
  Base = -> Box485
  Edges = 1 edges: [Edge10 r1=8.99 r2=2]
FEATURE [Part::Chamfer] Chamfer003
  Base = -> Chamfer002
  Edges = 1 edges: [Edge11 r1=2 r2=8.99]
FEATURE [Part::Mirroring] Part__Mirroring054  label="Chamfer003 (Mirror #1)"
  Base = (0,0,0)
  Normal = (0,1,0)
  Placement = pos=(0,187,0) rot=(0,0,1;0rad)
  Source = -> Chamfer003
FEATURE [Part::Box] Box486  label="Cube711"
  AttacherType = Attacher::AttachEngine3D
  Height = 10
  Length = 0.8
  Placement = pos=(-1,93,12) rot=(0,0,1;0rad)
  Width = 6
FEATURE [Part::MultiFuse] Fusion266
  Refine = true
  Shapes = -> [Chamfer001,Part__Mirroring054]
FEATURE [Part::Box] Box488  label="Cube713"
  AttacherType = Attacher::AttachEngine3D
  Height = 0.01
  Length = 1
  Placement = pos=(-1,89,20.99) rot=(0,0,1;0rad)
  Width = 10
FEATURE [Part::Cut] Cut465  label="Cut761"
  Base = -> Fusion266
  Refine = true
  Tool = -> Box488
FEATURE [Part::Fillet] Fillet356
  Base = -> Cut465
  Edges = 4 edges r=0.5: [Edge8,Edge11,Edge17,Edge19]
FEATURE [Part::Fillet] Fillet357
  Base = -> Fillet356
  Edges = 2 edges r=1.25: [Edge27,Edge32]
FEATURE [Part::Box] Box489  label="Cube714"
  AttacherType = Attacher::AttachEngine3D
  Height = 0.01
  Length = 1
  Placement = pos=(-1,89,21.49) rot=(0,0,1;0rad)
  Width = 10
FEATURE [Part::Box] Box490  label="Cube715"
  AttacherType = Attacher::AttachEngine3D
  Height = 8
  Length = 0.8
  Placement = pos=(-0.8,68,12.5) rot=(0,0,1;0rad)
  Width = 30
FEATURE [Part::MultiFuse] Fusion267
  Refine = true
  Shapes = -> [Box461,Box465,Box467,Box463]
FEATURE [Part::Fillet] Fillet365
  Base = -> Fusion267
  Edges = 2 edges r=1: [Edge3,Edge14]
FEATURE [Part::Fillet] Fillet366
  Base = -> Fillet365
  Edges = 2 edges r=2.5: [Edge25,Edge27]
  Placement = pos=(0.1,0,0) rot=(0,0,1;0rad)
FEATURE [Part::Chamfer] Chamfer008
  Base = -> Box486
  Edges = 1 edges: [Edge10 r1=9.99 r2=2]
FEATURE [Part::Chamfer] Chamfer009
  Base = -> Chamfer008
  Edges = 1 edges: [Edge11 r1=2 r2=9.99]
  Placement = pos=(0,-0.3,-0.5) rot=(0,0,1;0rad)
FEATURE [Part::Box] Box491  label="Cube716"
  AttacherType = Attacher::AttachEngine3D
  Height = 10
  Length = 0.8
  Placement = pos=(-1,93,12) rot=(0,0,1;0rad)
  Width = 5
FEATURE [Part::Chamfer] Chamfer010
  Base = -> Box491
  Edges = 1 edges: [Edge10 r1=9.99 r2=2]
FEATURE [Part::Chamfer] Chamfer057
  Base = -> Chamfer010
  Edges = 1 edges: [Edge11 r1=2 r2=9.99]
FEATURE [Part::Mirroring] Part__Mirroring055  label="Chamfer011 (Mirror #2)"
  Base = (0,0,0)
  Normal = (0,1,0)
  Placement = pos=(0,187.3,-0.5) rot=(0,0,1;0rad)
  Source = -> Chamfer057
FEATURE [Part::MultiFuse] Fusion272
  Refine = true
  Shapes = -> [Part__Mirroring055,Chamfer009]
FEATURE [Part::Cut] Cut466  label="Cut762"
  Base = -> Fusion272
  Placement = pos=(0.1,0,0) rot=(0,0,1;0rad)
  Refine = true
  Tool = -> Box489
FEATURE [Part::Fillet] Fillet367
  Base = -> Cut466
  Edges = 4 edges r=1: [Edge8,Edge11,Edge17,Edge19]
FEATURE [Part::Fillet] Fillet368
  Base = -> Fillet367
  Edges = 2 edges r=2: [Edge27,Edge32]
  Placement = pos=(0.1,0,0) rot=(0,0,1;0rad)
FEATURE [Part::MultiFuse] Fusion273  label="V"
  Placement = pos=(0,-0.5,0) rot=(0,0,1;0rad)
  Refine = true
  Shapes = -> [Fillet357,Fillet368]
FEATURE [Part::Fillet] Fillet369
  Base = -> Fusion259
  Edges = 2 edges r=4: [Edge20,Edge24]
FEATURE [Part::Fillet] Fillet370
  Base = -> Fillet369
  Edges = 4 edges r=1: [Edge13,Edge16,Edge26,Edge29]
FEATURE [Part::Fillet] Fillet371
  Base = -> Fillet370
  Edges = 2 edges r=0.3: [Edge31,Edge34]
FEATURE [Part::Box] Box495  label="Cube720"
  AttacherType = Attacher::AttachEngine3D
  Height = 1.4
  Length = 2
  Placement = pos=(0,67,14.5) rot=(0,0,1;0rad)
  Width = 33
FEATURE [Part::Fillet] Fillet403
  Base = -> Fusion263
  Edges = 4 edges r=3.5: [Edge1,Edge3,Edge7,Edge9]
FEATURE [Part::Fillet] Fillet404
  Base = -> Fillet403
  Edges = 4 edges r=1: [Edge33,Edge34,Edge35,Edge36]
FEATURE [Part::Fillet] Fillet405
  Base = -> Fusion264
  Edges = 4 edges r=4: [Edge1,Edge3,Edge7,Edge9]
  Placement = pos=(0.1,-0.5,0.5) rot=(0,0,1;0rad)
FEATURE [Part::Fillet] Fillet406
  Base = -> Fusion258
  Edges = 4 edges r=0.5: [Edge1,Edge3,Edge13,Edge14]
FEATURE [Part::Fillet] Fillet407
  Base = -> Fillet406
  Edges = 2 edges r=3.5: [Edge30,Edge32]
FEATURE [Part::Fillet] Fillet408
  Base = -> Fillet407
  Edges = 2 edges r=1.5: [Edge33,Edge37]
FEATURE [Part::MultiFuse] Fusion295  label="C"
  Refine = true
  Shapes = -> [Fillet371,Fillet408]
FEATURE [Part::MultiFuse] Fusion296  label="O"
  Placement = pos=(0,-0.3,0) rot=(0,0,1;0rad)
  Refine = true
  Shapes = -> [Fillet405,Fillet404]
FEATURE [Part::Fillet] Fillet409
  Base = -> Fusion257
  Edges = 6 edges r=0.5: [Edge1,Edge3,Edge19,Edge22,Edge23,Edge27]
FEATURE [Part::Fillet] Fillet410
  Base = -> Fillet409
  Edges = 2 edges r=2: [Edge50,Edge52]
FEATURE [Part::Fillet] Fillet411
  Base = -> Fillet410
  Edges = 2 edges r=0.75: [Edge39,Edge53]
FEATURE [Part::MultiFuse] Fusion297  label="E"
  Placement = pos=(0,0.3,0) rot=(0,0,1;0rad)
  Refine = true
  Shapes = -> [Fillet366,Fillet411]
FEATURE [Part::MultiFuse] Fusion298
  Placement = pos=(0,0.5,-1) rot=(0,0,1;0rad)
  Refine = true
  Shapes = -> [Fusion273,Fusion261,Box490,Fusion297,Fusion295,Fusion296]
FEATURE [Part::Box] Box531  label="Cube756"
  AttacherType = Attacher::AttachEngine3D
  Height = 10
  Length = 0.2
  Placement = pos=(-0.2,64,10.5) rot=(0,0,1;0rad)
  Width = 39
FEATURE [Part::Cut] Cut005
  Base = -> Fusion298
  Placement = pos=(0.2,0,0) rot=(0,0,1;0rad)
  Refine = true
  Tool = -> Box531
FEATURE [Part::MultiFuse] Fusion299  label="iveco-logo_01"
  Refine = true
  Shapes = -> [Box495,Cut005]
FEATURE [Part::Box] Box533  label="Cube758"
  AttacherType = Attacher::AttachEngine3D
  Height = 2.5
  Length = 0.3
  Placement = pos=(0.3,32.5,32.5) rot=(0,0,1;0rad)
  Width = 17
FEATURE [Part::Part2DObjectPython] ShapeString006  # Draft 2D object (typed FeaturePython)
  FontFile = <path>
  MapMode = 5
  Placement = pos=(0,52,32) rot=(0.57735,-0.57735,-0.57735;2.0944rad)
  Size = 1.35
  String = T
  Tracking = 0
FEATURE [Part::Part2DObjectPython] ShapeString004  # Draft 2D object (typed FeaturePython)
  FontFile = <path>
  MapMode = 5
  Placement = pos=(0,48,32) rot=(0.57735,-0.57735,-0.57735;2.0944rad)
  Size = 1.3
  String = u
  Tracking = 0
FEATURE [Part::Part2DObjectPython] ShapeString007  # Draft 2D object (typed FeaturePython)
  FontFile = <path>
  MapMode = 5
  Placement = pos=(0,43.75,32) rot=(0.57735,-0.57735,-0.57735;2.0944rad)
  Size = 1.3
  String = r
  Tracking = 0
FEATURE [Part::Part2DObjectPython] ShapeString008  # Draft 2D object (typed FeaturePython)
  FontFile = <path>
  MapMode = 5
  Placement = pos=(0,40.5,32) rot=(0.57735,-0.57735,-0.57735;2.0944rad)
  Size = 1.3
  String = b
  Tracking = 0
FEATURE [Part::Part2DObjectPython] ShapeString009  # Draft 2D object (typed FeaturePython)
  FontFile = <path>
  MapMode = 5
  Placement = pos=(0,36,32) rot=(0.57735,-0.57735,-0.57735;2.0944rad)
  Size = 1.3
  String = o
  Tracking = 0
FEATURE [Part::Extrusion] Extrude006
  Base = -> ShapeString009
  Dir = (0.6,0,0)
  DirMode = 0
  FaceMakerClass = Part::FaceMakerExtrusion
  LengthFwd = 0
  LengthRev = 0
  Solid = false
  Symmetric = false
FEATURE [Part::Extrusion] Extrude004
  Base = -> ShapeString008
  Dir = (0.6,0,0)
  DirMode = 0
  FaceMakerClass = Part::FaceMakerExtrusion
  LengthFwd = 0
  LengthRev = 0
  Solid = false
  Symmetric = false
FEATURE [Part::Extrusion] Extrude007
  Base = -> ShapeString007
  Dir = (0.6,0,0)
  DirMode = 0
  FaceMakerClass = Part::FaceMakerExtrusion
  LengthFwd = 0
  LengthRev = 0
  Solid = false
  Symmetric = false
FEATURE [Part::Extrusion] Extrude008
  Base = -> ShapeString004
  Dir = (0.6,0,0)
  DirMode = 0
  FaceMakerClass = Part::FaceMakerExtrusion
  LengthFwd = 0
  LengthRev = 0
  Solid = false
  Symmetric = false
FEATURE [Part::Extrusion] Extrude009
  Base = -> ShapeString006
  Dir = (0.6,0,0)
  DirMode = 0
  FaceMakerClass = Part::FaceMakerExtrusion
  LengthFwd = 0
  LengthRev = 0
  Solid = false
  Symmetric = false
FEATURE [Part::Chamfer] Chamfer058
  Base = -> Extrude009
  Edges = 8 edges r=0.2: [Edge3,Edge6,Edge9,Edge12,Edge15,Edge18,Edge21,Edge23]
FEATURE [Part::Chamfer] Chamfer059
  Base = -> Extrude008
  Edges = 6 edges r=0.2: [Edge3,Edge33,Edge36,Edge39,Edge57,Edge59]
FEATURE [Part::Chamfer] Chamfer060
  Base = -> Extrude007
  Edges = 3 edges r=0.2: [Edge15,Edge18,Edge21]
FEATURE [Part::Chamfer] Chamfer061
  Base = -> Chamfer060
  Edges = 1 edges r=0.2: [Edge28]
FEATURE [Part::Chamfer] Chamfer062
  Base = -> Chamfer061
  Edges = 1 edges r=0.2: [Edge12]
FEATURE [Part::Chamfer] Chamfer063
  Base = -> Chamfer062
  Edges = 1 edges r=0.2: [Edge4]
FEATURE [Part::Chamfer] Chamfer064
  Base = -> Extrude004
  Edges = 6 edges r=0.2: [Edge3,Edge6,Edge42,Edge57,Edge60,Edge62]
FEATURE [Part::Chamfer] Chamfer065
  Base = -> Extrude006
  Edges = 1 edges r=0.2: [Edge3]
FEATURE [Part::Box] Box534  label="Cube759"
  AttacherType = Attacher::AttachEngine3D
  Height = 2
  Length = 0.3
  Placement = pos=(0.3,37,33.5) rot=(0,0,1;0rad)
  Width = 13
FEATURE [Part::Box] Box535  label="Cube760"
  AttacherType = Attacher::AttachEngine3D
  Height = 2
  Length = 0.3
  Placement = pos=(0.3,47.3,34.5) rot=(0,0,1;0rad)
  Width = 2
FEATURE [Part::MultiFuse] Fusion301
  Refine = true
  Shapes = -> [Chamfer058,Chamfer065,Chamfer059,Chamfer064,Chamfer063]
FEATURE [Part::MultiFuse] Fusion302
  Refine = true
  Shapes = -> [Box533,Fusion301]
FEATURE [Part::MultiFuse] Fusion303
  Refine = true
  Shapes = -> [Fusion302,Box535]
FEATURE [Part::MultiFuse] Fusion304  label="turbo-logo-01"
  Placement = pos=(-0.6,0,0) rot=(0,0,1;0rad)
  Refine = true
  Shapes = -> [Fusion303,Box534]
FEATURE [App::DocumentObjectGroup] Group  label="deleted"
  Group = -> [Cut398,Cut425,Fusion196,Fusion197,Cut389,Fusion247,Fusion047,Fusion094,Cut409,Cut408]
FEATURE [Part::Box] Box536  label="Cube761"
  AttacherType = Attacher::AttachEngine3D
  Height = 64
  Length = 126
  Width = 170
FEATURE [Part::Fillet] Fillet413
  Base = -> Box536
  Edges = 2 edges r=15: [Edge1,Edge3]
FEATURE [Part::Fillet] Fillet412
  Base = -> Fillet413
  Edges = 2 edges r=10: [Edge17,Edge18]
FEATURE [Part::Box] Box537  label="Cube762"
  AttacherType = Attacher::AttachEngine3D
  Height = 64
  Length = 120
  Placement = pos=(4,4,0) rot=(0,0,1;0rad)
  Width = 164
FEATURE [Part::Fillet] Fillet415
  Base = -> Box537
  Edges = 2 edges r=12: [Edge1,Edge3]
FEATURE [Part::Fillet] Fillet414
  Base = -> Fillet415
  Edges = 2 edges r=6: [Edge17,Edge18]
  Placement = pos=(-1,-1,0) rot=(0,0,1;0rad)
FEATURE [Part::Cut] Cut468  label="Cut764"
  Base = -> Fillet412
  Refine = true
  Tool = -> Fillet414
FEATURE [Part::Cylinder] Cylinder302
  Angle = 360
  AttacherType = Attacher::AttachEngine3D
  Height = 174
  Placement = pos=(98,174,-23) rot=(1,0,0;1.5708rad)
  Radius = 52
FEATURE [Part::Cut] Cut467  label="Cut763"
  Base = -> Cut468
  Refine = true
  Tool = -> Cylinder302
FEATURE [Part::Box] Box538  label="Cube763"
  AttacherType = Attacher::AttachEngine3D
  Height = 25
  Length = 131
  Placement = pos=(11,0,6) rot=(0,0,1;0rad)
  Width = 170
FEATURE [Part::Box] Box539  label="Cube764"
  AttacherType = Attacher::AttachEngine3D
  Height = 25
  Length = 148
  Placement = pos=(2,2,6) rot=(0,0,1;0rad)
  Width = 166
FEATURE [Part::Box] Box540  label="Cube765"
  AttacherType = Attacher::AttachEngine3D
  Height = 31
  Length = 62
  Placement = pos=(83,1,2) rot=(0,0,1;0rad)
  Width = 1
FEATURE [Part::Box] Box541  label="Cube766"
  AttacherType = Attacher::AttachEngine3D
  Height = 31
  Length = 63.5
  Placement = pos=(83,-1,2) rot=(0,0,1;0.017453rad)
  Width = 2
FEATURE [Part::Cut] Cut470  label="Cut766"
  Base = -> Box540
  Refine = true
  Tool = -> Box541
FEATURE [Part::Cylinder] Cylinder303
  Angle = 360
  AttacherType = Attacher::AttachEngine3D
  Height = 10
  Placement = pos=(98,10,-23) rot=(1,0,0;1.5708rad)
  Radius = 52
FEATURE [Part::Cut] Cut469  label="Cut765"
  Base = -> Cut470
  Refine = true
  Tool = -> Cylinder303
FEATURE [Part::Cylinder] Cylinder304
  Angle = 360
  AttacherType = Attacher::AttachEngine3D
  Height = 10
  Placement = pos=(98,10,-23) rot=(1,0,0;1.5708rad)
  Radius = 52
FEATURE [Part::Box] Box542  label="Cube767"
  AttacherType = Attacher::AttachEngine3D
  Height = 25
  Length = 63.5
  Placement = pos=(20,1,8) rot=(0,0,-1;0.027925rad)
  Width = 1
FEATURE [Part::Box] Box543  label="Cube768"
  AttacherType = Attacher::AttachEngine3D
  Height = 25
  Length = 62.5
  Placement = pos=(20.5,1,8) rot=(0,0,1;0rad)
  Width = 1
FEATURE [Part::Cut] Cut472  label="Cut768"
  Base = -> Box543
  Refine = true
  Tool = -> Box542
FEATURE [Part::Cut] Cut471  label="Cut767"
  Base = -> Cut472
  Refine = true
  Tool = -> Cylinder304
FEATURE [Part::MultiFuse] Fusion305
  Refine = true
  Shapes = -> [Cut469,Cut471]
FEATURE [Part::Box] Box544  label="Cube769"
  AttacherType = Attacher::AttachEngine3D
  Height = 25
  Length = 63.5
  Placement = pos=(20,1,8) rot=(0,0,-1;0.027925rad)
  Width = 1
FEATURE [Part::Box] Box545  label="Cube770"
  AttacherType = Attacher::AttachEngine3D
  Height = 25
  Length = 62.5
  Placement = pos=(20.5,1,8) rot=(0,0,1;0rad)
  Width = 1
FEATURE [Part::Cut] Cut475  label="Cut771"
  Base = -> Box545
  Refine = true
  Tool = -> Box544
FEATURE [Part::Box] Box546  label="Cube771"
  AttacherType = Attacher::AttachEngine3D
  Height = 31
  Length = 63.5
  Placement = pos=(83,-1,2) rot=(0,0,1;0.017453rad)
  Width = 2
FEATURE [Part::Box] Box547  label="Cube772"
  AttacherType = Attacher::AttachEngine3D
  Height = 31
  Length = 62
  Placement = pos=(83,1,2) rot=(0,0,1;0rad)
  Width = 1
FEATURE [Part::Cut] Cut473  label="Cut769"
  Base = -> Box547
  Refine = true
  Tool = -> Box546
FEATURE [Part::Cylinder] Cylinder305
  Angle = 360
  AttacherType = Attacher::AttachEngine3D
  Height = 10
  Placement = pos=(98,10,-23) rot=(1,0,0;1.5708rad)
  Radius = 52
FEATURE [Part::Cut] Cut476  label="Cut772"
  Base = -> Cut473
  Refine = true
  Tool = -> Cylinder305
FEATURE [Part::Cylinder] Cylinder306
  Angle = 360
  AttacherType = Attacher::AttachEngine3D
  Height = 10
  Placement = pos=(98,10,-23) rot=(1,0,0;1.5708rad)
  Radius = 52
FEATURE [Part::Cut] Cut474  label="Cut770"
  Base = -> Cut475
  Refine = true
  Tool = -> Cylinder306
FEATURE [Part::MultiFuse] Fusion306
  Refine = true
  Shapes = -> [Cut476,Cut474]
FEATURE [Part::Mirroring] Part__Mirroring056  label="Fusion008 (Mirror #2)001"
  Base = (0,0,0)
  Normal = (0,1,0)
  Placement = pos=(0,170,0) rot=(0,0,1;0rad)
  Source = -> Fusion306
FEATURE [Part::MultiFuse] Fusion307
  Refine = true
  Shapes = -> [Part__Mirroring056,Fusion305]
FEATURE [Part::Cut] Cut477  label="Cut773"
  Base = -> Box538
  Placement = pos=(0,0,2) rot=(0,0,1;0rad)
  Refine = true
  Tool = -> Box539
FEATURE [Part::Cut] Cut478  label="Cut774"
  Base = -> Cut477
  Placement = pos=(0,0,-3) rot=(0,0,1;0rad)
  Refine = true
  Tool = -> Fusion307
FEATURE [Part::Cut] Cut479  label="Cut775"
  Base = -> Cut467
  Refine = true
  Tool = -> Cut478
FEATURE [Part::Box] Box548  label="Cube773"
  AttacherType = Attacher::AttachEngine3D
  Height = 64
  Length = 21
  Width = 164
FEATURE [Part::Fillet] Fillet416
  Base = -> Box548
  Edges = 2 edges r=12: [Edge1,Edge3]
  Placement = pos=(3,3,0) rot=(0,0,1;0rad)
FEATURE [Part::Box] Box549  label="Cube774"
  AttacherType = Attacher::AttachEngine3D
  Height = 59
  Length = 16
  Placement = pos=(15,0,0) rot=(0,0,1;0rad)
  Width = 170
FEATURE [Part::Box] Box550  label="Cube775"
  AttacherType = Attacher::AttachEngine3D
  Height = 59
  Length = 21
  Placement = pos=(-13,3,0) rot=(0,0,1;0rad)
  Width = 164
FEATURE [Part::Box] Box551  label="Cube776"
  AttacherType = Attacher::AttachEngine3D
  Height = 59
  Length = 21
  Placement = pos=(-13,0,0) rot=(0,0,1;0rad)
  Width = 170
FEATURE [Part::Fillet] Fillet417
  Base = -> Box551
  Edges = 2 edges r=15: [Edge1,Edge3]
FEATURE [Part::Fillet] Fillet418
  Base = -> Box550
  Edges = 2 edges r=12: [Edge1,Edge3]
  Placement = pos=(3,0,0) rot=(0,0,1;0rad)
FEATURE [Part::Cut] Cut480  label="Cut776"
  Base = -> Fillet417
  Placement = pos=(13,0,0) rot=(0,0,1;0rad)
  Refine = true
  Tool = -> Fillet418
FEATURE [Part::Cut] Cut481  label="Cut777"
  Base = -> Cut480
  Refine = true
  Tool = -> Box549
FEATURE [Part::Feature] Face030
  Placement = pos=(0,0,-10) rot=(0,0,1;0rad)
  shape: bbox 128.7 x 180.4 x 2e-07 mm, 1 faces, 0 solids (baked)
FEATURE [Part::Feature] Face031
  Placement = pos=(0,0,50) rot=(0,0,1;0rad)
  shape: bbox 110 x 176 x 2e-07 mm, 1 faces, 0 solids (baked)
FEATURE [Part::Loft] Loft015
  Closed = false
  MaxDegree = 5
  Ruled = false
  Sections = -> [Face031,Face030]
  Solid = true
FEATURE [Part::Feature] Face032
  Placement = pos=(0,0,50) rot=(0,0,1;0rad)
  shape: bbox 103.4 x 169.4 x 2e-07 mm, 1 faces, 0 solids (baked)
FEATURE [Part::Feature] Face033
  Placement = pos=(0,0,-10) rot=(0,0,1;0rad)
  shape: bbox 122.1 x 173.8 x 2e-07 mm, 1 faces, 0 solids (baked)
FEATURE [Part::Loft] Loft016
  Closed = false
  MaxDegree = 5
  Ruled = false
  Sections = -> [Face032,Face033]
  Solid = true
FEATURE [Part::Cut] Cut482  label="Cut778"
  Base = -> Loft015
  Refine = true
  Tool = -> Loft016
FEATURE [Part::Box] Box552  label="Cube777"
  AttacherType = Attacher::AttachEngine3D
  Height = 55
  Length = 10
  Placement = pos=(0,7,68) rot=(0,1,0;0.226893rad)
  Width = 156
FEATURE [Part::Chamfer] Chamfer066
  Base = -> Cut479
  Edges = 4 edges r=2.5: [Edge1,Edge4,Edge5,Edge8]
FEATURE [Part::Chamfer] Chamfer067
  Base = -> Chamfer066
  Edges = 4 edges r=0.9: [Edge52,Edge80,Edge102,Edge110]
FEATURE [Part::Fillet] Fillet419
  Base = -> Box552
  Edges = 4 edges r=5: [Edge9,Edge10,Edge11,Edge12]
  Placement = pos=(6,0,-1) rot=(0,0,1;0rad)
FEATURE [Part::Box] Box553  label="Cube778"
  AttacherType = Attacher::AttachEngine3D
  Height = 42
  Length = 26
  Placement = pos=(89,4.3,70) rot=(-1,0,0;0.038397rad)
  Width = 5
FEATURE [Part::Fillet] Fillet420
  Base = -> Box553
  Edges = 4 edges r=3: [Edge2,Edge4,Edge6,Edge8]
  Placement = pos=(-3,-2,0) rot=(0,0,1;0rad)
FEATURE [Part::Box] Box554  label="Cube779"
  AttacherType = Attacher::AttachEngine3D
  Height = 42
  Length = 58
  Placement = pos=(19.5,2,70) rot=(-1,0,0;0.038397rad)
  Width = 5
FEATURE [Part::Box] Box555  label="Cube780"
  AttacherType = Attacher::AttachEngine3D
  Height = 48
  Length = 11
  Placement = pos=(8.5,1,70) rot=(-0.179679,0.983544,0.018885;0.212918rad)
  Width = 7
FEATURE [Part::Cut] Cut483  label="Cut779"
  Base = -> Box554
  Refine = true
  Tool = -> Box555
FEATURE [Part::Fillet] Fillet421
  Base = -> Cut483
  Edges = 4 edges r=3: [Edge2,Edge4,Edge8,Edge12]
FEATURE [Part::MultiFuse] Fusion308  label="left-windows-holes001"
  Refine = true
  Shapes = -> [Fillet420,Fillet421]
FEATURE [Part::Box] Box556  label="Cube781"
  AttacherType = Attacher::AttachEngine3D
  Height = 42
  Length = 26
  Placement = pos=(89,4.3,70) rot=(-1,0,0;0.038397rad)
  Width = 5
FEATURE [Part::Fillet] Fillet422
  Base = -> Box556
  Edges = 4 edges r=3: [Edge2,Edge4,Edge6,Edge8]
  Placement = pos=(-3,-2,0) rot=(0,0,1;0rad)
FEATURE [Part::Box] Box557  label="Cube782"
  AttacherType = Attacher::AttachEngine3D
  Height = 42
  Length = 58
  Placement = pos=(19.5,2,70) rot=(-1,0,0;0.038397rad)
  Width = 5
FEATURE [Part::Box] Box558  label="Cube783"
  AttacherType = Attacher::AttachEngine3D
  Height = 48
  Length = 11
  Placement = pos=(8.5,1,70) rot=(-0.179679,0.983544,0.018885;0.212918rad)
  Width = 7
FEATURE [Part::Cut] Cut484  label="Cut780"
  Base = -> Box557
  Refine = true
  Tool = -> Box558
FEATURE [Part::Fillet] Fillet423
  Base = -> Cut484
  Edges = 4 edges r=3: [Edge2,Edge4,Edge8,Edge12]
FEATURE [Part::MultiFuse] Fusion309
  Refine = true
  Shapes = -> [Fillet422,Fillet423]
FEATURE [Part::Mirroring] Part__Mirroring057  label="right-windows-holes001"
  Base = (0,0,0)
  Normal = (0,1,0)
  Placement = pos=(0,170,0) rot=(0,0,1;0rad)
  Source = -> Fusion309
FEATURE [Part::Box] Box559  label="Cube784"
  AttacherType = Attacher::AttachEngine3D
  Height = 25
  Length = 10
  Placement = pos=(150,40,0) rot=(0,0,1;0rad)
  Width = 100
FEATURE [Part::Box] Box560  label="Cube785"
  AttacherType = Attacher::AttachEngine3D
  Height = 40
  Length = 10
  Placement = pos=(150,19,0) rot=(-1,0,0;0.383972rad)
  Width = 20
FEATURE [Part::Box] Box561  label="Cube786"
  AttacherType = Attacher::AttachEngine3D
  Height = 40
  Length = 10
  Placement = pos=(150,19,0) rot=(-1,0,0;0.383972rad)
  Width = 20
FEATURE [Part::Mirroring] Part__Mirroring058  label="Cube088 (Mirror #13)001"
  Base = (0,0,0)
  Normal = (0,1,0)
  Placement = pos=(0,180,0) rot=(0,0,1;0rad)
  Source = -> Box561
FEATURE [Part::MultiFuse] Fusion310
  Refine = true
  Shapes = -> [Box560,Part__Mirroring058]
FEATURE [Part::Cut] Cut485  label="Cut781"
  Base = -> Box559
  Placement = pos=(-30,-5,20) rot=(0,0,1;0rad)
  Refine = true
  Tool = -> Fusion310
FEATURE [Part::Fillet] Fillet424
  Base = -> Cut485
  Edges = 2 edges r=6: [Edge5,Edge6]
FEATURE [Part::Box] Box562  label="Cube787"
  AttacherType = Attacher::AttachEngine3D
  Height = 27
  Length = 7
  Placement = pos=(116,55,85) rot=(0,-1,0;0.034907rad)
  Width = 60
FEATURE [Part::Box] Box563  label="Cube788"
  AttacherType = Attacher::AttachEngine3D
  Height = 38
  Length = 5
  Placement = pos=(175,0,0) rot=(0,0,1;0rad)
  Width = 25
FEATURE [Part::Box] Box564  label="Cube789"
  AttacherType = Attacher::AttachEngine3D
  Height = 40
  Length = 5
  Placement = pos=(175,-24,-1) rot=(-1,0,0;0.038397rad)
  Width = 24
FEATURE [Part::Cut] Cut486  label="Cut782"
  Base = -> Box563
  Placement = pos=(0,1,1) rot=(0,0,1;0rad)
  Refine = true
  Tool = -> Box564
FEATURE [Part::Cylinder] Cylinder307
  Angle = 360
  AttacherType = Attacher::AttachEngine3D
  Height = 134
  Radius = 3.7
FEATURE [Part::Fillet] Fillet425
  Base = -> Cylinder307
  Edges = 2 edges r=2: [Edge1,Edge3]
  Placement = pos=(128,152,53) rot=(1,0,0;1.5708rad)
FEATURE [Part::Box] Box565  label="Cube790"
  AttacherType = Attacher::AttachEngine3D
  Height = 38
  Length = 5
  Placement = pos=(175,0,0) rot=(0,0,1;0rad)
  Width = 25
FEATURE [Part::Box] Box566  label="Cube791"
  AttacherType = Attacher::AttachEngine3D
  Height = 40
  Length = 5
  Placement = pos=(175,-24,-1) rot=(-1,0,0;0.038397rad)
  Width = 24
FEATURE [Part::Cut] Cut487  label="Cut783"
  Base = -> Box565
  Placement = pos=(-57,17,74) rot=(0,0,1;0rad)
  Refine = true
  Tool = -> Box566
FEATURE [Part::Mirroring] Part__Mirroring059  label="Cut784"
  Base = (0,0,0)
  Normal = (0,1,0)
  Placement = pos=(-57,154,73) rot=(0,0,1;0rad)
  Source = -> Cut486
FEATURE [Part::Fillet] Fillet426
  Base = -> Cut487
  Edges = 4 edges r=3: [Edge1,Edge3,Edge5,Edge10]
  Placement = pos=(3,0,-4) rot=(0,-1,0;0.034907rad)
FEATURE [Part::Fillet] Fillet427
  Base = -> Part__Mirroring059
  Edges = 4 edges r=3: [Edge1,Edge3,Edge5,Edge10]
  Placement = pos=(3,0,-4) rot=(0,-1,0;0.034907rad)
FEATURE [Part::Cylinder] Cylinder308
  Angle = 360
  AttacherType = Attacher::AttachEngine3D
  Height = 60
  Radius = 3.7
FEATURE [Part::Fillet] Fillet428
  Base = -> Cylinder308
  Edges = 2 edges r=2: [Edge1,Edge3]
  Placement = pos=(125,115,75) rot=(1,0,0;1.5708rad)
FEATURE [Part::Box] Box567  label="Cube792"
  AttacherType = Attacher::AttachEngine3D
  Height = 9
  Length = 14
  Width = 2
FEATURE [Part::Fillet] Fillet429
  Base = -> Box567
  Edges = 4 edges r=2: [Edge2,Edge4,Edge6,Edge8]
  Placement = pos=(68.5,0,46.5) rot=(0,0,1;0rad)
FEATURE [Part::Box] Box568  label="Cube793"
  AttacherType = Attacher::AttachEngine3D
  Height = 9
  Length = 14
  Width = 2
FEATURE [Part::Fillet] Fillet430
  Base = -> Box568
  Edges = 4 edges r=2: [Edge2,Edge4,Edge6,Edge8]
  Placement = pos=(68.5,168,46.5) rot=(0,0,1;0rad)
FEATURE [Part::MultiFuse] Fusion311
  Placement = pos=(-4,0,-13) rot=(0,0,1;0rad)
  Refine = true
  Shapes = -> [Fillet430,Fillet429]
FEATURE [Part::MultiFuse] Fusion312
  Refine = true
  Shapes = -> [Fillet427,Box562,Part__Mirroring057,Fusion308,Fillet426]
FEATURE [Part::Box] Box569  label="Cube794"
  AttacherType = Attacher::AttachEngine3D
  Height = 116
  Length = 66.5
  Placement = pos=(14.5,0,-0.5) rot=(0,0,1;0rad)
  Width = 5
FEATURE [Part::Box] Box570  label="Cube795"
  AttacherType = Attacher::AttachEngine3D
  Height = 117
  Length = 67.5
  Placement = pos=(14,0,-1) rot=(0,0,1;0rad)
  Width = 5
FEATURE [Part::Box] Box571  label="Cube796"
  AttacherType = Attacher::AttachEngine3D
  Height = 116
  Length = 67
  Placement = pos=(-53.2,0,65) rot=(0,1,0;0.218166rad)
  Width = 5
FEATURE [Part::Cut] Cut489  label="Cut786"
  Base = -> Box569
  Placement = pos=(0,-2,0) rot=(0,0,1;0rad)
  Refine = true
  Tool = -> Box571
FEATURE [Part::Box] Box572  label="Cube797"
  AttacherType = Attacher::AttachEngine3D
  Height = 116
  Length = 67
  Placement = pos=(-53.7,0,65) rot=(0,1,0;0.218166rad)
  Width = 5
FEATURE [Part::Cut] Cut488  label="Cut785"
  Base = -> Box570
  Placement = pos=(0,-2,0) rot=(0,0,1;0rad)
  Refine = true
  Tool = -> Box572
FEATURE [Part::Cut] Cut490  label="Cut787"
  Base = -> Cut482
  Refine = true
  Tool = -> Fusion312
FEATURE [Part::Cut] Cut491  label="doors-cut-002"
  Base = -> Cut488
  Placement = pos=(0.5,3,0.5) rot=(0,0,1;0rad)
  Refine = true
  Tool = -> Cut489
FEATURE [Part::Cut] Cut492  label="Cut788"
  Base = -> Cut490
  Refine = true
  Tool = -> Fillet419
FEATURE [Part::Box] Box573  label="Cube798"
  AttacherType = Attacher::AttachEngine3D
  Height = 116
  Length = 67
  Placement = pos=(-53.2,0,65) rot=(0,1,0;0.218166rad)
  Width = 10
FEATURE [Part::Box] Box574  label="Cube799"
  AttacherType = Attacher::AttachEngine3D
  Height = 116
  Length = 67
  Placement = pos=(-53.7,0,65) rot=(0,1,0;0.218166rad)
  Width = 10
FEATURE [Part::Box] Box575  label="Cube800"
  AttacherType = Attacher::AttachEngine3D
  Height = 117
  Length = 67.5
  Placement = pos=(14,0,-1) rot=(0,0,1;0rad)
  Width = 10
FEATURE [Part::Cut] Cut494  label="Cut789"
  Base = -> Box575
  Placement = pos=(0,-2,0) rot=(0,0,1;0rad)
  Refine = true
  Tool = -> Box574
FEATURE [Part::Box] Box576  label="Cube801"
  AttacherType = Attacher::AttachEngine3D
  Height = 116
  Length = 66.5
  Placement = pos=(14.5,0,-0.5) rot=(0,0,1;0rad)
  Width = 10
FEATURE [Part::Cut] Cut495  label="Cut790"
  Base = -> Box576
  Placement = pos=(0,-2,0) rot=(0,0,1;0rad)
  Refine = true
  Tool = -> Box573
FEATURE [Part::Cut] Cut493  label="doors-cut-003"
  Base = -> Cut494
  Placement = pos=(1.5,-3,0.5) rot=(0,0,1;0rad)
  Refine = true
  Tool = -> Cut495
FEATURE [Part::Fillet] Fillet431
  Base = -> Cut492
  Edges = 4 edges r=3: [Edge209,Edge210,Edge211,Edge212]
FEATURE [Part::Cut] Cut496  label="Cut791"
  Base = -> Fillet431
  Refine = true
  Tool = -> Fillet428
FEATURE [Part::Box] Box577  label="Cube802"
  AttacherType = Attacher::AttachEngine3D
  Height = 64
  Length = 21
  Width = 164
FEATURE [Part::Fillet] Fillet432
  Base = -> Box577
  Edges = 2 edges r=18: [Edge1,Edge3]
  Placement = pos=(7,3,0) rot=(0,0,1;0rad)
FEATURE [Part::Cut] Cut497  label="Cut792"
  Base = -> Fillet416
  Refine = true
  Tool = -> Fillet432
FEATURE [Part::MultiFuse] Fusion313
  Refine = true
  Shapes = -> [Chamfer067,Cut497]
FEATURE [Part::Cut] Cut498  label="Cut793"
  Base = -> Fusion313
  Refine = true
  Tool = -> Cut481
FEATURE [Part::Cut] Cut499  label="Cut794"
  Base = -> Cut498
  Refine = true
  Tool = -> Fillet425
FEATURE [Part::Cut] Cut500  label="Cut795"
  Base = -> Cut499
  Refine = true
  Tool = -> Fillet424
FEATURE [Part::Cut] Cut501  label="Cut796"
  Base = -> Cut500
  Refine = true
  Tool = -> Fusion311
FEATURE [Part::Fillet] Fillet433
  Base = -> Cut501
  Edges = 2 edges r=3: [Edge74,Edge149]
FEATURE [Part::Box] Box578  label="Cube803"
  AttacherType = Attacher::AttachEngine3D
  Height = 2
  Length = 117
  Placement = pos=(6,3,54) rot=(0,0,1;0rad)
  Width = 164
FEATURE [Part::Fillet] Fillet434
  Base = -> Box578
  Edges = 2 edges r=15: [Edge1,Edge3]
FEATURE [Part::Fillet] Fillet435
  Base = -> Fillet434
  Edges = 2 edges r=6: [Edge17,Edge18]
FEATURE [Part::Box] Box579  label="Cube804"
  AttacherType = Attacher::AttachEngine3D
  Height = 2
  Length = 111
  Placement = pos=(6,3,54) rot=(0,0,1;0rad)
  Width = 158
FEATURE [Part::Fillet] Fillet437
  Base = -> Box579
  Edges = 2 edges r=12: [Edge1,Edge3]
FEATURE [Part::Fillet] Fillet436
  Base = -> Fillet437
  Edges = 2 edges r=3: [Edge17,Edge18]
  Placement = pos=(3,3,0) rot=(0,0,1;0rad)
FEATURE [Part::Cut] Cut502  label="Cut797"
  Base = -> Fillet435
  Placement = pos=(0,0,8) rot=(0,0,1;0rad)
  Refine = true
  Tool = -> Fillet436
FEATURE [Part::Box] Box580  label="Cube805"
  AttacherType = Attacher::AttachEngine3D
  Height = 1
  Length = 96
  Placement = pos=(26,4,116.5) rot=(0,0,1;0rad)
  Width = 162
FEATURE [Part::Box] Box581  label="Cube806"
  AttacherType = Attacher::AttachEngine3D
  Height = 1
  Length = 94
  Placement = pos=(26,6,116.5) rot=(0,0,1;0rad)
  Width = 158
FEATURE [Part::Fillet] Fillet438
  Base = -> Box581
  Edges = 2 edges r=4: [Edge5,Edge7]
FEATURE [Part::Fillet] Fillet439
  Base = -> Box580
  Edges = 2 edges r=6: [Edge5,Edge7]
FEATURE [Part::Fillet] Fillet440
  Base = -> Fillet439
  Edges = 2 edges r=2: [Edge17,Edge18]
FEATURE [Part::Cut] Cut503  label="Cut798"
  Base = -> Fillet440
  Refine = true
  Tool = -> Fillet438
FEATURE [Part::Box] Box582  label="Cube807"
  AttacherType = Attacher::AttachEngine3D
  Height = 6.5
  Length = 110
  Placement = pos=(19,4,121.5) rot=(0,0,1;0rad)
  Width = 162
FEATURE [Part::Box] Box583  label="Cube808"
  AttacherType = Attacher::AttachEngine3D
  Height = 5.1
  Length = 100
  Placement = pos=(19.5,5.5,122.5) rot=(0,0,1;0rad)
  Width = 159
FEATURE [Part::Fillet] Fillet441
  Base = -> Box583
  Edges = 2 edges r=10: [Edge1,Edge3]
FEATURE [Part::Fillet] Fillet442
  Base = -> Fillet441
  Edges = 2 edges r=4.5: [Edge17,Edge18]
FEATURE [Part::Fillet] Fillet443
  Base = -> Fillet442
  Edges = 4 edges r=5: [Edge1,Edge4,Edge5,Edge8]
  Placement = pos=(0.7,0,-2) rot=(0,0,1;0rad)
FEATURE [Part::Box] Box584  label="Cube809"
  AttacherType = Attacher::AttachEngine3D
  Height = 5.1
  Length = 95
  Placement = pos=(23,7.5,122.5) rot=(0,0,1;0rad)
  Width = 155
FEATURE [Part::Fillet] Fillet444
  Base = -> Box584
  Edges = 2 edges r=3: [Edge5,Edge7]
FEATURE [Part::Fillet] Fillet445
  Base = -> Fillet444
  Edges = 2 edges r=8: [Edge17,Edge18]
FEATURE [Part::Fillet] Fillet446
  Base = -> Fillet445
  Edges = 1 edges r=4: [Edge4]
  Placement = pos=(0,0,-4) rot=(0,0,1;0rad)
FEATURE [Part::Cut] Cut504  label="Cut799"
  Base = -> Fillet443
  Refine = true
  Tool = -> Fillet446
FEATURE [Part::Cylinder] Cylinder309
  Angle = 360
  AttacherType = Attacher::AttachEngine3D
  Height = 7
  Placement = pos=(2,34,15) rot=(0,1,0;1.5708rad)
  Radius = 1.2
FEATURE [Part::Cylinder] Cylinder310
  Angle = 360
  AttacherType = Attacher::AttachEngine3D
  Height = 4
  Placement = pos=(2,34,15) rot=(0,1,0;1.5708rad)
  Radius = 2.7
FEATURE [Part::MultiFuse] Fusion314
  Refine = true
  Shapes = -> [Cylinder309,Cylinder310]
FEATURE [Part::Cylinder] Cylinder311
  Angle = 360
  AttacherType = Attacher::AttachEngine3D
  Height = 4
  Placement = pos=(2,34,15) rot=(0,1,0;1.5708rad)
  Radius = 2.7
FEATURE [Part::Cylinder] Cylinder312
  Angle = 360
  AttacherType = Attacher::AttachEngine3D
  Height = 7
  Placement = pos=(2,34,15) rot=(0,1,0;1.5708rad)
  Radius = 1.2
FEATURE [Part::MultiFuse] Fusion315
  Placement = pos=(0,102,0) rot=(0,0,1;0rad)
  Refine = true
  Shapes = -> [Cylinder312,Cylinder311]
FEATURE [Part::MultiFuse] Fusion316
  Refine = true
  Shapes = -> [Fusion314,Fusion315]
FEATURE [Part::Box] Box585  label="Cube810"
  AttacherType = Attacher::AttachEngine3D
  Height = 34
  Length = 5
  Placement = pos=(7,38,2) rot=(0,0,1;0rad)
  Width = 94
FEATURE [Part::Chamfer] Chamfer068
  Base = -> Box585
  Edges = 1 edges r=4.99: [Edge6]
FEATURE [Part::Cylinder] Cylinder313
  Angle = 360
  AttacherType = Attacher::AttachEngine3D
  Height = 10
  Placement = pos=(12,57.5,21) rot=(0,1,0;1.5708rad)
  Radius = 1.25
FEATURE [Part::Cylinder] Cylinder314
  Angle = 360
  AttacherType = Attacher::AttachEngine3D
  Height = 10
  Placement = pos=(12,112.5,21) rot=(0,1,0;1.5708rad)
  Radius = 1.25
FEATURE [Part::Cylinder] Cylinder315
  Angle = 360
  AttacherType = Attacher::AttachEngine3D
  Height = 10
  Placement = pos=(12,85,16) rot=(0,1,0;1.5708rad)
  Radius = 1.25
FEATURE [Part::MultiFuse] Fusion317
  Placement = pos=(-7,0,0) rot=(0,0,1;0rad)
  Refine = true
  Shapes = -> [Cylinder313,Cylinder315,Cylinder314]
FEATURE [Part::Cylinder] Cylinder316
  Angle = 360
  AttacherType = Attacher::AttachEngine3D
  Height = 10
  Placement = pos=(118,31,59.5) rot=(0,1,0;1.5708rad)
  Radius = 1.3
FEATURE [Part::Cylinder] Cylinder317
  Angle = 360
  AttacherType = Attacher::AttachEngine3D
  Height = 10
  Placement = pos=(118,31,46.5) rot=(0,1,0;1.5708rad)
  Radius = 1.3
FEATURE [Part::MultiFuse] Fusion318
  Refine = true
  Shapes = -> [Cylinder316,Cylinder317]
FEATURE [Part::Box] Box586  label="Cube811"
  AttacherType = Attacher::AttachEngine3D
  Height = 6
  Length = 2
  Placement = pos=(89,3,29) rot=(0,0,1;0rad)
  Width = 2
FEATURE [Part::Box] Box587  label="Cube812"
  AttacherType = Attacher::AttachEngine3D
  Height = 6
  Length = 2
  Placement = pos=(105,3,29) rot=(0,0,1;0rad)
  Width = 2
FEATURE [Part::MultiFuse] Fusion319
  Refine = true
  Shapes = -> [Box586,Box587]
FEATURE [Part::Chamfer] Chamfer069
  Base = -> Fusion319
  Edges = 2 edges r=1.99: [Edge8,Edge20]
FEATURE [Part::Box] Box588  label="Cube813"
  AttacherType = Attacher::AttachEngine3D
  Height = 6
  Length = 2
  Placement = pos=(89,3,29) rot=(0,0,1;0rad)
  Width = 2
FEATURE [Part::Box] Box589  label="Cube814"
  AttacherType = Attacher::AttachEngine3D
  Height = 6
  Length = 2
  Placement = pos=(105,3,29) rot=(0,0,1;0rad)
  Width = 2
FEATURE [Part::MultiFuse] Fusion320
  Refine = true
  Shapes = -> [Box588,Box589]
FEATURE [Part::Chamfer] Chamfer070
  Base = -> Fusion320
  Edges = 2 edges r=1.99: [Edge8,Edge20]
FEATURE [Part::Mirroring] Part__Mirroring060  label="Chamfer052 (Mirror #23)001"
  Base = (0,0,0)
  Normal = (0,1,0)
  Placement = pos=(0,170,0) rot=(0,0,1;0rad)
  Source = -> Chamfer070
FEATURE [Part::Cylinder] Cylinder318
  Angle = 360
  AttacherType = Attacher::AttachEngine3D
  Height = 10
  Placement = pos=(30,11,114) rot=(1,0,0;1.5708rad)
  Radius = 1
FEATURE [Part::Cylinder] Cylinder319
  Angle = 360
  AttacherType = Attacher::AttachEngine3D
  Height = 10
  Placement = pos=(26,11,66) rot=(1,0,0;1.5708rad)
  Radius = 1
FEATURE [Part::MultiFuse] Fusion321
  Refine = true
  Shapes = -> [Cylinder318,Cylinder319]
FEATURE [Part::Cylinder] Cylinder320
  Angle = 360
  AttacherType = Attacher::AttachEngine3D
  Height = 10
  Placement = pos=(26,11,66) rot=(1,0,0;1.5708rad)
  Radius = 1
FEATURE [Part::Cylinder] Cylinder321
  Angle = 360
  AttacherType = Attacher::AttachEngine3D
  Height = 10
  Placement = pos=(30,11,114) rot=(1,0,0;1.5708rad)
  Radius = 1
FEATURE [Part::MultiFuse] Fusion322
  Refine = true
  Shapes = -> [Cylinder321,Cylinder320]
FEATURE [Part::Mirroring] Part__Mirroring061  label="Fusion203 (Mirror #26)001"
  Base = (0,0,0)
  Normal = (0,1,0)
  Placement = pos=(0,170,0) rot=(0,0,1;0rad)
  Source = -> Fusion322
FEATURE [Part::MultiFuse] Fusion323
  Refine = true
  Shapes = -> [Fusion321,Part__Mirroring061]
FEATURE [Part::Cylinder] Cylinder322
  Angle = 360
  AttacherType = Attacher::AttachEngine3D
  Height = 10
  Placement = pos=(119,65,45) rot=(0,1,0;1.5708rad)
  Radius = 1
FEATURE [Part::Cylinder] Cylinder323
  Angle = 360
  AttacherType = Attacher::AttachEngine3D
  Height = 10
  Placement = pos=(119,105,45) rot=(0,1,0;1.5708rad)
  Radius = 1
FEATURE [Part::MultiFuse] Fusion324
  Placement = pos=(0,0,2) rot=(0,0,1;0rad)
  Refine = true
  Shapes = -> [Cylinder322,Cylinder323]
FEATURE [Part::Box] Box590  label="Cube815"
  AttacherType = Attacher::AttachEngine3D
  Height = 5.1
  Length = 105
  Placement = pos=(19.5,5.5,122) rot=(0,0,1;0rad)
  Width = 159
FEATURE [Part::Box] Box591  label="Cube816"
  AttacherType = Attacher::AttachEngine3D
  Height = 5.1
  Length = 95
  Placement = pos=(23,7.5,122.5) rot=(0,0,1;0rad)
  Width = 155
FEATURE [Part::Fillet] Fillet448
  Base = -> Box591
  Edges = 2 edges r=3: [Edge5,Edge7]
FEATURE [Part::Fillet] Fillet447
  Base = -> Fillet448
  Edges = 2 edges r=8: [Edge17,Edge18]
  Placement = pos=(0,0,-5) rot=(0,0,1;0rad)
FEATURE [Part::Cylinder] Cylinder324
  Angle = 360
  AttacherType = Attacher::AttachEngine3D
  Height = 170
  Placement = pos=(26,170,120) rot=(1,0,0;1.5708rad)
  Radius = 1
FEATURE [Part::Feature] Face034
  Placement = pos=(0,0,-10) rot=(0,0,1;0rad)
  shape: bbox 128.7 x 180.4 x 2e-07 mm, 1 faces, 0 solids (baked)
FEATURE [Part::Feature] Face035
  Placement = pos=(0,0,50) rot=(0,0,1;0rad)
  shape: bbox 110 x 176 x 2e-07 mm, 1 faces, 0 solids (baked)
FEATURE [Part::Loft] Loft017
  Closed = false
  MaxDegree = 5
  Ruled = false
  Sections = -> [Face035,Face034]
  Solid = true
FEATURE [Part::Box] Box592  label="Cube817"
  AttacherType = Attacher::AttachEngine3D
  Height = 65
  Length = 67.5
  Placement = pos=(14.5,1,-1) rot=(0,0,1;0rad)
  Width = 5
FEATURE [Part::Cut] Cut505  label="Cut800"
  Base = -> Cut491
  Refine = true
  Tool = -> Box592
FEATURE [Part::Cut] Cut506  label="Cut801"
  Base = -> Cut505
  Placement = pos=(0,0.75,0) rot=(0,0,1;0rad)
  Refine = true
  Tool = -> Loft017
FEATURE [Part::Box] Box593  label="Cube818"
  AttacherType = Attacher::AttachEngine3D
  Height = 116
  Length = 66.5
  Placement = pos=(14.5,0,-0.5) rot=(0,0,1;0rad)
  Width = 5
FEATURE [Part::Box] Box594  label="Cube819"
  AttacherType = Attacher::AttachEngine3D
  Height = 117
  Length = 67.5
  Placement = pos=(14,0,-1) rot=(0,0,1;0rad)
  Width = 5
FEATURE [Part::Box] Box595  label="Cube820"
  AttacherType = Attacher::AttachEngine3D
  Height = 116
  Length = 67
  Placement = pos=(-53.2,0,65) rot=(0,1,0;0.218166rad)
  Width = 5
FEATURE [Part::Cut] Cut508  label="Cut803"
  Base = -> Box593
  Placement = pos=(0,-2,0) rot=(0,0,1;0rad)
  Refine = true
  Tool = -> Box595
FEATURE [Part::Box] Box596  label="Cube821"
  AttacherType = Attacher::AttachEngine3D
  Height = 116
  Length = 67
  Placement = pos=(-53.7,0,65) rot=(0,1,0;0.218166rad)
  Width = 5
FEATURE [Part::Cut] Cut507  label="Cut802"
  Base = -> Box594
  Placement = pos=(0,-2,0) rot=(0,0,1;0rad)
  Refine = true
  Tool = -> Box596
FEATURE [Part::Cut] Cut509  label="doors-cut-004"
  Base = -> Cut507
  Placement = pos=(0.5,3,0.5) rot=(0,0,1;0rad)
  Refine = true
  Tool = -> Cut508
FEATURE [Part::Feature] Face036
  Placement = pos=(0,0,-10) rot=(0,0,1;0rad)
  shape: bbox 128.7 x 180.4 x 2e-07 mm, 1 faces, 0 solids (baked)
FEATURE [Part::Feature] Face037
  Placement = pos=(0,0,50) rot=(0,0,1;0rad)
  shape: bbox 110 x 176 x 2e-07 mm, 1 faces, 0 solids (baked)
FEATURE [Part::Loft] Loft018
  Closed = false
  MaxDegree = 5
  Ruled = false
  Sections = -> [Face037,Face036]
  Solid = true
FEATURE [Part::Box] Box597  label="Cube822"
  AttacherType = Attacher::AttachEngine3D
  Height = 65
  Length = 67.5
  Placement = pos=(14.5,1,-1) rot=(0,0,1;0rad)
  Width = 5
FEATURE [Part::Cut] Cut510  label="Cut804"
  Base = -> Cut509
  Refine = true
  Tool = -> Box597
FEATURE [Part::Cut] Cut511  label="Cut805"
  Base = -> Cut510
  Placement = pos=(0,0.75,0) rot=(0,0,1;0rad)
  Refine = true
  Tool = -> Loft018
FEATURE [Part::Mirroring] Part__Mirroring062  label="Cut472 (Mirror #14)"
  Base = (0,0,0)
  Normal = (0,1,0)
  Placement = pos=(0,170,0) rot=(0,0,1;0rad)
  Source = -> Cut511
FEATURE [Part::MultiFuse] Fusion325
  Refine = true
  Shapes = -> [Cut506,Part__Mirroring062]
FEATURE [Part::Fillet] Fillet449
  Base = -> Fusion325
  Edges = 4 edges r=1: [Edge19,Edge23,Edge46,Edge50]
FEATURE [Part::Fillet] Fillet450
  Base = -> Fillet449
  Edges = 4 edges r=1.5: [Edge21,Edge27,Edge54,Edge60]
FEATURE [Part::Cut] Cut512  label="Cut806"
  Base = -> Cut496
  Refine = true
  Tool = -> Fillet450
FEATURE [Part::MultiFuse] Fusion256
  Refine = true
  Shapes = -> [Cut503,Cut512]
FEATURE [Part::Cut] Cut513  label="Cut807"
  Base = -> Fusion256
  Refine = true
  Tool = -> Box582
FEATURE [Part::Cut] Cut514  label="Cut808"
  Base = -> Cut513
  Refine = true
  Tool = -> Fusion323
FEATURE [Part::Fillet] Fillet341
  Base = -> Cut514
  Edges = 4 edges r=1.49: [Edge134,Edge138,Edge141,Edge142]
FEATURE [Part::MultiFuse] Fusion326
  Refine = true
  Shapes = -> [Cut504,Fillet341]
FEATURE [Part::Cut] Cut515  label="Cut809"
  Base = -> Fusion326
  Refine = true
  Tool = -> Box590
FEATURE [Part::Cut] Cut516  label="Cut810"
  Base = -> Cut515
  Refine = true
  Tool = -> Fillet447
FEATURE [Part::Cut] Cut517  label="Cut811"
  Base = -> Cut516
  Refine = true
  Tool = -> Cylinder324
FEATURE [Part::Fillet] Fillet342  label="cab-upper-part-02"
  Base = -> Cut517
  Edges = 6 edges r=0.5: [Edge347,Edge361,Edge367,Edge386,Edge396,Edge398]
FEATURE [Part::MultiFuse] Fusion327
  Refine = true
  Shapes = -> [Cut502,Fillet433]
FEATURE [Part::MultiFuse] Fusion328
  Refine = true
  Shapes = -> [Cut502,Fillet433]
FEATURE [Part::Cut] Cut518  label="Cut812"
  Base = -> Cut493
  Placement = pos=(-1,0,0) rot=(0,0,1;0rad)
  Refine = true
  Tool = -> Fusion327
FEATURE [Part::Box] Box598  label="Cube823"
  AttacherType = Attacher::AttachEngine3D
  Height = 53
  Length = 67.5
  Placement = pos=(14.5,-5,64) rot=(0,0,1;0rad)
  Width = 10
FEATURE [Part::Cut] Cut519  label="Cut813"
  Base = -> Cut518
  Placement = pos=(0,0.75,0) rot=(0,0,1;0rad)
  Refine = true
  Tool = -> Box598
FEATURE [Part::Box] Box599  label="Cube824"
  AttacherType = Attacher::AttachEngine3D
  Height = 64
  Length = 126
  Width = 170
FEATURE [Part::Fillet] Fillet344
  Base = -> Box599
  Edges = 2 edges r=15: [Edge1,Edge3]
FEATURE [Part::Fillet] Fillet343
  Base = -> Fillet344
  Edges = 2 edges r=10: [Edge17,Edge18]
FEATURE [Part::Box] Box600  label="Cube825"
  AttacherType = Attacher::AttachEngine3D
  Height = 64
  Length = 120
  Placement = pos=(4,4,0) rot=(0,0,1;0rad)
  Width = 164
FEATURE [Part::Fillet] Fillet346
  Base = -> Box600
  Edges = 2 edges r=12: [Edge1,Edge3]
FEATURE [Part::Fillet] Fillet345
  Base = -> Fillet346
  Edges = 2 edges r=6: [Edge17,Edge18]
  Placement = pos=(-1,-1,0) rot=(0,0,1;0rad)
FEATURE [Part::Cut] Cut521  label="Cut815"
  Base = -> Fillet343
  Refine = true
  Tool = -> Fillet345
FEATURE [Part::Cylinder] Cylinder325
  Angle = 360
  AttacherType = Attacher::AttachEngine3D
  Height = 174
  Placement = pos=(98,174,-23) rot=(1,0,0;1.5708rad)
  Radius = 52
FEATURE [Part::Cut] Cut520  label="Cut814"
  Base = -> Cut521
  Refine = true
  Tool = -> Cylinder325
FEATURE [Part::Box] Box601  label="Cube826"
  AttacherType = Attacher::AttachEngine3D
  Height = 25
  Length = 131
  Placement = pos=(11,0,6) rot=(0,0,1;0rad)
  Width = 170
FEATURE [Part::Box] Box602  label="Cube827"
  AttacherType = Attacher::AttachEngine3D
  Height = 25
  Length = 148
  Placement = pos=(2,2,6) rot=(0,0,1;0rad)
  Width = 166
FEATURE [Part::Box] Box603  label="Cube828"
  AttacherType = Attacher::AttachEngine3D
  Height = 31
  Length = 62
  Placement = pos=(83,1,2) rot=(0,0,1;0rad)
  Width = 1
FEATURE [Part::Box] Box604  label="Cube829"
  AttacherType = Attacher::AttachEngine3D
  Height = 31
  Length = 63.5
  Placement = pos=(83,-1,2) rot=(0,0,1;0.017453rad)
  Width = 2
FEATURE [Part::Cut] Cut523  label="Cut817"
  Base = -> Box603
  Refine = true
  Tool = -> Box604
FEATURE [Part::Cylinder] Cylinder326
  Angle = 360
  AttacherType = Attacher::AttachEngine3D
  Height = 10
  Placement = pos=(98,10,-23) rot=(1,0,0;1.5708rad)
  Radius = 52
FEATURE [Part::Cut] Cut522  label="Cut816"
  Base = -> Cut523
  Refine = true
  Tool = -> Cylinder326
FEATURE [Part::Cylinder] Cylinder327
  Angle = 360
  AttacherType = Attacher::AttachEngine3D
  Height = 10
  Placement = pos=(98,10,-23) rot=(1,0,0;1.5708rad)
  Radius = 52
FEATURE [Part::Box] Box605  label="Cube830"
  AttacherType = Attacher::AttachEngine3D
  Height = 25
  Length = 63.5
  Placement = pos=(20,1,8) rot=(0,0,-1;0.027925rad)
  Width = 1
FEATURE [Part::Box] Box606  label="Cube831"
  AttacherType = Attacher::AttachEngine3D
  Height = 25
  Length = 62.5
  Placement = pos=(20.5,1,8) rot=(0,0,1;0rad)
  Width = 1
FEATURE [Part::Cut] Cut525  label="Cut819"
  Base = -> Box606
  Refine = true
  Tool = -> Box605
FEATURE [Part::Cut] Cut524  label="Cut818"
  Base = -> Cut525
  Refine = true
  Tool = -> Cylinder327
FEATURE [Part::MultiFuse] Fusion260
  Refine = true
  Shapes = -> [Cut522,Cut524]
FEATURE [Part::Box] Box607  label="Cube832"
  AttacherType = Attacher::AttachEngine3D
  Height = 25
  Length = 63.5
  Placement = pos=(20,1,8) rot=(0,0,-1;0.027925rad)
  Width = 1
FEATURE [Part::Box] Box608  label="Cube833"
  AttacherType = Attacher::AttachEngine3D
  Height = 25
  Length = 62.5
  Placement = pos=(20.5,1,8) rot=(0,0,1;0rad)
  Width = 1
FEATURE [Part::Cut] Cut528  label="Cut822"
  Base = -> Box608
  Refine = true
  Tool = -> Box607
FEATURE [Part::Box] Box609  label="Cube834"
  AttacherType = Attacher::AttachEngine3D
  Height = 31
  Length = 63.5
  Placement = pos=(83,-1,2) rot=(0,0,1;0.017453rad)
  Width = 2
FEATURE [Part::Box] Box610  label="Cube835"
  AttacherType = Attacher::AttachEngine3D
  Height = 31
  Length = 62
  Placement = pos=(83,1,2) rot=(0,0,1;0rad)
  Width = 1
FEATURE [Part::Cut] Cut526  label="Cut820"
  Base = -> Box610
  Refine = true
  Tool = -> Box609
FEATURE [Part::Cylinder] Cylinder328
  Angle = 360
  AttacherType = Attacher::AttachEngine3D
  Height = 10
  Placement = pos=(98,10,-23) rot=(1,0,0;1.5708rad)
  Radius = 52
FEATURE [Part::Cut] Cut529  label="Cut823"
  Base = -> Cut526
  Refine = true
  Tool = -> Cylinder328
FEATURE [Part::Cylinder] Cylinder329
  Angle = 360
  AttacherType = Attacher::AttachEngine3D
  Height = 10
  Placement = pos=(98,10,-23) rot=(1,0,0;1.5708rad)
  Radius = 52
FEATURE [Part::Cut] Cut527  label="Cut821"
  Base = -> Cut528
  Refine = true
  Tool = -> Cylinder329
FEATURE [Part::MultiFuse] Fusion329
  Refine = true
  Shapes = -> [Cut529,Cut527]
FEATURE [Part::Mirroring] Part__Mirroring063  label="Fusion008 (Mirror #2)002"
  Base = (0,0,0)
  Normal = (0,1,0)
  Placement = pos=(0,170,0) rot=(0,0,1;0rad)
  Source = -> Fusion329
FEATURE [Part::MultiFuse] Fusion262
  Refine = true
  Shapes = -> [Part__Mirroring063,Fusion260]
FEATURE [Part::Cut] Cut530  label="Cut824"
  Base = -> Box601
  Placement = pos=(0,0,2) rot=(0,0,1;0rad)
  Refine = true
  Tool = -> Box602
FEATURE [Part::Cut] Cut531  label="Cut825"
  Base = -> Cut530
  Placement = pos=(0,0,-3) rot=(0,0,1;0rad)
  Refine = true
  Tool = -> Fusion262
FEATURE [Part::Cut] Cut532  label="Cut826"
  Base = -> Cut520
  Refine = true
  Tool = -> Cut531
FEATURE [Part::Box] Box611  label="Cube836"
  AttacherType = Attacher::AttachEngine3D
  Height = 64
  Length = 21
  Width = 164
FEATURE [Part::Fillet] Fillet347
  Base = -> Box611
  Edges = 2 edges r=12: [Edge1,Edge3]
  Placement = pos=(3,3,0) rot=(0,0,1;0rad)
FEATURE [Part::Box] Box612  label="Cube837"
  AttacherType = Attacher::AttachEngine3D
  Height = 59
  Length = 16
  Placement = pos=(15,0,0) rot=(0,0,1;0rad)
  Width = 170
FEATURE [Part::Box] Box613  label="Cube838"
  AttacherType = Attacher::AttachEngine3D
  Height = 59
  Length = 21
  Placement = pos=(-13,3,0) rot=(0,0,1;0rad)
  Width = 164
FEATURE [Part::Box] Box614  label="Cube839"
  AttacherType = Attacher::AttachEngine3D
  Height = 59
  Length = 21
  Placement = pos=(-13,0,0) rot=(0,0,1;0rad)
  Width = 170
FEATURE [Part::Fillet] Fillet348
  Base = -> Box614
  Edges = 2 edges r=15: [Edge1,Edge3]
FEATURE [Part::Fillet] Fillet349
  Base = -> Box613
  Edges = 2 edges r=12: [Edge1,Edge3]
  Placement = pos=(3,0,0) rot=(0,0,1;0rad)
FEATURE [Part::Cut] Cut533  label="Cut827"
  Base = -> Fillet348
  Placement = pos=(13,0,0) rot=(0,0,1;0rad)
  Refine = true
  Tool = -> Fillet349
FEATURE [Part::Cut] Cut534  label="Cut828"
  Base = -> Cut533
  Refine = true
  Tool = -> Box612
FEATURE [Part::Chamfer] Chamfer071
  Base = -> Cut532
  Edges = 4 edges r=2.5: [Edge1,Edge4,Edge5,Edge8]
FEATURE [Part::Chamfer] Chamfer072
  Base = -> Chamfer071
  Edges = 4 edges r=0.9: [Edge52,Edge80,Edge102,Edge110]
FEATURE [Part::Box] Box615  label="Cube840"
  AttacherType = Attacher::AttachEngine3D
  Height = 25
  Length = 10
  Placement = pos=(150,40,0) rot=(0,0,1;0rad)
  Width = 100
FEATURE [Part::Box] Box616  label="Cube841"
  AttacherType = Attacher::AttachEngine3D
  Height = 40
  Length = 10
  Placement = pos=(150,19,0) rot=(-1,0,0;0.383972rad)
  Width = 20
FEATURE [Part::Box] Box617  label="Cube842"
  AttacherType = Attacher::AttachEngine3D
  Height = 40
  Length = 10
  Placement = pos=(150,19,0) rot=(-1,0,0;0.383972rad)
  Width = 20
FEATURE [Part::Mirroring] Part__Mirroring064  label="Cube088 (Mirror #13)002"
  Base = (0,0,0)
  Normal = (0,1,0)
  Placement = pos=(0,180,0) rot=(0,0,1;0rad)
  Source = -> Box617
FEATURE [Part::MultiFuse] Fusion330
  Refine = true
  Shapes = -> [Box616,Part__Mirroring064]
FEATURE [Part::Cut] Cut535  label="Cut829"
  Base = -> Box615
  Placement = pos=(-30,-5,20) rot=(0,0,1;0rad)
  Refine = true
  Tool = -> Fusion330
FEATURE [Part::Fillet] Fillet350
  Base = -> Cut535
  Edges = 2 edges r=6: [Edge5,Edge6]
FEATURE [Part::Cylinder] Cylinder330
  Angle = 360
  AttacherType = Attacher::AttachEngine3D
  Height = 134
  Radius = 3.7
FEATURE [Part::Fillet] Fillet351
  Base = -> Cylinder330
  Edges = 2 edges r=2: [Edge1,Edge3]
  Placement = pos=(128,152,53) rot=(1,0,0;1.5708rad)
FEATURE [Part::Box] Box618  label="Cube843"
  AttacherType = Attacher::AttachEngine3D
  Height = 9
  Length = 14
  Width = 2
FEATURE [Part::Fillet] Fillet352
  Base = -> Box618
  Edges = 4 edges r=2: [Edge2,Edge4,Edge6,Edge8]
  Placement = pos=(68.5,0,46.5) rot=(0,0,1;0rad)
FEATURE [Part::Box] Box619  label="Cube844"
  AttacherType = Attacher::AttachEngine3D
  Height = 9
  Length = 14
  Width = 2
FEATURE [Part::Fillet] Fillet353
  Base = -> Box619
  Edges = 4 edges r=2: [Edge2,Edge4,Edge6,Edge8]
  Placement = pos=(68.5,168,46.5) rot=(0,0,1;0rad)
FEATURE [Part::MultiFuse] Fusion331
  Placement = pos=(-4,0,-13) rot=(0,0,1;0rad)
  Refine = true
  Shapes = -> [Fillet353,Fillet352]
FEATURE [Part::Box] Box620  label="Cube845"
  AttacherType = Attacher::AttachEngine3D
  Height = 116
  Length = 67
  Placement = pos=(-53.2,0,65) rot=(0,1,0;0.218166rad)
  Width = 10
FEATURE [Part::Box] Box621  label="Cube846"
  AttacherType = Attacher::AttachEngine3D
  Height = 116
  Length = 67
  Placement = pos=(-53.7,0,65) rot=(0,1,0;0.218166rad)
  Width = 10
FEATURE [Part::Box] Box622  label="Cube847"
  AttacherType = Attacher::AttachEngine3D
  Height = 117
  Length = 67.5
  Placement = pos=(14,0,-1) rot=(0,0,1;0rad)
  Width = 10
FEATURE [Part::Cut] Cut537  label="Cut830"
  Base = -> Box622
  Placement = pos=(0,-2,0) rot=(0,0,1;0rad)
  Refine = true
  Tool = -> Box621
FEATURE [Part::Box] Box623  label="Cube848"
  AttacherType = Attacher::AttachEngine3D
  Height = 116
  Length = 66.5
  Placement = pos=(14.5,0,-0.5) rot=(0,0,1;0rad)
  Width = 10
FEATURE [Part::Cut] Cut538  label="Cut831"
  Base = -> Box623
  Placement = pos=(0,-2,0) rot=(0,0,1;0rad)
  Refine = true
  Tool = -> Box620
FEATURE [Part::Cut] Cut536  label="doors-cut-005"
  Base = -> Cut537
  Placement = pos=(1.5,-3,0.5) rot=(0,0,1;0rad)
  Refine = true
  Tool = -> Cut538
FEATURE [Part::Box] Box624  label="Cube849"
  AttacherType = Attacher::AttachEngine3D
  Height = 64
  Length = 21
  Width = 164
FEATURE [Part::Fillet] Fillet354
  Base = -> Box624
  Edges = 2 edges r=18: [Edge1,Edge3]
  Placement = pos=(7,3,0) rot=(0,0,1;0rad)
FEATURE [Part::Cut] Cut539  label="Cut832"
  Base = -> Fillet347
  Refine = true
  Tool = -> Fillet354
FEATURE [Part::MultiFuse] Fusion265
  Refine = true
  Shapes = -> [Chamfer072,Cut539]
FEATURE [Part::Cut] Cut540  label="Cut833"
  Base = -> Fusion265
  Refine = true
  Tool = -> Cut534
FEATURE [Part::Cut] Cut541  label="Cut834"
  Base = -> Cut540
  Refine = true
  Tool = -> Fillet351
FEATURE [Part::Cut] Cut542  label="Cut835"
  Base = -> Cut541
  Refine = true
  Tool = -> Fillet350
FEATURE [Part::Cut] Cut543  label="Cut836"
  Base = -> Cut542
  Refine = true
  Tool = -> Fusion331
FEATURE [Part::Fillet] Fillet355
  Base = -> Cut543
  Edges = 2 edges r=3: [Edge74,Edge149]
FEATURE [Part::Box] Box456  label="Cube681"
  AttacherType = Attacher::AttachEngine3D
  Height = 2
  Length = 117
  Placement = pos=(6,3,54) rot=(0,0,1;0rad)
  Width = 164
FEATURE [Part::Fillet] Fillet451
  Base = -> Box456
  Edges = 2 edges r=15: [Edge1,Edge3]
FEATURE [Part::Fillet] Fillet452
  Base = -> Fillet451
  Edges = 2 edges r=6: [Edge17,Edge18]
FEATURE [Part::Box] Box457  label="Cube682"
  AttacherType = Attacher::AttachEngine3D
  Height = 2
  Length = 111
  Placement = pos=(6,3,54) rot=(0,0,1;0rad)
  Width = 158
FEATURE [Part::Fillet] Fillet359
  Base = -> Box457
  Edges = 2 edges r=12: [Edge1,Edge3]
FEATURE [Part::Fillet] Fillet358
  Base = -> Fillet359
  Edges = 2 edges r=3: [Edge17,Edge18]
  Placement = pos=(3,3,0) rot=(0,0,1;0rad)
FEATURE [Part::Cut] Cut544  label="Cut837"
  Base = -> Fillet452
  Placement = pos=(0,0,8) rot=(0,0,1;0rad)
  Refine = true
  Tool = -> Fillet358
FEATURE [Part::MultiFuse] Fusion332
  Refine = true
  Shapes = -> [Cut544,Fillet355]
FEATURE [Part::Cut] Cut545  label="Cut838"
  Base = -> Cut536
  Placement = pos=(-1,0,0) rot=(0,0,1;0rad)
  Refine = true
  Tool = -> Fusion332
FEATURE [Part::Box] Box625  label="Cube850"
  AttacherType = Attacher::AttachEngine3D
  Height = 53
  Length = 67.5
  Placement = pos=(14.5,-5,64) rot=(0,0,1;0rad)
  Width = 10
FEATURE [Part::Cut] Cut546  label="Cut839"
  Base = -> Cut545
  Placement = pos=(0,0.75,0) rot=(0,0,1;0rad)
  Refine = true
  Tool = -> Box625
FEATURE [Part::Mirroring] Part__Mirroring065  label="Cut674 (Mirror #17)"
  Base = (0,0,0)
  Normal = (0,1,0)
  Placement = pos=(0,170,0) rot=(0,0,1;0rad)
  Source = -> Cut546
FEATURE [Part::MultiFuse] Fusion333
  Refine = true
  Shapes = -> [Part__Mirroring065,Cut519]
FEATURE [Part::Cut] Cut547  label="Cut840"
  Base = -> Fusion328
  Refine = true
  Tool = -> Fusion316
FEATURE [Part::MultiFuse] Fusion268
  Refine = true
  Shapes = -> [Cut547,Chamfer068]
FEATURE [Part::Cut] Cut548  label="Cut841"
  Base = -> Fusion268
  Refine = true
  Tool = -> Fusion317
FEATURE [Part::Cut] Cut549  label="Cut842"
  Base = -> Cut548
  Refine = true
  Tool = -> Fusion318
FEATURE [Part::MultiFuse] Fusion269
  Refine = true
  Shapes = -> [Cut549,Part__Mirroring060,Chamfer069]
FEATURE [Part::Cut] Cut550  label="Cut843"
  Base = -> Fusion269
  Refine = true
  Tool = -> Fusion324
FEATURE [Part::Cut] Cut551  label="Cut844"
  Base = -> Cut550
  Refine = true
  Tool = -> Fusion333
FEATURE [Part::Chamfer] Chamfer073
  Base = -> Cut551
  Edges = 1 edges r=0.9: [Edge349]
FEATURE [Part::Fillet] Fillet360
  Base = -> Chamfer073
  Edges = 2 edges r=4: [Edge145,Edge282]
FEATURE [Part::Fillet] Fillet361
  Base = -> Fillet360
  Edges = 10 edges r=0.5: [Edge150,Edge164,Edge165,Edge279,Edge281,Edge289,Edge291,Edge301,Edge361,Edge362]
FEATURE [Part::Fillet] Fillet362
  Base = -> Fillet361
  Edges = 2 edges r=0.49: [Edge141,Edge160]
FEATURE [Part::Cylinder] Cylinder331
  Angle = 360
  AttacherType = Attacher::AttachEngine3D
  Height = 11.5
  Placement = pos=(12,10.7,16) rot=(0.881271,-0.370227,-0.293757;1.67552rad)
  Radius = 1.2
FEATURE [Part::Cylinder] Cylinder332
  Angle = 360
  AttacherType = Attacher::AttachEngine3D
  Height = 11.5
  Placement = pos=(12,10.7,51) rot=(0.881271,-0.370227,-0.293757;1.67552rad)
  Radius = 1.2
FEATURE [Part::MultiFuse] Fusion334
  Refine = true
  Shapes = -> [Cylinder331,Cylinder332]
FEATURE [Part::Cylinder] Cylinder333
  Angle = 360
  AttacherType = Attacher::AttachEngine3D
  Height = 11.5
  Placement = pos=(12,10.7,16) rot=(0.881271,-0.370227,-0.293757;1.67552rad)
  Radius = 1.2
FEATURE [Part::Cylinder] Cylinder334
  Angle = 360
  AttacherType = Attacher::AttachEngine3D
  Height = 11.5
  Placement = pos=(12,10.7,51) rot=(0.881271,-0.370227,-0.293757;1.67552rad)
  Radius = 1.2
FEATURE [Part::MultiFuse] Fusion274
  Refine = true
  Shapes = -> [Cylinder333,Cylinder334]
FEATURE [Part::Mirroring] Part__Mirroring066  label="Fusion274 (Mirror #18)"
  Base = (0,0,0)
  Normal = (0,1,0)
  Placement = pos=(0,170,0) rot=(0,0,1;0rad)
  Source = -> Fusion274
FEATURE [Part::MultiFuse] Fusion275
  Refine = true
  Shapes = -> [Fusion334,Part__Mirroring066]
FEATURE [Part::Cut] Cut552  label="cab-lower-part-06"
  Base = -> Fillet362
  Refine = true
  Tool = -> Fusion275
FEATURE [Part::MultiFuse] Fusion335  label="windows-frames"
  Refine = true
  Shapes = -> [Fillet167,Part__Mirroring022,Fillet224,Part__Mirroring024,Fillet231,Fillet268]
FEATURE [Part::Cylinder] Cylinder335
  Angle = 79
  AttacherType = Attacher::AttachEngine3D
  Height = 62
  Placement = pos=(25,21,0) rot=(0,0,1;3.28122rad)
  Radius = 29
FEATURE [Part::Cylinder] Cylinder336
  Angle = 360
  AttacherType = Attacher::AttachEngine3D
  Height = 62
  Placement = pos=(25,21,0) rot=(0,0,1;0rad)
  Radius = 18
FEATURE [Part::Cut] Cut553  label="Cut845"
  Base = -> Cylinder335
  Refine = true
  Tool = -> Cylinder336
FEATURE [Part::Box] Box626  label="Cube851"
  AttacherType = Attacher::AttachEngine3D
  Height = 2
  Length = 48
  Placement = pos=(5,3,0) rot=(0,0,1;0rad)
  Width = 15
FEATURE [Part::Cylinder] Cylinder337
  Angle = 360
  AttacherType = Attacher::AttachEngine3D
  Height = 62
  Placement = pos=(25,21,0) rot=(0,0,1;0rad)
  Radius = 16.5
FEATURE [Part::Cylinder] Cylinder338
  Angle = 46
  AttacherType = Attacher::AttachEngine3D
  Height = 62
  Placement = pos=(25,21,0) rot=(0,0,1;3.3074rad)
  Radius = 18
FEATURE [Part::Cut] Cut554  label="Cut846"
  Base = -> Cylinder338
  Refine = true
  Tool = -> Cylinder337
FEATURE [Part::Cut] Cut555  label="Cut847"
  Base = -> Box626
  Refine = true
  Tool = -> Cut553
FEATURE [Part::Box] Box627  label="Cube852"
  AttacherType = Attacher::AttachEngine3D
  Height = 62
  Length = 3
  Placement = pos=(6,18,0) rot=(0,0,1;0rad)
  Width = 1
FEATURE [Part::Cut] Cut556  label="Cut848"
  Base = -> Cut554
  Refine = true
  Tool = -> Box627
FEATURE [Part::Cylinder] Cylinder339
  Angle = 360
  AttacherType = Attacher::AttachEngine3D
  Height = 22
  Placement = pos=(98,18,-23) rot=(1,0,0;1.5708rad)
  Radius = 52
FEATURE [Part::Cut] Cut557  label="Cut849"
  Base = -> Cut555
  Refine = true
  Tool = -> Cylinder339
FEATURE [Part::Cylinder] Cylinder340
  Angle = 360
  AttacherType = Attacher::AttachEngine3D
  Height = 13
  Placement = pos=(11.9886,10.7385,16) rot=(0.884029,-0.330525,-0.330525;1.69375rad)
  Radius = 1.2
FEATURE [Part::Cylinder] Cylinder341
  Angle = 360
  AttacherType = Attacher::AttachEngine3D
  Height = 13
  Placement = pos=(11.9886,10.7385,51) rot=(0.884029,-0.330525,-0.330525;1.69375rad)
  Radius = 1.2
FEATURE [Part::MultiFuse] Fusion336
  Placement = pos=(0.87,1,0) rot=(0,0,1;0rad)
  Refine = true
  Shapes = -> [Cylinder340,Cylinder341]
FEATURE [Part::Cylinder] Cylinder342
  Angle = 360
  AttacherType = Attacher::AttachEngine3D
  Height = 1.6
  Placement = pos=(11.9886,10.7385,16) rot=(0.884029,-0.330525,-0.330525;1.69375rad)
  Radius = 2
FEATURE [Part::Cylinder] Cylinder343
  Angle = 360
  AttacherType = Attacher::AttachEngine3D
  Height = 1.6
  Placement = pos=(11.9886,10.7385,51) rot=(0.884029,-0.330525,-0.330525;1.69375rad)
  Radius = 2
FEATURE [Part::MultiFuse] Fusion337
  Placement = pos=(0.87,1,0) rot=(0,0,1;0rad)
  Refine = true
  Shapes = -> [Cylinder342,Cylinder343]
FEATURE [Part::MultiFuse] Fusion338
  Refine = true
  Shapes = -> [Cut556,Cut557,Fusion337]
FEATURE [Part::Cut] Cut558  label="Cut850"
  Base = -> Fusion338
  Refine = true
  Tool = -> Fusion336
FEATURE [Part::Cylinder] Cylinder344
  Angle = 360
  AttacherType = Attacher::AttachEngine3D
  Height = 10
  Placement = pos=(18,15,-5) rot=(0,0,1;0rad)
  Radius = 1.2
FEATURE [Part::Cylinder] Cylinder345
  Angle = 360
  AttacherType = Attacher::AttachEngine3D
  Height = 10
  Placement = pos=(49,15,-5) rot=(0,0,1;0rad)
  Radius = 1.2
FEATURE [Part::MultiFuse] Fusion339
  Refine = true
  Shapes = -> [Cylinder344,Cylinder345]
FEATURE [Part::Cut] Cut559  label="inner-door-swing-arm-left001"
  Base = -> Cut558
  Refine = true
  Tool = -> Fusion339
FEATURE [Part::Mirroring] Part__Mirroring067  label="inner-door-swing-arm-right"
  Base = (0,0,0)
  Normal = (0,1,0)
  Placement = pos=(0,170,0) rot=(0,0,1;0rad)
  Source = -> Cut559
FEATURE [Part::Cylinder] Cylinder346
  Angle = 360
  AttacherType = Attacher::AttachEngine3D
  Height = 10
  Placement = pos=(13,13,0) rot=(0,0,1;3.38594rad)
  Radius = 14
FEATURE [Part::Fillet] Fillet453
  Base = -> Cylinder346
  Edges = 4 edges r=1: [Edge1,Edge2,Edge3,Edge4]
FEATURE [Part::Cylinder] Cylinder347
  Angle = 360
  AttacherType = Attacher::AttachEngine3D
  Height = 10
  Placement = pos=(13,13,0) rot=(0,0,1;3.38594rad)
  Radius = 12.7
FEATURE [Part::Cut] Cut560  label="front-turning-light-left-TRANSPARENT"
  Base = -> Fillet453
  Refine = true
  Tool = -> Cylinder347
FEATURE [Part::Cylinder] Cylinder350
  Angle = 360
  AttacherType = Attacher::AttachEngine3D
  Height = 11.5
  Placement = pos=(12,10.7,16) rot=(0.881271,-0.370227,-0.293757;1.67552rad)
  Radius = 1.2
FEATURE [Part::Cylinder] Cylinder351
  Angle = 360
  AttacherType = Attacher::AttachEngine3D
  Height = 11.5
  Placement = pos=(12,10.7,51) rot=(0.881271,-0.370227,-0.293757;1.67552rad)
  Radius = 1.2
FEATURE [Part::MultiFuse] Fusion340
  Refine = true
  Shapes = -> [Cylinder350,Cylinder351]
FEATURE [Part::Cylinder] Cylinder352
  Angle = 360
  AttacherType = Attacher::AttachEngine3D
  Height = 11.5
  Placement = pos=(12,10.7,16) rot=(0.881271,-0.370227,-0.293757;1.67552rad)
  Radius = 1.2
FEATURE [Part::Cylinder] Cylinder353
  Angle = 360
  AttacherType = Attacher::AttachEngine3D
  Height = 11.5
  Placement = pos=(12,10.7,51) rot=(0.881271,-0.370227,-0.293757;1.67552rad)
  Radius = 1.2
FEATURE [Part::MultiFuse] Fusion341
  Refine = true
  Shapes = -> [Cylinder352,Cylinder353]
FEATURE [Part::Mirroring] Part__Mirroring069  label="Fusion274 (Mirror #18)001"
  Base = (0,0,0)
  Normal = (0,1,0)
  Placement = pos=(0,170,0) rot=(0,0,1;0rad)
  Source = -> Fusion341
FEATURE [Part::MultiFuse] Fusion342
  Refine = true
  Shapes = -> [Fusion340,Part__Mirroring069]
FEATURE [Part::Cut] Cut562  label="Cut851"
  Base = -> Chamfer054
  Refine = true
  Tool = -> Fusion342
FEATURE [Part::Cut] Cut563  label="Cut852"
  Base = -> Cylinder076
  Refine = true
  Tool = -> Cylinder077
FEATURE [Part::Cylinder] Cylinder356
  Angle = 360
  AttacherType = Attacher::AttachEngine3D
  Height = 10
  Placement = pos=(13,13,0) rot=(0,0,1;3.38594rad)
  Radius = 14
FEATURE [Part::Fillet] Fillet461
  Base = -> Cylinder356
  Edges = 4 edges r=1: [Edge1,Edge2,Edge3,Edge4]
FEATURE [Part::Cylinder] Cylinder357
  Angle = 360
  AttacherType = Attacher::AttachEngine3D
  Height = 10
  Placement = pos=(13,13,0) rot=(0,0,1;3.38594rad)
  Radius = 12.7
FEATURE [Part::Cut] Cut565  label="Cut853"
  Base = -> Fillet461
  Refine = true
  Tool = -> Cylinder357
FEATURE [Part::Mirroring] Part__Mirroring071  label="front-turning-light-right-TRANSPARENT"
  Base = (0,0,0)
  Normal = (0,1,0)
  Placement = pos=(0,170,0) rot=(0,0,1;0rad)
  Source = -> Cut565
FEATURE [Part::Fillet] Fillet462
  Base = -> Cut563
  Edges = 2 edges r=2.5: [Edge9,Edge12]
FEATURE [Part::Cylinder] Cylinder360
  Angle = 53
  AttacherType = Attacher::AttachEngine3D
  Height = 10
  Placement = pos=(13,13,0) rot=(0,0,1;3.38594rad)
  Radius = 12.6
FEATURE [Part::Cylinder] Cylinder361
  Angle = 360
  AttacherType = Attacher::AttachEngine3D
  Height = 10
  Placement = pos=(13,13,0) rot=(0,0,1;3.38594rad)
  Radius = 10
FEATURE [Part::Cut] Cut566  label="Cut854"
  Base = -> Cylinder360
  Refine = true
  Tool = -> Cylinder361
FEATURE [Part::Fillet] Fillet463
  Base = -> Cut566
  Edges = 2 edges r=2.5: [Edge9,Edge12]
FEATURE [Part::Mirroring] Part__Mirroring072  label="Fillet463 (Mirror #56)"
  Base = (0,0,0)
  Normal = (0,1,0)
  Placement = pos=(0,170,0) rot=(0,0,1;0rad)
  Source = -> Fillet463
FEATURE [Part::MultiFuse] Fusion346
  Refine = true
  Shapes = -> [Fillet462,Part__Mirroring072]
FEATURE [Part::MultiFuse] Fusion347
  Refine = true
  Shapes = -> [Cut562,Fusion346]
FEATURE [Part::Cylinder] Cylinder362
  Angle = 360
  AttacherType = Attacher::AttachEngine3D
  Height = 11.5
  Placement = pos=(10,10.7,5) rot=(0.842437,-0.416131,-0.342251;1.7144rad)
  Radius = 1.6
FEATURE [Part::Cylinder] Cylinder363
  Angle = 360
  AttacherType = Attacher::AttachEngine3D
  Height = 11.5
  Placement = pos=(10,10.7,5) rot=(0.842437,-0.416131,-0.342251;1.7144rad)
  Radius = 1.6
FEATURE [Part::Mirroring] Part__Mirroring073  label="Cylinder363 (Mirror #56)"
  Base = (0,0,0)
  Normal = (0,1,0)
  Placement = pos=(0,170,0) rot=(0,0,1;0rad)
  Source = -> Cylinder363
FEATURE [Part::MultiFuse] Fusion348
  Refine = true
  Shapes = -> [Part__Mirroring073,Cylinder362]
FEATURE [Part::Cut] Cut567  label="front-panel"
  Base = -> Fusion347
  Refine = true
  Tool = -> Fusion348
FEATURE [Part::Box] Box628  label="Cube853"
  AttacherType = Attacher::AttachEngine3D
  Height = 5.8
  Length = 13.6
  Placement = pos=(91.2,163,27) rot=(0,0,1;0rad)
  Width = 4
FEATURE [Part::Box] Box629  label="Cube854"
  AttacherType = Attacher::AttachEngine3D
  Height = 23
  Length = 37
  Placement = pos=(15,152,-23) rot=(0,0,1;0rad)
  Width = 18
FEATURE [Part::Cylinder] Cylinder364
  Angle = 360
  AttacherType = Attacher::AttachEngine3D
  Height = 22
  Placement = pos=(98,174,-23) rot=(1,0,0;1.5708rad)
  Radius = 52
FEATURE [Part::Box] Box630  label="Cube855"
  AttacherType = Attacher::AttachEngine3D
  Height = 9
  Length = 31
  Placement = pos=(17,156,-29) rot=(0,0,1;0rad)
  Width = 14
FEATURE [Part::Cylinder] Cylinder365
  Angle = 360
  AttacherType = Attacher::AttachEngine3D
  Height = 22
  Placement = pos=(98,174,-23) rot=(1,0,0;1.5708rad)
  Radius = 54
FEATURE [Part::Box] Box631  label="Cube856"
  AttacherType = Attacher::AttachEngine3D
  Height = 7.5
  Length = 4
  Placement = pos=(44,152,-31) rot=(0,0,1;0rad)
  Width = 22
FEATURE [Part::Box] Box632  label="Cube857"
  AttacherType = Attacher::AttachEngine3D
  Height = 18
  Length = 31
  Placement = pos=(17,158,-20) rot=(0,0,1;0rad)
  Width = 12
FEATURE [Part::Cylinder] Cylinder366
  Angle = 360
  AttacherType = Attacher::AttachEngine3D
  Height = 22
  Placement = pos=(98,174,-23) rot=(1,0,0;1.5708rad)
  Radius = 54
FEATURE [Part::Cut] Cut568  label="Cut860"
  Base = -> Box632
  Refine = true
  Tool = -> Cylinder366
FEATURE [Part::Box] Box633  label="Cube858"
  AttacherType = Attacher::AttachEngine3D
  Height = 21
  Length = 38
  Placement = pos=(15,167,-23) rot=(0,0,1;0rad)
  Width = 3
FEATURE [Part::Box] Box634  label="Cube859"
  AttacherType = Attacher::AttachEngine3D
  Height = 7
  Length = 10
  Placement = pos=(46,152,-30) rot=(0,0,1;0rad)
  Width = 25
FEATURE [Part::Cylinder] Cylinder367
  Angle = 360
  AttacherType = Attacher::AttachEngine3D
  Height = 25
  Placement = pos=(98,177,-23) rot=(0.799251,-0.424969,0.424969;1.79303rad)
  Radius = 52
FEATURE [Part::Cylinder] Cylinder368
  Angle = 360
  AttacherType = Attacher::AttachEngine3D
  Height = 28
  Placement = pos=(98,175,-23) rot=(0.799251,-0.424969,0.424969;1.79303rad)
  Radius = 50
FEATURE [Part::Cylinder] Cylinder369
  Angle = 360
  AttacherType = Attacher::AttachEngine3D
  Height = 30
  Placement = pos=(98,177,-30) rot=(0.799251,-0.424969,0.424969;1.79303rad)
  Radius = 48
FEATURE [Part::MultiFuse] Fusion349
  Refine = true
  Shapes = -> [Box634,Cylinder367]
FEATURE [Part::Box] Box635  label="Cube860"
  AttacherType = Attacher::AttachEngine3D
  Height = 7
  Length = 10
  Placement = pos=(48,147,-30) rot=(0,0,1;0rad)
  Width = 28
FEATURE [Part::Cut] Cut569  label="Cut861"
  Base = -> Fusion349
  Refine = true
  Tool = -> Cylinder368
FEATURE [Part::Cut] Cut570  label="Cut862"
  Base = -> Cut569
  Refine = true
  Tool = -> Cylinder369
FEATURE [Part::Cut] Cut571  label="Cut863"
  Base = -> Cut570
  Refine = true
  Tool = -> Box635
FEATURE [Part::Box] Box636  label="Cube861"
  AttacherType = Attacher::AttachEngine3D
  Height = 7
  Length = 45
  Placement = pos=(76,175,14) rot=(0,0,1;0rad)
  Width = 2
FEATURE [Part::MultiFuse] Fusion350
  Refine = true
  Shapes = -> [Cut571,Box636]
FEATURE [Part::Box] Box637  label="Cube862"
  AttacherType = Attacher::AttachEngine3D
  Height = 14
  Length = 10
  Placement = pos=(116,168,12) rot=(0,1,0;0.401426rad)
  Width = 9
FEATURE [Part::Cut] Cut572  label="Cut864"
  Base = -> Fusion350
  Refine = true
  Tool = -> Box637
FEATURE [Part::Box] Box638  label="Cube863"
  AttacherType = Attacher::AttachEngine3D
  Height = 10
  Length = 10
  Placement = pos=(46,152,-31) rot=(0,1,0;0.785398rad)
  Width = 25
FEATURE [Part::Box] Box639  label="Cube864"
  AttacherType = Attacher::AttachEngine3D
  Height = 4
  Length = 10
  Placement = pos=(100,-19,13) rot=(0,0,1;0.139626rad)
  Width = 4
FEATURE [Part::Box] Box640  label="Cube865"
  AttacherType = Attacher::AttachEngine3D
  Height = 4
  Length = 10
  Placement = pos=(100,-19,13) rot=(0,0,1;0.139626rad)
  Width = 4
FEATURE [Part::Mirroring] Part__Mirroring074  label="Cube432 (Mirror #9)003"
  Base = (0,0,0)
  Normal = (1,0,0)
  Placement = pos=(200,0,0) rot=(0,0,1;0rad)
  Source = -> Box640
FEATURE [Part::Box] Box641  label="Cube866"
  AttacherType = Attacher::AttachEngine3D
  Height = 3
  Length = 8
  Placement = pos=(96,-15,13) rot=(0,0,1;0rad)
  Width = 2
FEATURE [Part::MultiFuse] Fusion351
  Refine = true
  Shapes = -> [Part__Mirroring074,Box639]
FEATURE [Part::Cut] Cut573  label="Cut865"
  Base = -> Box641
  Refine = true
  Tool = -> Fusion351
FEATURE [Part::Fillet] Fillet465
  Base = -> Cut573
  Edges = 3 edges r=0.5: [Edge4,Edge14,Edge15]
FEATURE [Part::Fillet] Fillet464
  Base = -> Fillet465
  Edges = 4 edges r=0.5: [Edge7,Edge11,Edge16,Edge20]
  Placement = pos=(-2,6,2) rot=(0,0,1;0rad)
FEATURE [Part::Mirroring] Part__Mirroring075  label="wing-right-turning-light-TRASPARENT"
  Base = (0,0,0)
  Normal = (0,1,0)
  Placement = pos=(0,170,-0.5) rot=(0,0,1;0rad)
  Source = -> Fillet464
FEATURE [Part::Cut] Cut575  label="Cut867"
  Base = -> Box629
  Refine = true
  Tool = -> Cylinder364
FEATURE [Part::Cut] Cut576  label="Cut868"
  Base = -> Cut575
  Refine = true
  Tool = -> Cut568
FEATURE [Part::Box] Box642  label="Cube867"
  AttacherType = Attacher::AttachEngine3D
  Height = 20
  Length = 33
  Placement = pos=(15,156,-31) rot=(0,0,1;0rad)
  Width = 14
FEATURE [Part::Cylinder] Cylinder370
  Angle = 360
  AttacherType = Attacher::AttachEngine3D
  Height = 22
  Placement = pos=(98,174,-23) rot=(1,0,0;1.5708rad)
  Radius = 52
FEATURE [Part::Box] Box643  label="Cube868"
  AttacherType = Attacher::AttachEngine3D
  Height = 9
  Length = 5
  Placement = pos=(46,152,-32) rot=(0,0,1;0rad)
  Width = 22
FEATURE [Part::MultiFuse] Fusion353
  Refine = true
  Shapes = -> [Cylinder370,Box643]
FEATURE [Part::Cut] Cut577  label="Cut869"
  Base = -> Box642
  Refine = true
  Tool = -> Fusion353
FEATURE [Part::MultiFuse] Fusion354
  Refine = true
  Shapes = -> [Cylinder365,Box631]
FEATURE [Part::Cut] Cut578  label="Cut870"
  Base = -> Box630
  Refine = true
  Tool = -> Fusion354
FEATURE [Part::Cut] Cut579  label="Cut871"
  Base = -> Cut577
  Refine = true
  Tool = -> Cut578
FEATURE [Part::Box] Box644  label="Cube869"
  AttacherType = Attacher::AttachEngine3D
  Height = 2
  Length = 33
  Placement = pos=(15,156,-31) rot=(0,0,1;0rad)
  Width = 14
FEATURE [Part::Box] Box645  label="Cube870"
  AttacherType = Attacher::AttachEngine3D
  Height = 20
  Length = 33
  Placement = pos=(15,169,-29) rot=(0,0,1;0rad)
  Width = 3
FEATURE [Part::Cut] Cut580  label="Cut872"
  Base = -> Box645
  Refine = true
  Tool = -> Box644
FEATURE [Part::Cut] Cut581  label="Cut873"
  Base = -> Cut579
  Refine = true
  Tool = -> Cut580
FEATURE [Part::Box] Box646  label="Cube871"
  AttacherType = Attacher::AttachEngine3D
  Height = 12
  Length = 28
  Placement = pos=(17,165,-24) rot=(-1,0,0;0.279253rad)
  Width = 3
FEATURE [Part::Cylinder] Cylinder371
  Angle = 360
  AttacherType = Attacher::AttachEngine3D
  Height = 22
  Placement = pos=(98,174,-23) rot=(1,0,0;1.5708rad)
  Radius = 54
FEATURE [Part::Box] Box647  label="Cube872"
  AttacherType = Attacher::AttachEngine3D
  Height = 9
  Length = 5
  Placement = pos=(44,152,-32) rot=(0,0,1;0rad)
  Width = 22
FEATURE [Part::MultiFuse] Fusion355
  Refine = true
  Shapes = -> [Cylinder371,Box647]
FEATURE [Part::Cut] Cut582  label="Cut874"
  Base = -> Box646
  Placement = pos=(0,1,0) rot=(0,0,1;0rad)
  Refine = true
  Tool = -> Fusion355
FEATURE [Part::Cut] Cut583  label="Cut875"
  Base = -> Cut581
  Refine = true
  Tool = -> Cut582
FEATURE [Part::Fillet] Fillet467  label="wing-right-step"
  Base = -> Cut583
  Edges = 2 edges r=1: [Edge4,Edge32]
FEATURE [Part::Cylinder] Cylinder372
  Angle = 360
  AttacherType = Attacher::AttachEngine3D
  Height = 10
  Placement = pos=(18,15,-5) rot=(0,0,1;0rad)
  Radius = 0.9
FEATURE [Part::Cylinder] Cylinder373
  Angle = 360
  AttacherType = Attacher::AttachEngine3D
  Height = 10
  Placement = pos=(49,15,-5) rot=(0,0,1;0rad)
  Radius = 0.9
FEATURE [Part::MultiFuse] Fusion356
  Refine = true
  Shapes = -> [Cylinder372,Cylinder373]
FEATURE [Part::Mirroring] Part__Mirroring076  label="Fusion211 (Mirror #27)001"
  Base = (0,0,0)
  Normal = (0,1,0)
  Placement = pos=(0,170,0) rot=(0,0,1;0rad)
  Source = -> Fusion356
FEATURE [Part::Cut] Cut584  label="Cut876"
  Base = -> Cut576
  Refine = true
  Tool = -> Box633
FEATURE [Part::Box] Box648  label="Cube873"
  AttacherType = Attacher::AttachEngine3D
  Height = 9
  Length = 31
  Placement = pos=(17,156,-29) rot=(0,0,1;0rad)
  Width = 14
FEATURE [Part::Cylinder] Cylinder251
  Angle = 360
  AttacherType = Attacher::AttachEngine3D
  Height = 22
  Placement = pos=(98,174,-23) rot=(1,0,0;1.5708rad)
  Radius = 54
FEATURE [Part::Box] Box649  label="Cube874"
  AttacherType = Attacher::AttachEngine3D
  Height = 7.5
  Length = 4
  Placement = pos=(44,152,-31) rot=(0,0,1;0rad)
  Width = 22
FEATURE [Part::Box] Box650  label="Cube875"
  AttacherType = Attacher::AttachEngine3D
  Height = 20
  Length = 33
  Placement = pos=(15,156,-31) rot=(0,0,1;0rad)
  Width = 14
FEATURE [Part::Cylinder] Cylinder252
  Angle = 360
  AttacherType = Attacher::AttachEngine3D
  Height = 22
  Placement = pos=(98,174,-23) rot=(1,0,0;1.5708rad)
  Radius = 52
FEATURE [Part::Box] Box651  label="Cube876"
  AttacherType = Attacher::AttachEngine3D
  Height = 9
  Length = 5
  Placement = pos=(46,152,-32) rot=(0,0,1;0rad)
  Width = 22
FEATURE [Part::MultiFuse] Fusion212
  Refine = true
  Shapes = -> [Cylinder252,Box651]
FEATURE [Part::Cut] Cut585  label="Cut877"
  Base = -> Box650
  Refine = true
  Tool = -> Fusion212
FEATURE [Part::MultiFuse] Fusion213
  Refine = true
  Shapes = -> [Cylinder251,Box649]
FEATURE [Part::Cut] Cut586  label="Cut878"
  Base = -> Box648
  Refine = true
  Tool = -> Fusion213
FEATURE [Part::Cut] Cut587  label="Cut879"
  Base = -> Cut585
  Refine = true
  Tool = -> Cut586
FEATURE [Part::Box] Box652  label="Cube877"
  AttacherType = Attacher::AttachEngine3D
  Height = 2
  Length = 33
  Placement = pos=(15,156,-31) rot=(0,0,1;0rad)
  Width = 14
FEATURE [Part::Box] Box653  label="Cube878"
  AttacherType = Attacher::AttachEngine3D
  Height = 20
  Length = 33
  Placement = pos=(15,169,-29) rot=(0,0,1;0rad)
  Width = 3
FEATURE [Part::Cut] Cut588  label="Cut880"
  Base = -> Box653
  Refine = true
  Tool = -> Box652
FEATURE [Part::Cut] Cut589  label="Cut881"
  Base = -> Cut587
  Refine = true
  Tool = -> Cut588
FEATURE [Part::Box] Box654  label="Cube879"
  AttacherType = Attacher::AttachEngine3D
  Height = 12
  Length = 28
  Placement = pos=(17,165,-24) rot=(-1,0,0;0.279253rad)
  Width = 3
FEATURE [Part::Cylinder] Cylinder253
  Angle = 360
  AttacherType = Attacher::AttachEngine3D
  Height = 22
  Placement = pos=(98,174,-23) rot=(1,0,0;1.5708rad)
  Radius = 54
FEATURE [Part::Box] Box258  label="Cube484"
  AttacherType = Attacher::AttachEngine3D
  Height = 9
  Length = 5
  Placement = pos=(44,152,-32) rot=(0,0,1;0rad)
  Width = 22
FEATURE [Part::MultiFuse] Fusion214
  Refine = true
  Shapes = -> [Cylinder253,Box258]
FEATURE [Part::Cut] Cut590  label="Cut882"
  Base = -> Box654
  Placement = pos=(0,1,0) rot=(0,0,1;0rad)
  Refine = true
  Tool = -> Fusion214
FEATURE [Part::Cut] Cut591  label="Cut883"
  Base = -> Cut589
  Refine = true
  Tool = -> Cut590
FEATURE [Part::Fillet] Fillet136
  Base = -> Cut591
  Edges = 2 edges r=1: [Edge4,Edge32]
FEATURE [Part::Cut] Cut592  label="Cut884"
  Base = -> Cut584
  Refine = true
  Tool = -> Fillet136
FEATURE [Part::Cut] Cut593  label="wing-right-chassis"
  Base = -> Cut592
  Refine = true
  Tool = -> Part__Mirroring076
FEATURE [Part::Box] Box259  label="Cube485"
  AttacherType = Attacher::AttachEngine3D
  Height = 5.8
  Length = 13.6
  Placement = pos=(91.2,163,27) rot=(0,0,1;0rad)
  Width = 4
FEATURE [Part::Box] Box260  label="Cube486"
  AttacherType = Attacher::AttachEngine3D
  Height = 23
  Length = 37
  Placement = pos=(15,152,-23) rot=(0,0,1;0rad)
  Width = 18
FEATURE [Part::Cylinder] Cylinder254
  Angle = 360
  AttacherType = Attacher::AttachEngine3D
  Height = 22
  Placement = pos=(98,174,-23) rot=(1,0,0;1.5708rad)
  Radius = 52
FEATURE [Part::Box] Box261  label="Cube487"
  AttacherType = Attacher::AttachEngine3D
  Height = 9
  Length = 31
  Placement = pos=(17,156,-29) rot=(0,0,1;0rad)
  Width = 14
FEATURE [Part::Cylinder] Cylinder255
  Angle = 360
  AttacherType = Attacher::AttachEngine3D
  Height = 22
  Placement = pos=(98,174,-23) rot=(1,0,0;1.5708rad)
  Radius = 54
FEATURE [Part::Box] Box262  label="Cube488"
  AttacherType = Attacher::AttachEngine3D
  Height = 7.5
  Length = 4
  Placement = pos=(44,152,-31) rot=(0,0,1;0rad)
  Width = 22
FEATURE [Part::Box] Box263  label="Cube489"
  AttacherType = Attacher::AttachEngine3D
  Height = 18
  Length = 31
  Placement = pos=(17,158,-20) rot=(0,0,1;0rad)
  Width = 12
FEATURE [Part::Cylinder] Cylinder256
  Angle = 360
  AttacherType = Attacher::AttachEngine3D
  Height = 22
  Placement = pos=(98,174,-23) rot=(1,0,0;1.5708rad)
  Radius = 54
FEATURE [Part::Cut] Cut594  label="Cut885"
  Base = -> Box263
  Refine = true
  Tool = -> Cylinder256
FEATURE [Part::Box] Box264  label="Cube490"
  AttacherType = Attacher::AttachEngine3D
  Height = 21
  Length = 38
  Placement = pos=(15,167,-23) rot=(0,0,1;0rad)
  Width = 3
FEATURE [Part::Box] Box265  label="Cube491"
  AttacherType = Attacher::AttachEngine3D
  Height = 7
  Length = 10
  Placement = pos=(46,152,-30) rot=(0,0,1;0rad)
  Width = 25
FEATURE [Part::Cylinder] Cylinder257
  Angle = 360
  AttacherType = Attacher::AttachEngine3D
  Height = 25
  Placement = pos=(98,177,-23) rot=(0.799251,-0.424969,0.424969;1.79303rad)
  Radius = 52
FEATURE [Part::Cylinder] Cylinder258
  Angle = 360
  AttacherType = Attacher::AttachEngine3D
  Height = 28
  Placement = pos=(98,175,-23) rot=(0.799251,-0.424969,0.424969;1.79303rad)
  Radius = 50
FEATURE [Part::Cylinder] Cylinder259
  Angle = 360
  AttacherType = Attacher::AttachEngine3D
  Height = 30
  Placement = pos=(98,177,-30) rot=(0.799251,-0.424969,0.424969;1.79303rad)
  Radius = 48
FEATURE [Part::MultiFuse] Fusion215
  Refine = true
  Shapes = -> [Box265,Cylinder257]
FEATURE [Part::Box] Box266  label="Cube492"
  AttacherType = Attacher::AttachEngine3D
  Height = 7
  Length = 10
  Placement = pos=(48,147,-30) rot=(0,0,1;0rad)
  Width = 28
FEATURE [Part::Cut] Cut595  label="Cut886"
  Base = -> Fusion215
  Refine = true
  Tool = -> Cylinder258
FEATURE [Part::Cut] Cut596  label="Cut887"
  Base = -> Cut595
  Refine = true
  Tool = -> Cylinder259
FEATURE [Part::Cut] Cut597  label="Cut888"
  Base = -> Cut596
  Refine = true
  Tool = -> Box266
FEATURE [Part::Box] Box267  label="Cube493"
  AttacherType = Attacher::AttachEngine3D
  Height = 7
  Length = 45
  Placement = pos=(76,175,14) rot=(0,0,1;0rad)
  Width = 2
FEATURE [Part::MultiFuse] Fusion216
  Refine = true
  Shapes = -> [Cut597,Box267]
FEATURE [Part::Box] Box268  label="Cube494"
  AttacherType = Attacher::AttachEngine3D
  Height = 14
  Length = 10
  Placement = pos=(116,168,12) rot=(0,1,0;0.401426rad)
  Width = 9
FEATURE [Part::Cut] Cut313
  Base = -> Fusion216
  Refine = true
  Tool = -> Box268
FEATURE [Part::Box] Box269  label="Cube495"
  AttacherType = Attacher::AttachEngine3D
  Height = 10
  Length = 10
  Placement = pos=(46,152,-31) rot=(0,1,0;0.785398rad)
  Width = 25
FEATURE [Part::Box] Box270  label="Cube496"
  AttacherType = Attacher::AttachEngine3D
  Height = 4
  Length = 10
  Placement = pos=(100,-19,13) rot=(0,0,1;0.139626rad)
  Width = 4
FEATURE [Part::Box] Box271  label="Cube497"
  AttacherType = Attacher::AttachEngine3D
  Height = 4
  Length = 10
  Placement = pos=(100,-19,13) rot=(0,0,1;0.139626rad)
  Width = 4
FEATURE [Part::Mirroring] Part__Mirroring035  label="Cube432 (Mirror #9)004"
  Base = (0,0,0)
  Normal = (1,0,0)
  Placement = pos=(200,0,0) rot=(0,0,1;0rad)
  Source = -> Box271
FEATURE [Part::Box] Box272  label="Cube498"
  AttacherType = Attacher::AttachEngine3D
  Height = 3
  Length = 8
  Placement = pos=(96,-15,13) rot=(0,0,1;0rad)
  Width = 2
FEATURE [Part::MultiFuse] Fusion217
  Refine = true
  Shapes = -> [Part__Mirroring035,Box270]
FEATURE [Part::Cut] Cut314  label="Cut889"
  Base = -> Box272
  Refine = true
  Tool = -> Fusion217
FEATURE [Part::Fillet] Fillet138
  Base = -> Cut314
  Edges = 3 edges r=0.5: [Edge4,Edge14,Edge15]
FEATURE [Part::Fillet] Fillet137  label="wing-left-turning-light-TRASPARENT"
  Base = -> Fillet138
  Edges = 4 edges r=0.5: [Edge7,Edge11,Edge16,Edge20]
  Placement = pos=(-2,6,1.5) rot=(0,0,1;0rad)
FEATURE [Part::Cut] Cut316  label="Cut891"
  Base = -> Box260
  Refine = true
  Tool = -> Cylinder254
FEATURE [Part::Cut] Cut317  label="Cut892"
  Base = -> Cut316
  Refine = true
  Tool = -> Cut594
FEATURE [Part::Box] Box273  label="Cube499"
  AttacherType = Attacher::AttachEngine3D
  Height = 20
  Length = 33
  Placement = pos=(15,156,-31) rot=(0,0,1;0rad)
  Width = 14
FEATURE [Part::Cylinder] Cylinder260
  Angle = 360
  AttacherType = Attacher::AttachEngine3D
  Height = 22
  Placement = pos=(98,174,-23) rot=(1,0,0;1.5708rad)
  Radius = 52
FEATURE [Part::Box] Box274  label="Cube500"
  AttacherType = Attacher::AttachEngine3D
  Height = 9
  Length = 5
  Placement = pos=(46,152,-32) rot=(0,0,1;0rad)
  Width = 22
FEATURE [Part::MultiFuse] Fusion219
  Refine = true
  Shapes = -> [Cylinder260,Box274]
FEATURE [Part::Cut] Cut318  label="Cut893"
  Base = -> Box273
  Refine = true
  Tool = -> Fusion219
FEATURE [Part::MultiFuse] Fusion220
  Refine = true
  Shapes = -> [Cylinder255,Box262]
FEATURE [Part::Cut] Cut319  label="Cut894"
  Base = -> Box261
  Refine = true
  Tool = -> Fusion220
FEATURE [Part::Cut] Cut320  label="Cut895"
  Base = -> Cut318
  Refine = true
  Tool = -> Cut319
FEATURE [Part::Box] Box275  label="Cube501"
  AttacherType = Attacher::AttachEngine3D
  Height = 2
  Length = 33
  Placement = pos=(15,156,-31) rot=(0,0,1;0rad)
  Width = 14
FEATURE [Part::Box] Box276  label="Cube502"
  AttacherType = Attacher::AttachEngine3D
  Height = 20
  Length = 33
  Placement = pos=(15,169,-29) rot=(0,0,1;0rad)
  Width = 3
FEATURE [Part::Cut] Cut321  label="Cut896"
  Base = -> Box276
  Refine = true
  Tool = -> Box275
FEATURE [Part::Cut] Cut322  label="Cut897"
  Base = -> Cut320
  Refine = true
  Tool = -> Cut321
FEATURE [Part::Box] Box277  label="Cube503"
  AttacherType = Attacher::AttachEngine3D
  Height = 12
  Length = 28
  Placement = pos=(17,165,-24) rot=(-1,0,0;0.279253rad)
  Width = 3
FEATURE [Part::Cylinder] Cylinder261
  Angle = 360
  AttacherType = Attacher::AttachEngine3D
  Height = 22
  Placement = pos=(98,174,-23) rot=(1,0,0;1.5708rad)
  Radius = 54
FEATURE [Part::Box] Box655  label="Cube880"
  AttacherType = Attacher::AttachEngine3D
  Height = 9
  Length = 5
  Placement = pos=(44,152,-32) rot=(0,0,1;0rad)
  Width = 22
FEATURE [Part::MultiFuse] Fusion221
  Refine = true
  Shapes = -> [Cylinder261,Box655]
FEATURE [Part::Cut] Cut598  label="Cut898"
  Base = -> Box277
  Placement = pos=(0,1,0) rot=(0,0,1;0rad)
  Refine = true
  Tool = -> Fusion221
FEATURE [Part::Cut] Cut599  label="Cut899"
  Base = -> Cut322
  Refine = true
  Tool = -> Cut598
FEATURE [Part::Fillet] Fillet140
  Base = -> Cut599
  Edges = 2 edges r=1: [Edge4,Edge32]
FEATURE [Part::Cylinder] Cylinder262
  Angle = 360
  AttacherType = Attacher::AttachEngine3D
  Height = 10
  Placement = pos=(18,15,-5) rot=(0,0,1;0rad)
  Radius = 0.9
FEATURE [Part::Cylinder] Cylinder263
  Angle = 360
  AttacherType = Attacher::AttachEngine3D
  Height = 10
  Placement = pos=(49,15,-5) rot=(0,0,1;0rad)
  Radius = 0.9
FEATURE [Part::MultiFuse] Fusion222
  Refine = true
  Shapes = -> [Cylinder262,Cylinder263]
FEATURE [Part::Mirroring] Part__Mirroring078  label="Fusion211 (Mirror #27)002"
  Base = (0,0,0)
  Normal = (0,1,0)
  Placement = pos=(0,170,0) rot=(0,0,1;0rad)
  Source = -> Fusion222
FEATURE [Part::Cut] Cut325  label="Cut900"
  Base = -> Cut317
  Refine = true
  Tool = -> Box264
FEATURE [Part::Box] Box656  label="Cube881"
  AttacherType = Attacher::AttachEngine3D
  Height = 9
  Length = 31
  Placement = pos=(17,156,-29) rot=(0,0,1;0rad)
  Width = 14
FEATURE [Part::Cylinder] Cylinder264
  Angle = 360
  AttacherType = Attacher::AttachEngine3D
  Height = 22
  Placement = pos=(98,174,-23) rot=(1,0,0;1.5708rad)
  Radius = 54
FEATURE [Part::Box] Box657  label="Cube882"
  AttacherType = Attacher::AttachEngine3D
  Height = 7.5
  Length = 4
  Placement = pos=(44,152,-31) rot=(0,0,1;0rad)
  Width = 22
FEATURE [Part::Box] Box658  label="Cube883"
  AttacherType = Attacher::AttachEngine3D
  Height = 20
  Length = 33
  Placement = pos=(15,156,-31) rot=(0,0,1;0rad)
  Width = 14
FEATURE [Part::Cylinder] Cylinder265
  Angle = 360
  AttacherType = Attacher::AttachEngine3D
  Height = 22
  Placement = pos=(98,174,-23) rot=(1,0,0;1.5708rad)
  Radius = 52
FEATURE [Part::Box] Box659  label="Cube884"
  AttacherType = Attacher::AttachEngine3D
  Height = 9
  Length = 5
  Placement = pos=(46,152,-32) rot=(0,0,1;0rad)
  Width = 22
FEATURE [Part::MultiFuse] Fusion223
  Refine = true
  Shapes = -> [Cylinder265,Box659]
FEATURE [Part::Cut] Cut326  label="Cut901"
  Base = -> Box658
  Refine = true
  Tool = -> Fusion223
FEATURE [Part::MultiFuse] Fusion224
  Refine = true
  Shapes = -> [Cylinder264,Box657]
FEATURE [Part::Cut] Cut327  label="Cut902"
  Base = -> Box656
  Refine = true
  Tool = -> Fusion224
FEATURE [Part::Cut] Cut328  label="Cut903"
  Base = -> Cut326
  Refine = true
  Tool = -> Cut327
FEATURE [Part::Box] Box660  label="Cube885"
  AttacherType = Attacher::AttachEngine3D
  Height = 2
  Length = 33
  Placement = pos=(15,156,-31) rot=(0,0,1;0rad)
  Width = 14
FEATURE [Part::Box] Box661  label="Cube886"
  AttacherType = Attacher::AttachEngine3D
  Height = 20
  Length = 33
  Placement = pos=(15,169,-29) rot=(0,0,1;0rad)
  Width = 3
FEATURE [Part::Cut] Cut329  label="Cut904"
  Base = -> Box661
  Refine = true
  Tool = -> Box660
FEATURE [Part::Cut] Cut330  label="Cut905"
  Base = -> Cut328
  Refine = true
  Tool = -> Cut329
FEATURE [Part::Box] Box662  label="Cube887"
  AttacherType = Attacher::AttachEngine3D
  Height = 12
  Length = 28
  Placement = pos=(17,165,-24) rot=(-1,0,0;0.279253rad)
  Width = 3
FEATURE [Part::Cylinder] Cylinder266
  Angle = 360
  AttacherType = Attacher::AttachEngine3D
  Height = 22
  Placement = pos=(98,174,-23) rot=(1,0,0;1.5708rad)
  Radius = 54
FEATURE [Part::Box] Box286  label="Cube512"
  AttacherType = Attacher::AttachEngine3D
  Height = 9
  Length = 5
  Placement = pos=(44,152,-32) rot=(0,0,1;0rad)
  Width = 22
FEATURE [Part::MultiFuse] Fusion225
  Refine = true
  Shapes = -> [Cylinder266,Box286]
FEATURE [Part::Cut] Cut331  label="Cut906"
  Base = -> Box662
  Placement = pos=(0,1,0) rot=(0,0,1;0rad)
  Refine = true
  Tool = -> Fusion225
FEATURE [Part::Cut] Cut332  label="Cut907"
  Base = -> Cut330
  Refine = true
  Tool = -> Cut331
FEATURE [Part::Fillet] Fillet141
  Base = -> Cut332
  Edges = 2 edges r=1: [Edge4,Edge32]
FEATURE [Part::Cut] Cut333
  Base = -> Cut325
  Refine = true
  Tool = -> Fillet141
FEATURE [Part::Cut] Cut600  label="Cut908"
  Base = -> Cut333
  Refine = true
  Tool = -> Part__Mirroring078
FEATURE [Part::Mirroring] Part__Mirroring080  label="wing-left-step"
  Base = (0,0,0)
  Normal = (0,1,0)
  Placement = pos=(0,170,0) rot=(0,0,1;0rad)
  Source = -> Fillet140
FEATURE [Part::Mirroring] Part__Mirroring081  label="wing-left-chassis"
  Base = (0,0,0)
  Normal = (0,1,0)
  Placement = pos=(0,170,0) rot=(0,0,1;0rad)
  Source = -> Cut600
FEATURE [Part::MultiFuse] Fusion357
  Refine = true
  Shapes = -> [Box628,Cut572]
FEATURE [Part::Cut] Cut601  label="Cut909"
  Base = -> Fusion357
  Refine = true
  Tool = -> Box638
FEATURE [Part::Fillet] Fillet468  label="wing-right_"
  Base = -> Cut601
  Edges = 1 edges r=1: [Edge14]
FEATURE [Part::MultiFuse] Fusion358
  Refine = true
  Shapes = -> [Box259,Cut313]
FEATURE [Part::Cut] Cut602  label="Cut910"
  Base = -> Fusion358
  Refine = true
  Tool = -> Box269
FEATURE [Part::Fillet] Fillet469
  Base = -> Cut602
  Edges = 1 edges r=1: [Edge14]
FEATURE [Part::Mirroring] Part__Mirroring082  label="wing-left_"
  Base = (0,0,0)
  Normal = (0,1,0)
  Placement = pos=(0,170,0) rot=(0,0,1;0rad)
  Source = -> Fillet469
FEATURE [Part::Box] Box663  label="Cube888"
  AttacherType = Attacher::AttachEngine3D
  Height = 14
  Length = 10
  Placement = pos=(116,169,12) rot=(0,1,0;0.401426rad)
  Width = 9
FEATURE [Part::Box] Box664  label="Cube889"
  AttacherType = Attacher::AttachEngine3D
  Height = 12
  Length = 11
  Placement = pos=(46,153,-31) rot=(0,1,0;0.785398rad)
  Width = 25
FEATURE [Part::Cylinder] Cylinder377
  Angle = 124
  AttacherType = Attacher::AttachEngine3D
  Height = 1
  Placement = pos=(98,177,-30) rot=(0,0.707107,0.707107;3.14159rad)
  Radius = 49
FEATURE [Part::Cylinder] Cylinder378
  Angle = 360
  AttacherType = Attacher::AttachEngine3D
  Height = 1
  Placement = pos=(98,177,-30) rot=(-1,0,0;1.5708rad)
  Radius = 48
FEATURE [Part::MultiFuse] Fusion359
  Refine = true
  Shapes = -> [Box664,Box663]
FEATURE [Part::Cut] Cut603  label="Cut911"
  Base = -> Cylinder377
  Refine = true
  Tool = -> Cylinder378
FEATURE [Part::Cut] Cut604  label="Cut912"
  Base = -> Cut603
  Refine = true
  Tool = -> Fusion359
FEATURE [Part::Fillet] Fillet470
  Base = -> Cut604
  Edges = 2 edges r=0.499: [Edge1,Edge6]
  Placement = pos=(0,-0.5,0) rot=(0,0,1;0rad)
FEATURE [Part::Box] Box665  label="Cube890"
  AttacherType = Attacher::AttachEngine3D
  Height = 14
  Length = 10
  Placement = pos=(116,169,12) rot=(0,1,0;0.401426rad)
  Width = 9
FEATURE [Part::Box] Box666  label="Cube891"
  AttacherType = Attacher::AttachEngine3D
  Height = 12
  Length = 11
  Placement = pos=(46,153,-31) rot=(0,1,0;0.785398rad)
  Width = 25
FEATURE [Part::Cylinder] Cylinder379
  Angle = 124
  AttacherType = Attacher::AttachEngine3D
  Height = 1
  Placement = pos=(98,177,-30) rot=(0,0.707107,0.707107;3.14159rad)
  Radius = 49
FEATURE [Part::Cylinder] Cylinder380
  Angle = 360
  AttacherType = Attacher::AttachEngine3D
  Height = 1
  Placement = pos=(98,177,-30) rot=(-1,0,0;1.5708rad)
  Radius = 48
FEATURE [Part::MultiFuse] Fusion360
  Refine = true
  Shapes = -> [Box666,Box665]
FEATURE [Part::Cut] Cut605  label="Cut915"
  Base = -> Cylinder379
  Refine = true
  Tool = -> Cylinder380
FEATURE [Part::Cut] Cut606  label="Cut916"
  Base = -> Cut605
  Refine = true
  Tool = -> Fusion360
FEATURE [Part::Fillet] Fillet471
  Base = -> Cut606
  Edges = 2 edges r=0.499: [Edge1,Edge6]
  Placement = pos=(0,-0.5,0) rot=(0,0,1;0rad)
FEATURE [Part::Mirroring] Part__Mirroring083  label="Fillet471 (Mirror #65)"
  Base = (0,0,0)
  Normal = (0,1,0)
  Placement = pos=(0,170,0) rot=(0,0,1;0rad)
  Source = -> Fillet471
FEATURE [Part::MultiFuse] Fusion361  label="wing-right"
  Refine = true
  Shapes = -> [Fillet468,Fillet470]
FEATURE [Part::MultiFuse] Fusion362  label="wing-left"
  Refine = true
  Shapes = -> [Part__Mirroring082,Part__Mirroring083]
FEATURE [Part::Cylinder] Cylinder381
  Angle = 66.75
  AttacherType = Attacher::AttachEngine3D
  Height = 1
  Placement = pos=(99,178,-31) rot=(1,0,0;1.5708rad)
  Radius = 48
FEATURE [Part::Cylinder] Cylinder382
  Angle = 66.75
  AttacherType = Attacher::AttachEngine3D
  Height = 1
  Placement = pos=(99,178,-31) rot=(1,0,0;1.5708rad)
  Radius = 49
FEATURE [Part::Cut] Cut607  label="Cut917"
  Base = -> Cylinder382
  Refine = true
  Tool = -> Cylinder381
FEATURE [Part::Fillet] Fillet472
  Base = -> Cut607
  Edges = 2 edges r=0.499: [Edge3,Edge11]
  Placement = pos=(0,-0.5,0) rot=(0,0,1;0rad)
FEATURE [Part::Cylinder] Cylinder383
  Angle = 66.75
  AttacherType = Attacher::AttachEngine3D
  Height = 1
  Placement = pos=(99,178,-31) rot=(1,0,0;1.5708rad)
  Radius = 48
FEATURE [Part::Cylinder] Cylinder384
  Angle = 66.75
  AttacherType = Attacher::AttachEngine3D
  Height = 1
  Placement = pos=(99,178,-31) rot=(1,0,0;1.5708rad)
  Radius = 49
FEATURE [Part::Cut] Cut608  label="Cut918"
  Base = -> Cylinder384
  Refine = true
  Tool = -> Cylinder383
FEATURE [Part::Fillet] Fillet473
  Base = -> Cut608
  Edges = 2 edges r=0.499: [Edge3,Edge11]
  Placement = pos=(0,-0.5,0) rot=(0,0,1;0rad)
FEATURE [Part::Mirroring] Part__Mirroring084  label="Fillet473 (Mirror #66)"
  Base = (0,0,0)
  Normal = (0,1,0)
  Placement = pos=(0,170,0) rot=(0,0,1;0rad)
  Source = -> Fillet473
FEATURE [Part::MultiFuse] Fusion363  label="wing-right-rear"
  Refine = true
  Shapes = -> [Fusion138,Fillet472]
FEATURE [Part::MultiFuse] Fusion364  label="wing-left-rear"
  Refine = true
  Shapes = -> [Part__Mirroring018,Part__Mirroring084]
FEATURE [Part::Box] Box667  label="Cube"
  AttacherType = Attacher::AttachEngine3D
  Height = 32
  Length = 3
  Placement = pos=(0,-0.5,-1) rot=(0,0,1;0rad)
  Width = 16
FEATURE [Part::Cylinder] Cylinder385
  Angle = 360
  AttacherType = Attacher::AttachEngine3D
  Height = 1.5
  Placement = pos=(0,200.5,15) rot=(0,1,0;1.5708rad)
  Radius = 200
FEATURE [Part::Box] Box668  label="Cube002"
  AttacherType = Attacher::AttachEngine3D
  Height = 500
  Length = 1.5
  Placement = pos=(0,7.5,-229) rot=(0,0,1;0rad)
  Width = 450
FEATURE [Part::Box] Box669  label="Cube003"
  AttacherType = Attacher::AttachEngine3D
  Height = 43
  Length = 1.5
  Placement = pos=(0,0.5,30) rot=(0,0,1;0rad)
  Width = 13
FEATURE [Part::Box] Box004  label="Cube004"
  AttacherType = Attacher::AttachEngine3D
  Height = 43
  Length = 1.5
  Placement = pos=(0,0.5,-43) rot=(0,0,1;0rad)
  Width = 13
FEATURE [Part::Box] Box005  label="Cube005"
  AttacherType = Attacher::AttachEngine3D
  Height = 26
  Length = 6
  Placement = pos=(28,-20.5,78) rot=(0,0,1;0rad)
  Width = 15
FEATURE [Part::Cylinder] Cylinder002
  Angle = 360
  AttacherType = Attacher::AttachEngine3D
  Height = 10
  Placement = pos=(29.5,-13,86) rot=(0,0,1;0rad)
  Radius = 0.9
FEATURE [Part::MultiFuse] Fusion365
  Refine = true
  Shapes = -> [Box668,Box669,Box004]
FEATURE [Part::Cut] Cut609  label="Cut919"
  Base = -> Cylinder385
  Refine = true
  Tool = -> Fusion365
FEATURE [Part::MultiFuse] Fusion006
  Refine = true
  Shapes = -> [Box668,Box669,Box004]
FEATURE [Part::Cylinder] Cylinder007
  Angle = 360
  AttacherType = Attacher::AttachEngine3D
  Height = 1.5
  Placement = pos=(0,200.5,15) rot=(0,1,0;1.5708rad)
  Radius = 200
FEATURE [Part::Cut] Cut008
  Base = -> Cylinder007
  Refine = true
  Tool = -> Fusion006
FEATURE [Part::Mirroring] Part__Mirroring085  label="Cut (Mirror #1)"
  Base = (0,0,0)
  Normal = (0,1,0)
  Placement = pos=(0,15,0) rot=(0,0,1;0rad)
  Source = -> Cut609
FEATURE [Part::MultiFuse] Fusion366
  Refine = true
  Shapes = -> [Part__Mirroring085,Cut008]
FEATURE [Part::Cut] Cut009
  Base = -> Box667
  Placement = pos=(37,-5.5,76) rot=(0,0,1;3.14159rad)
  Refine = true
  Tool = -> Fusion366
FEATURE [Part::Fillet] Fillet474
  Base = -> Cut009
  Edges = 4 edges r=3: [Edge9,Edge11,Edge12,Edge14]
FEATURE [Part::Fillet] Fillet475
  Base = -> Fillet474
  Edges = 4 edges r=1.5: [Edge29,Edge31,Edge33,Edge34]
FEATURE [Part::Fillet] Fillet476
  Base = -> Fillet475
  Edges = 8 edges r=0.5: [Edge9,Edge12,Edge13,Edge16,Edge33,Edge41,Edge43,Edge48]
FEATURE [Part::Chamfer] Chamfer074
  Base = -> Box005
  Edges = 2 edges r=5.999: [Edge1,Edge3]
FEATURE [Part::Chamfer] Chamfer075
  Base = -> Chamfer074
  Edges = 2 edges: [Edge1 r1=9 r2=5.999,Edge4 r1=9 r2=5.999]
FEATURE [Part::Box] Box670  label="Cube892"
  AttacherType = Attacher::AttachEngine3D
  Height = 26
  Length = 6
  Placement = pos=(26,-14,78) rot=(0,0,1;0rad)
  Width = 2
FEATURE [Part::Fillet] Fillet477
  Base = -> Box670
  Edges = 2 edges r=0.899: [Edge5,Edge7]
  Placement = pos=(1,0,0) rot=(0,0,1;0rad)
FEATURE [Part::Box] Box671  label="Cube893"
  AttacherType = Attacher::AttachEngine3D
  Height = 8
  Length = 5
  Placement = pos=(28,-14,87) rot=(0,0,1;0rad)
  Width = 2
FEATURE [Part::Box] Box672  label="Cube894"
  AttacherType = Attacher::AttachEngine3D
  Height = 8
  Length = 1.5
  Placement = pos=(28,-13.8,87) rot=(0,0,1;0rad)
  Width = 1.6
FEATURE [Part::MultiFuse] Fusion367
  Refine = true
  Shapes = -> [Box672,Cylinder002]
FEATURE [Part::Cut] Cut614  label="Cut921"
  Base = -> Chamfer075
  Refine = true
  Tool = -> Fillet477
FEATURE [Part::Cut] Cut615  label="Cut922"
  Base = -> Box671
  Refine = true
  Tool = -> Fusion367
FEATURE [Part::Fillet] Fillet480
  Base = -> Cut614
  Edges = 4 edges r=5: [Edge2,Edge4,Edge10,Edge20]
FEATURE [Part::Fillet] Fillet481
  Base = -> Cut615
  Edges = 4 edges r=1.5: [Edge1,Edge3,Edge9,Edge18]
FEATURE [Part::MultiFuse] Fusion369
  Refine = true
  Shapes = -> [Fillet481,Fillet480]
FEATURE [Part::Fillet] Fillet483
  Base = -> Fusion369
  Edges = 4 edges r=1.1: [Edge60,Edge61,Edge72,Edge83]
FEATURE [Part::MultiFuse] Fusion370  label="cab-rearview"
  Refine = true
  Shapes = -> [Fillet476,Fillet483]
FEATURE [Part::Box] Box673  label="Cube895"
  AttacherType = Attacher::AttachEngine3D
  Height = 15
  Length = 5
  Placement = pos=(-2,14,-23.5) rot=(0,0,1;0rad)
  Width = 24
FEATURE [Part::Fillet] Fillet484
  Base = -> Box673
  Edges = 4 edges r=3: [Edge9,Edge10,Edge11,Edge12]
  Placement = pos=(2,128,-4.5) rot=(0,0,1;0rad)
FEATURE [Part::Cylinder] Cylinder386
  Angle = 360
  AttacherType = Attacher::AttachEngine3D
  Height = 10
  Placement = pos=(0,154,-20.5) rot=(0,1,0;1.5708rad)
  Radius = 2.5
FEATURE [Part::Box] Box674  label="Cube896"
  AttacherType = Attacher::AttachEngine3D
  Height = 14
  Length = 0.6
  Placement = pos=(-0.6,13.5,-23) rot=(0,0,1;0rad)
  Width = 23
FEATURE [Part::Fillet] Fillet485
  Base = -> Box674
  Edges = 4 edges r=3: [Edge9,Edge10,Edge11,Edge12]
  Placement = pos=(0,116,0) rot=(0,0,1;0rad)
FEATURE [Part::Fillet] Fillet486  label="front-lights-glass"
  Base = -> Fillet485
  Edges = 4 edges r=0.4: [Edge1,Edge4,Edge5,Edge8]
  Placement = pos=(2,13,-4.5) rot=(0,0,1;0rad)
FEATURE [Part::Feature] Face038
  shape: bbox 2.001e-07 x 5.53 x 5.85 mm, 1 faces, 0 solids (baked)
FEATURE [Part::Feature] Face039
  Placement = pos=(-0.31,0,0) rot=(0,0,1;0rad)
  shape: bbox 2e-07 x 26.4 x 16.5 mm, 1 faces, 0 solids (baked)
FEATURE [Part::Loft] Loft019
  Closed = false
  MaxDegree = 5
  Placement = pos=(-0.2,0,0) rot=(0,0,1;0rad)
  Ruled = false
  Sections = -> [Face038,Face039]
  Solid = true
FEATURE [Part::Cut] Cut616  label="Cut923"
  Base = -> Fillet484
  Refine = true
  Tool = -> Loft019
FEATURE [Part::Cut] Cut617  label="Cut924"
  Base = -> Cut616
  Placement = pos=(1,0,0) rot=(0,0,1;0rad)
  Refine = true
  Tool = -> Cylinder386
FEATURE [Part::Box] Box675  label="Cube897"
  AttacherType = Attacher::AttachEngine3D
  Height = 16.5
  Length = 5
  Placement = pos=(5,140,-28.75) rot=(0,0,1;0rad)
  Width = 27.75
FEATURE [Part::Cylinder] Cylinder387
  Angle = 360
  AttacherType = Attacher::AttachEngine3D
  Height = 10
  Placement = pos=(0,154,-20.5) rot=(0,1,0;1.5708rad)
  Radius = 2.5
FEATURE [Part::Fillet] Fillet487
  Base = -> Box675
  Edges = 2 edges r=1.5: [Edge11,Edge12]
FEATURE [Part::Box] Box677  label="Cube898"
  AttacherType = Attacher::AttachEngine3D
  Height = 1
  Length = 5
  Placement = pos=(5,143,-13) rot=(0,0,1;0rad)
  Width = 21.75
FEATURE [Part::Box] Box678  label="Cube899"
  AttacherType = Attacher::AttachEngine3D
  Height = 1
  Length = 5
  Placement = pos=(5,143,-29) rot=(0,0,1;0rad)
  Width = 21.75
FEATURE [Part::Box] Box679  label="Cube900"
  AttacherType = Attacher::AttachEngine3D
  Height = 12
  Length = 5
  Placement = pos=(5,166,-26.5) rot=(0,0,1;0rad)
  Width = 1.75
FEATURE [Part::Box] Box680  label="Cube901"
  AttacherType = Attacher::AttachEngine3D
  Height = 12
  Length = 5
  Placement = pos=(5,140,-26.5) rot=(0,0,1;0rad)
  Width = 2
FEATURE [Part::MultiFuse] Fusion371
  Refine = true
  Shapes = -> [Box680,Box678,Box677,Box679]
FEATURE [Part::Cut] Cut618  label="Cut925"
  Base = -> Fillet487
  Refine = true
  Tool = -> Fusion371
FEATURE [Part::Fillet] Fillet488
  Base = -> Cut618
  Edges = 4 edges r=0.75: [Edge38,Edge40,Edge60,Edge63]
FEATURE [Part::Fillet] Fillet489
  Base = -> Fillet488
  Edges = 4 edges r=0.7: [Edge41,Edge53,Edge55,Edge67]
FEATURE [Part::Fillet] Fillet490
  Base = -> Fillet489
  Edges = 4 edges r=0.9: [Edge41,Edge59,Edge60,Edge78]
FEATURE [Part::Fillet] Fillet491
  Base = -> Fillet490
  Edges = 2 edges r=1.2: [Edge62,Edge92]
FEATURE [Part::MultiFuse] Fusion372
  Refine = true
  Shapes = -> [Cut617,Fillet491]
FEATURE [Part::Cut] Cut619  label="front-light-holder-right"
  Base = -> Fusion372
  Refine = true
  Tool = -> Cylinder387
FEATURE [Part::Box] Box681  label="Cube902"
  AttacherType = Attacher::AttachEngine3D
  Height = 15
  Length = 5
  Placement = pos=(-2,14,-23.5) rot=(0,0,1;0rad)
  Width = 24
FEATURE [Part::Fillet] Fillet492
  Base = -> Box681
  Edges = 4 edges r=3: [Edge9,Edge10,Edge11,Edge12]
  Placement = pos=(2,128,-4.5) rot=(0,0,1;0rad)
FEATURE [Part::Cylinder] Cylinder388
  Angle = 360
  AttacherType = Attacher::AttachEngine3D
  Height = 10
  Placement = pos=(0,154,-20.5) rot=(0,1,0;1.5708rad)
  Radius = 2.5
FEATURE [Part::Feature] Face040
  shape: bbox 2.001e-07 x 5.53 x 5.85 mm, 1 faces, 0 solids (baked)
FEATURE [Part::Feature] Face041
  Placement = pos=(-0.31,0,0) rot=(0,0,1;0rad)
  shape: bbox 2e-07 x 26.4 x 16.5 mm, 1 faces, 0 solids (baked)
FEATURE [Part::Loft] Loft020
  Closed = false
  MaxDegree = 5
  Placement = pos=(-0.2,0,0) rot=(0,0,1;0rad)
  Ruled = false
  Sections = -> [Face040,Face041]
  Solid = true
FEATURE [Part::Cut] Cut620  label="Cut931"
  Base = -> Fillet492
  Refine = true
  Tool = -> Loft020
FEATURE [Part::Cut] Cut621  label="Cut932"
  Base = -> Cut620
  Placement = pos=(1,0,0) rot=(0,0,1;0rad)
  Refine = true
  Tool = -> Cylinder388
FEATURE [Part::Box] Box682  label="Cube903"
  AttacherType = Attacher::AttachEngine3D
  Height = 16.5
  Length = 5
  Placement = pos=(5,140,-28.75) rot=(0,0,1;0rad)
  Width = 27.75
FEATURE [Part::Cylinder] Cylinder389
  Angle = 360
  AttacherType = Attacher::AttachEngine3D
  Height = 10
  Placement = pos=(0,154,-20.5) rot=(0,1,0;1.5708rad)
  Radius = 2.5
FEATURE [Part::Fillet] Fillet493
  Base = -> Box682
  Edges = 2 edges r=1.5: [Edge11,Edge12]
FEATURE [Part::Box] Box683  label="Cube904"
  AttacherType = Attacher::AttachEngine3D
  Height = 1
  Length = 5
  Placement = pos=(5,143,-13) rot=(0,0,1;0rad)
  Width = 21.75
FEATURE [Part::Box] Box684  label="Cube905"
  AttacherType = Attacher::AttachEngine3D
  Height = 1
  Length = 5
  Placement = pos=(5,143,-29) rot=(0,0,1;0rad)
  Width = 21.75
FEATURE [Part::Box] Box685  label="Cube906"
  AttacherType = Attacher::AttachEngine3D
  Height = 12
  Length = 5
  Placement = pos=(5,166,-26.5) rot=(0,0,1;0rad)
  Width = 1.75
FEATURE [Part::Box] Box686  label="Cube907"
  AttacherType = Attacher::AttachEngine3D
  Height = 12
  Length = 5
  Placement = pos=(5,140,-26.5) rot=(0,0,1;0rad)
  Width = 2
FEATURE [Part::MultiFuse] Fusion373
  Refine = true
  Shapes = -> [Box686,Box684,Box683,Box685]
FEATURE [Part::Cut] Cut622  label="Cut933"
  Base = -> Fillet493
  Refine = true
  Tool = -> Fusion373
FEATURE [Part::Fillet] Fillet494
  Base = -> Cut622
  Edges = 4 edges r=0.75: [Edge38,Edge40,Edge60,Edge63]
FEATURE [Part::Fillet] Fillet495
  Base = -> Fillet494
  Edges = 4 edges r=0.7: [Edge41,Edge53,Edge55,Edge67]
FEATURE [Part::Fillet] Fillet496
  Base = -> Fillet495
  Edges = 4 edges r=0.9: [Edge41,Edge59,Edge60,Edge78]
FEATURE [Part::Fillet] Fillet497
  Base = -> Fillet496
  Edges = 2 edges r=1.2: [Edge62,Edge92]
FEATURE [Part::MultiFuse] Fusion374
  Refine = true
  Shapes = -> [Cut621,Fillet497]
FEATURE [Part::Cut] Cut623  label="Cut934"
  Base = -> Fusion374
  Refine = true
  Tool = -> Cylinder389
FEATURE [Part::Mirroring] Part__Mirroring086  label="front-light-holder-left"
  Base = (0,0,0)
  Normal = (0,1,0)
  Placement = pos=(0,170,0) rot=(0,0,1;0rad)
  Source = -> Cut623
FEATURE [Part::Box] Box687  label="Cube908"
  AttacherType = Attacher::AttachEngine3D
  Height = 5
  Length = 13.6
  Placement = pos=(91.2,3,32.8) rot=(0,0,1;0rad)
  Width = 4
FEATURE [Part::Cylinder] Cylinder390
  Angle = 360
  AttacherType = Attacher::AttachEngine3D
  Height = 10
  Placement = pos=(98,5,29) rot=(0,0,1;0rad)
  Radius = 1.2
FEATURE [Part::Cut] Cut624  label="Cut935"
  Base = -> Box687
  Refine = true
  Tool = -> Cylinder390
FEATURE [Part::Box] Box688  label="Cube909"
  AttacherType = Attacher::AttachEngine3D
  Height = 15
  Length = 6.6
  Placement = pos=(-2,14,-23.5) rot=(0,0,1;0rad)
  Width = 24
FEATURE [Part::Fillet] Fillet498
  Base = -> Box688
  Edges = 4 edges r=3: [Edge9,Edge10,Edge11,Edge12]
  Placement = pos=(2,128,-4.5) rot=(0,0,1;0rad)
FEATURE [Part::Cylinder] Cylinder391
  Angle = 360
  AttacherType = Attacher::AttachEngine3D
  Height = 10
  Placement = pos=(0,154,-20.5) rot=(0,1,0;1.5708rad)
  Radius = 2.5
FEATURE [Part::Feature] Face042
  shape: bbox 2.001e-07 x 5.53 x 5.85 mm, 1 faces, 0 solids (baked)
FEATURE [Part::Feature] Face043
  Placement = pos=(-0.31,0,0) rot=(0,0,1;0rad)
  shape: bbox 2e-07 x 26.4 x 16.5 mm, 1 faces, 0 solids (baked)
FEATURE [Part::Loft] Loft021
  Closed = false
  MaxDegree = 5
  Placement = pos=(0.4,0,0) rot=(0,0,1;0rad)
  Ruled = false
  Sections = -> [Face042,Face043]
  Solid = true
FEATURE [Part::Box] Box689  label="Cube910"
  AttacherType = Attacher::AttachEngine3D
  Height = 16.5
  Length = 5
  Placement = pos=(5,140,-28.75) rot=(0,0,1;0rad)
  Width = 27.75
FEATURE [Part::Fillet] Fillet499
  Base = -> Box689
  Edges = 2 edges r=1.5: [Edge11,Edge12]
FEATURE [Part::Box] Box690  label="Cube911"
  AttacherType = Attacher::AttachEngine3D
  Height = 1
  Length = 5
  Placement = pos=(5,143,-13) rot=(0,0,1;0rad)
  Width = 21.75
FEATURE [Part::Box] Box691  label="Cube912"
  AttacherType = Attacher::AttachEngine3D
  Height = 1
  Length = 5
  Placement = pos=(5,143,-29) rot=(0,0,1;0rad)
  Width = 21.75
FEATURE [Part::Box] Box692  label="Cube913"
  AttacherType = Attacher::AttachEngine3D
  Height = 12
  Length = 5
  Placement = pos=(5,166,-26.5) rot=(0,0,1;0rad)
  Width = 1.75
FEATURE [Part::Box] Box693  label="Cube914"
  AttacherType = Attacher::AttachEngine3D
  Height = 12
  Length = 5
  Placement = pos=(5,140,-26.5) rot=(0,0,1;0rad)
  Width = 2
FEATURE [Part::MultiFuse] Fusion375
  Refine = true
  Shapes = -> [Box693,Box691,Box690,Box692]
FEATURE [Part::Cut] Cut627  label="Cut942"
  Base = -> Fillet499
  Refine = true
  Tool = -> Fusion375
FEATURE [Part::Fillet] Fillet500
  Base = -> Cut627
  Edges = 4 edges r=0.75: [Edge38,Edge40,Edge60,Edge63]
FEATURE [Part::Fillet] Fillet501
  Base = -> Fillet500
  Edges = 4 edges r=0.7: [Edge41,Edge53,Edge55,Edge67]
FEATURE [Part::Fillet] Fillet502
  Base = -> Fillet501
  Edges = 4 edges r=0.9: [Edge41,Edge59,Edge60,Edge78]
FEATURE [Part::Fillet] Fillet503
  Base = -> Fillet502
  Edges = 2 edges r=1.2: [Edge62,Edge92]
FEATURE [Part::Box] Box694  label="Cube915"
  AttacherType = Attacher::AttachEngine3D
  Height = 14.2
  Length = 0.6
  Placement = pos=(-0.6,13.4,-23.1) rot=(0,0,1;0rad)
  Width = 23.2
FEATURE [Part::Fillet] Fillet504
  Base = -> Box694
  Edges = 4 edges r=3: [Edge9,Edge10,Edge11,Edge12]
  Placement = pos=(2,129,-4.5) rot=(0,0,1;0rad)
FEATURE [Part::Cut] Cut628  label="Cut943"
  Base = -> Fillet498
  Placement = pos=(1.4,0,0) rot=(0,0,1;0rad)
  Refine = true
  Tool = -> Loft021
FEATURE [Part::Cut] Cut629  label="Cut944"
  Base = -> Cut628
  Refine = true
  Tool = -> Fillet504
FEATURE [Part::Box] Box695  label="Cube916"
  AttacherType = Attacher::AttachEngine3D
  Height = 16.6
  Length = 5
  Placement = pos=(3,116.7,-28.8) rot=(0,0,1;0rad)
  Width = 51.1
FEATURE [Part::Cylinder] Cylinder393
  Angle = 360
  AttacherType = Attacher::AttachEngine3D
  Height = 6.6
  Placement = pos=(1.4,165.5,-13.5) rot=(0,1,0;1.5708rad)
  Radius = 1
FEATURE [Part::Cylinder] Cylinder394
  Angle = 360
  AttacherType = Attacher::AttachEngine3D
  Height = 6.6
  Placement = pos=(1.4,165.5,-27.5) rot=(0,1,0;1.5708rad)
  Radius = 1
FEATURE [Part::Cylinder] Cylinder395
  Angle = 360
  AttacherType = Attacher::AttachEngine3D
  Height = 6.6
  Placement = pos=(1.4,142.5,-13.5) rot=(0,1,0;1.5708rad)
  Radius = 1
FEATURE [Part::Cylinder] Cylinder396
  Angle = 360
  AttacherType = Attacher::AttachEngine3D
  Height = 6.6
  Placement = pos=(1.4,142.5,-27.5) rot=(0,1,0;1.5708rad)
  Radius = 1
FEATURE [Part::MultiFuse] Fusion376
  Refine = true
  Shapes = -> [Cylinder393,Cylinder395,Cylinder396,Cylinder394]
FEATURE [Part::Box] Box696  label="Cube917"
  AttacherType = Attacher::AttachEngine3D
  Height = 15
  Length = 5
  Placement = pos=(3,141,-28) rot=(0,0,1;0rad)
  Width = 26
FEATURE [Part::Fillet] Fillet506
  Base = -> Box695
  Edges = 2 edges r=2: [Edge11,Edge12]
FEATURE [Part::Fillet] Fillet507
  Base = -> Box696
  Edges = 4 edges r=1: [Edge9,Edge10,Edge11,Edge12]
FEATURE [Part::Cut] Cut630  label="Cut945"
  Base = -> Fillet506
  Refine = true
  Tool = -> Fillet507
FEATURE [Part::Chamfer] Chamfer076
  Base = -> Cut630
  Edges = 4 edges r=0.7: [Edge8,Edge10,Edge12,Edge14]
FEATURE [Part::MultiFuse] Fusion377
  Refine = true
  Shapes = -> [Cut629,Fusion376,Chamfer076]
FEATURE [Part::Cut] Cut631  label="Cut946"
  Base = -> Fusion377
  Refine = true
  Tool = -> Cylinder391
FEATURE [Part::Box] Box697  label="Cube918"
  AttacherType = Attacher::AttachEngine3D
  Height = 4
  Length = 92
  Placement = pos=(24.6,35.5,120) rot=(0,0,1;0rad)
  Width = 5
FEATURE [Part::Box] Box698  label="Cube919"
  AttacherType = Attacher::AttachEngine3D
  Height = 2
  Length = 5
  Placement = pos=(24.6,7.5,120) rot=(0,0,1;0rad)
  Width = 10
FEATURE [Part::Box] Box699  label="Cube920"
  AttacherType = Attacher::AttachEngine3D
  Height = 2
  Length = 5
  Placement = pos=(24.6,152.5,120) rot=(0,0,1;0rad)
  Width = 10
FEATURE [Part::MultiFuse] Fusion378
  Refine = true
  Shapes = -> [Box698,Box699]
FEATURE [Part::Cut] Cut632  label="Cut947"
  Base = -> Fusion229
  Refine = true
  Tool = -> Fusion378
FEATURE [Part::Box] Box700  label="Cube921"
  AttacherType = Attacher::AttachEngine3D
  Height = 4
  Length = 92
  Placement = pos=(24.6,80,120) rot=(0,0,1;0rad)
  Width = 5
FEATURE [Part::Box] Box701  label="Cube922"
  AttacherType = Attacher::AttachEngine3D
  Height = 4
  Length = 92
  Placement = pos=(24.6,129.5,120) rot=(0,0,1;0rad)
  Width = 5
FEATURE [Part::Box] Box702  label="Cube923"
  AttacherType = Attacher::AttachEngine3D
  Height = 4
  Length = 5
  Placement = pos=(50.6,9.1,120) rot=(0,0,1;0rad)
  Width = 152
FEATURE [Part::Box] Box703  label="Cube924"
  AttacherType = Attacher::AttachEngine3D
  Height = 4
  Length = 5
  Placement = pos=(85.6,9.1,120) rot=(0,0,1;0rad)
  Width = 152
FEATURE [Part::MultiFuse] Fusion379
  Refine = true
  Shapes = -> [Box697,Box700,Box701,Box702,Box703]
FEATURE [Part::MultiFuse] Fusion380  label="cab-top-part-02"
  Refine = true
  Shapes = -> [Cut632,Fusion379]
note: 9 file-system paths scrubbed to <path> (originals preserved in the JSON sidecar)
